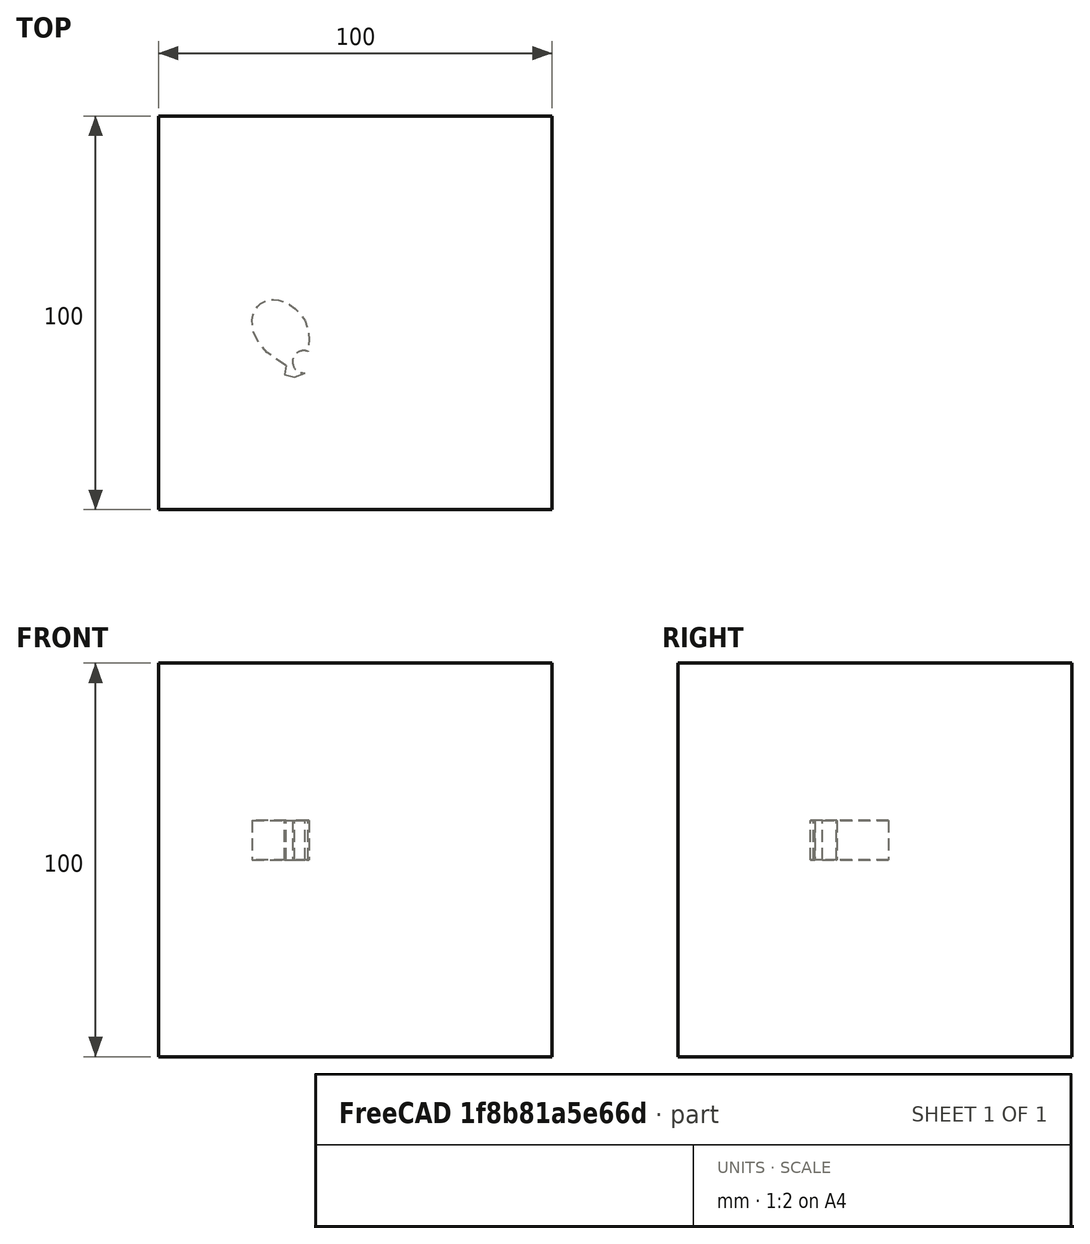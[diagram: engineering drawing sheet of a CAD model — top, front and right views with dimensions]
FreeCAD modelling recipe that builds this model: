
FCSTD DOCUMENT  (FreeCAD 1.0R39109 (Git))
Label: mirrorTest-3c
License: All rights reserved
LicenseURL: http://en.wikipedia.org/wiki/All_rights_reserved
objects: App::DocumentObjectGroupPython×1248, Part::Mirroring×2, App::Part×2, Part::FeaturePython×1, Sketcher::SketchObject×1, Part::Extrusion×1
note: 6 computed .brp shape members not serialized (recipe doc carries the construction recipe); baked Part::Feature solids carry a one-line shape summary decoded from their .brp

FEATURE [App::DocumentObjectGroupPython] HALFPI  # scripted group (container) (typed FeaturePython)
  name = HALFPI
  value = pi/2.
FEATURE [App::DocumentObjectGroupPython] PI  # scripted group (container) (typed FeaturePython)
  name = PI
  value = 1.*pi
FEATURE [App::DocumentObjectGroupPython] TWOPI  # scripted group (container) (typed FeaturePython)
  name = TWOPI
  value = 2.*pi
FEATURE [App::DocumentObjectGroupPython] Constants  # scripted group (container) (typed FeaturePython)
  Group = -> [HALFPI,PI,TWOPI]
FEATURE [App::DocumentObjectGroupPython] Variables  # scripted group (container) (typed FeaturePython)
FEATURE [App::DocumentObjectGroupPython] Quantities  # scripted group (container) (typed FeaturePython)
FEATURE [App::DocumentObjectGroupPython] Isotopes  # scripted group (container) (typed FeaturePython)
FEATURE [App::DocumentObjectGroupPython] Elements  # scripted group (container) (typed FeaturePython)
FEATURE [App::DocumentObjectGroupPython] G4Isotopes  # scripted group (container) (typed FeaturePython)
FEATURE [App::DocumentObjectGroupPython] H_element  # scripted group (container) (typed FeaturePython)
  Z = 1
  atom_value = 1.008
  formula = H
  name = H_element
FEATURE [App::DocumentObjectGroupPython] He_element  # scripted group (container) (typed FeaturePython)
  Z = 2
  atom_value = 4.0026
  formula = He
  name = He_element
FEATURE [App::DocumentObjectGroupPython] Li_element  # scripted group (container) (typed FeaturePython)
  Z = 3
  atom_value = 6.94
  formula = Li
  name = Li_element
FEATURE [App::DocumentObjectGroupPython] Be_element  # scripted group (container) (typed FeaturePython)
  Z = 4
  atom_value = 9.01218
  formula = Be
  name = Be_element
FEATURE [App::DocumentObjectGroupPython] B_element  # scripted group (container) (typed FeaturePython)
  Z = 5
  atom_value = 10.81
  formula = B
  name = B_element
FEATURE [App::DocumentObjectGroupPython] C_element  # scripted group (container) (typed FeaturePython)
  Z = 6
  atom_value = 12.011
  formula = C
  name = C_element
FEATURE [App::DocumentObjectGroupPython] N_element  # scripted group (container) (typed FeaturePython)
  Z = 7
  atom_value = 14.007
  formula = N
  name = N_element
FEATURE [App::DocumentObjectGroupPython] O_element  # scripted group (container) (typed FeaturePython)
  Z = 8
  atom_value = 15.999
  formula = O
  name = O_element
FEATURE [App::DocumentObjectGroupPython] F_element  # scripted group (container) (typed FeaturePython)
  Z = 9
  atom_value = 18.9984
  formula = F
  name = F_element
FEATURE [App::DocumentObjectGroupPython] Ne_element  # scripted group (container) (typed FeaturePython)
  Z = 10
  atom_value = 20.1797
  formula = Ne
  name = Ne_element
FEATURE [App::DocumentObjectGroupPython] Na_element  # scripted group (container) (typed FeaturePython)
  Z = 11
  atom_value = 22.9898
  formula = Na
  name = Na_element
FEATURE [App::DocumentObjectGroupPython] Mg_element  # scripted group (container) (typed FeaturePython)
  Z = 12
  atom_value = 24.305
  formula = Mg
  name = Mg_element
FEATURE [App::DocumentObjectGroupPython] Al_element  # scripted group (container) (typed FeaturePython)
  Z = 13
  atom_value = 26.9815
  formula = Al
  name = Al_element
FEATURE [App::DocumentObjectGroupPython] Si_element  # scripted group (container) (typed FeaturePython)
  Z = 14
  atom_value = 28.085
  formula = Si
  name = Si_element
FEATURE [App::DocumentObjectGroupPython] P_element  # scripted group (container) (typed FeaturePython)
  Z = 15
  atom_value = 30.9738
  formula = P
  name = P_element
FEATURE [App::DocumentObjectGroupPython] S_element  # scripted group (container) (typed FeaturePython)
  Z = 16
  atom_value = 32.06
  formula = S
  name = S_element
FEATURE [App::DocumentObjectGroupPython] Cl_element  # scripted group (container) (typed FeaturePython)
  Z = 17
  atom_value = 35.45
  formula = Cl
  name = Cl_element
FEATURE [App::DocumentObjectGroupPython] Ar_element  # scripted group (container) (typed FeaturePython)
  Z = 18
  atom_value = 39.95
  formula = Ar
  name = Ar_element
FEATURE [App::DocumentObjectGroupPython] K_element  # scripted group (container) (typed FeaturePython)
  Z = 19
  atom_value = 39.0983
  formula = K
  name = K_element
FEATURE [App::DocumentObjectGroupPython] Ca_element  # scripted group (container) (typed FeaturePython)
  Z = 20
  atom_value = 40.078
  formula = Ca
  name = Ca_element
FEATURE [App::DocumentObjectGroupPython] Sc_element  # scripted group (container) (typed FeaturePython)
  Z = 21
  atom_value = 44.9559
  formula = Sc
  name = Sc_element
FEATURE [App::DocumentObjectGroupPython] Ti_element  # scripted group (container) (typed FeaturePython)
  Z = 22
  atom_value = 47.867
  formula = Ti
  name = Ti_element
FEATURE [App::DocumentObjectGroupPython] V_element  # scripted group (container) (typed FeaturePython)
  Z = 23
  atom_value = 50.9415
  formula = V
  name = V_element
FEATURE [App::DocumentObjectGroupPython] Cr_element  # scripted group (container) (typed FeaturePython)
  Z = 24
  atom_value = 51.9961
  formula = Cr
  name = Cr_element
FEATURE [App::DocumentObjectGroupPython] Mn_element  # scripted group (container) (typed FeaturePython)
  Z = 25
  atom_value = 54.938
  formula = Mn
  name = Mn_element
FEATURE [App::DocumentObjectGroupPython] Fe_element  # scripted group (container) (typed FeaturePython)
  Z = 26
  atom_value = 55.845
  formula = Fe
  name = Fe_element
FEATURE [App::DocumentObjectGroupPython] Co_element  # scripted group (container) (typed FeaturePython)
  Z = 27
  atom_value = 58.9332
  formula = Co
  name = Co_element
FEATURE [App::DocumentObjectGroupPython] Ni_element  # scripted group (container) (typed FeaturePython)
  Z = 28
  atom_value = 58.6934
  formula = Ni
  name = Ni_element
FEATURE [App::DocumentObjectGroupPython] Cu_element  # scripted group (container) (typed FeaturePython)
  Z = 29
  atom_value = 63.546
  formula = Cu
  name = Cu_element
FEATURE [App::DocumentObjectGroupPython] Zn_element  # scripted group (container) (typed FeaturePython)
  Z = 30
  atom_value = 65.38
  formula = Zn
  name = Zn_element
FEATURE [App::DocumentObjectGroupPython] Ga_element  # scripted group (container) (typed FeaturePython)
  Z = 31
  atom_value = 69.723
  formula = Ga
  name = Ga_element
FEATURE [App::DocumentObjectGroupPython] Ge_element  # scripted group (container) (typed FeaturePython)
  Z = 32
  atom_value = 72.63
  formula = Ge
  name = Ge_element
FEATURE [App::DocumentObjectGroupPython] As_element  # scripted group (container) (typed FeaturePython)
  Z = 33
  atom_value = 74.9216
  formula = As
  name = As_element
FEATURE [App::DocumentObjectGroupPython] Se_element  # scripted group (container) (typed FeaturePython)
  Z = 34
  atom_value = 78.971
  formula = Se
  name = Se_element
FEATURE [App::DocumentObjectGroupPython] Br_element  # scripted group (container) (typed FeaturePython)
  Z = 35
  atom_value = 79.904
  formula = Br
  name = Br_element
FEATURE [App::DocumentObjectGroupPython] Kr_element  # scripted group (container) (typed FeaturePython)
  Z = 36
  atom_value = 83.798
  formula = Kr
  name = Kr_element
FEATURE [App::DocumentObjectGroupPython] Rb_element  # scripted group (container) (typed FeaturePython)
  Z = 37
  atom_value = 85.4678
  formula = Rb
  name = Rb_element
FEATURE [App::DocumentObjectGroupPython] Sr_element  # scripted group (container) (typed FeaturePython)
  Z = 38
  atom_value = 87.62
  formula = Sr
  name = Sr_element
FEATURE [App::DocumentObjectGroupPython] Y_element  # scripted group (container) (typed FeaturePython)
  Z = 39
  atom_value = 88.9058
  formula = Y
  name = Y_element
FEATURE [App::DocumentObjectGroupPython] Zr_element  # scripted group (container) (typed FeaturePython)
  Z = 40
  atom_value = 91.224
  formula = Zr
  name = Zr_element
FEATURE [App::DocumentObjectGroupPython] Nb_element  # scripted group (container) (typed FeaturePython)
  Z = 41
  atom_value = 92.9064
  formula = Nb
  name = Nb_element
FEATURE [App::DocumentObjectGroupPython] Mo_element  # scripted group (container) (typed FeaturePython)
  Z = 42
  atom_value = 95.95
  formula = Mo
  name = Mo_element
FEATURE [App::DocumentObjectGroupPython] Tc_element  # scripted group (container) (typed FeaturePython)
  Z = 43
  atom_value = 97
  formula = Tc
  name = Tc_element
FEATURE [App::DocumentObjectGroupPython] Ru_element  # scripted group (container) (typed FeaturePython)
  Z = 44
  atom_value = 101.07
  formula = Ru
  name = Ru_element
FEATURE [App::DocumentObjectGroupPython] Rh_element  # scripted group (container) (typed FeaturePython)
  Z = 45
  atom_value = 102.905
  formula = Rh
  name = Rh_element
FEATURE [App::DocumentObjectGroupPython] Pd_element  # scripted group (container) (typed FeaturePython)
  Z = 46
  atom_value = 106.42
  formula = Pd
  name = Pd_element
FEATURE [App::DocumentObjectGroupPython] Ag_element  # scripted group (container) (typed FeaturePython)
  Z = 47
  atom_value = 107.868
  formula = Ag
  name = Ag_element
FEATURE [App::DocumentObjectGroupPython] Cd_element  # scripted group (container) (typed FeaturePython)
  Z = 48
  atom_value = 112.414
  formula = Cd
  name = Cd_element
FEATURE [App::DocumentObjectGroupPython] In_element  # scripted group (container) (typed FeaturePython)
  Z = 49
  atom_value = 114.818
  formula = In
  name = In_element
FEATURE [App::DocumentObjectGroupPython] Sn_element  # scripted group (container) (typed FeaturePython)
  Z = 50
  atom_value = 118.71
  formula = Sn
  name = Sn_element
FEATURE [App::DocumentObjectGroupPython] Sb_element  # scripted group (container) (typed FeaturePython)
  Z = 51
  atom_value = 121.76
  formula = Sb
  name = Sb_element
FEATURE [App::DocumentObjectGroupPython] Te_element  # scripted group (container) (typed FeaturePython)
  Z = 52
  atom_value = 127.6
  formula = Te
  name = Te_element
FEATURE [App::DocumentObjectGroupPython] I_element  # scripted group (container) (typed FeaturePython)
  Z = 53
  atom_value = 126.904
  formula = I
  name = I_element
FEATURE [App::DocumentObjectGroupPython] Xe_element  # scripted group (container) (typed FeaturePython)
  Z = 54
  atom_value = 131.293
  formula = Xe
  name = Xe_element
FEATURE [App::DocumentObjectGroupPython] Cs_element  # scripted group (container) (typed FeaturePython)
  Z = 55
  atom_value = 132.905
  formula = Cs
  name = Cs_element
FEATURE [App::DocumentObjectGroupPython] Ba_element  # scripted group (container) (typed FeaturePython)
  Z = 56
  atom_value = 137.327
  formula = Ba
  name = Ba_element
FEATURE [App::DocumentObjectGroupPython] La_element  # scripted group (container) (typed FeaturePython)
  Z = 57
  atom_value = 138.905
  formula = La
  name = La_element
FEATURE [App::DocumentObjectGroupPython] Ce_element  # scripted group (container) (typed FeaturePython)
  Z = 58
  atom_value = 140.116
  formula = Ce
  name = Ce_element
FEATURE [App::DocumentObjectGroupPython] Pr_element  # scripted group (container) (typed FeaturePython)
  Z = 59
  atom_value = 140.908
  formula = Pr
  name = Pr_element
FEATURE [App::DocumentObjectGroupPython] Nd_element  # scripted group (container) (typed FeaturePython)
  Z = 60
  atom_value = 144.242
  formula = Nd
  name = Nd_element
FEATURE [App::DocumentObjectGroupPython] Pm_element  # scripted group (container) (typed FeaturePython)
  Z = 61
  atom_value = 145
  formula = Pm
  name = Pm_element
FEATURE [App::DocumentObjectGroupPython] Sm_element  # scripted group (container) (typed FeaturePython)
  Z = 62
  atom_value = 150.36
  formula = Sm
  name = Sm_element
FEATURE [App::DocumentObjectGroupPython] Eu_element  # scripted group (container) (typed FeaturePython)
  Z = 63
  atom_value = 151.964
  formula = Eu
  name = Eu_element
FEATURE [App::DocumentObjectGroupPython] Gd_element  # scripted group (container) (typed FeaturePython)
  Z = 64
  atom_value = 157.25
  formula = Gd
  name = Gd_element
FEATURE [App::DocumentObjectGroupPython] Tb_element  # scripted group (container) (typed FeaturePython)
  Z = 65
  atom_value = 158.925
  formula = Tb
  name = Tb_element
FEATURE [App::DocumentObjectGroupPython] Dy_element  # scripted group (container) (typed FeaturePython)
  Z = 66
  atom_value = 162.5
  formula = Dy
  name = Dy_element
FEATURE [App::DocumentObjectGroupPython] Ho_element  # scripted group (container) (typed FeaturePython)
  Z = 67
  atom_value = 164.93
  formula = Ho
  name = Ho_element
FEATURE [App::DocumentObjectGroupPython] Er_element  # scripted group (container) (typed FeaturePython)
  Z = 68
  atom_value = 167.259
  formula = Er
  name = Er_element
FEATURE [App::DocumentObjectGroupPython] Tm_element  # scripted group (container) (typed FeaturePython)
  Z = 69
  atom_value = 168.934
  formula = Tm
  name = Tm_element
FEATURE [App::DocumentObjectGroupPython] Yb_element  # scripted group (container) (typed FeaturePython)
  Z = 70
  atom_value = 173.045
  formula = Yb
  name = Yb_element
FEATURE [App::DocumentObjectGroupPython] Lu_element  # scripted group (container) (typed FeaturePython)
  Z = 71
  atom_value = 174.967
  formula = Lu
  name = Lu_element
FEATURE [App::DocumentObjectGroupPython] Hf_element  # scripted group (container) (typed FeaturePython)
  Z = 72
  atom_value = 178.49
  formula = Hf
  name = Hf_element
FEATURE [App::DocumentObjectGroupPython] Ta_element  # scripted group (container) (typed FeaturePython)
  Z = 73
  atom_value = 180.948
  formula = Ta
  name = Ta_element
FEATURE [App::DocumentObjectGroupPython] W_element  # scripted group (container) (typed FeaturePython)
  Z = 74
  atom_value = 183.84
  formula = W
  name = W_element
FEATURE [App::DocumentObjectGroupPython] Re_element  # scripted group (container) (typed FeaturePython)
  Z = 75
  atom_value = 186.207
  formula = Re
  name = Re_element
FEATURE [App::DocumentObjectGroupPython] Os_element  # scripted group (container) (typed FeaturePython)
  Z = 76
  atom_value = 190.23
  formula = Os
  name = Os_element
FEATURE [App::DocumentObjectGroupPython] Ir_element  # scripted group (container) (typed FeaturePython)
  Z = 77
  atom_value = 192.217
  formula = Ir
  name = Ir_element
FEATURE [App::DocumentObjectGroupPython] Pt_element  # scripted group (container) (typed FeaturePython)
  Z = 78
  atom_value = 195.084
  formula = Pt
  name = Pt_element
FEATURE [App::DocumentObjectGroupPython] Au_element  # scripted group (container) (typed FeaturePython)
  Z = 79
  atom_value = 196.967
  formula = Au
  name = Au_element
FEATURE [App::DocumentObjectGroupPython] Hg_element  # scripted group (container) (typed FeaturePython)
  Z = 80
  atom_value = 200.592
  formula = Hg
  name = Hg_element
FEATURE [App::DocumentObjectGroupPython] Tl_element  # scripted group (container) (typed FeaturePython)
  Z = 81
  atom_value = 204.38
  formula = Tl
  name = Tl_element
FEATURE [App::DocumentObjectGroupPython] Pb_element  # scripted group (container) (typed FeaturePython)
  Z = 82
  atom_value = 207.2
  formula = Pb
  name = Pb_element
FEATURE [App::DocumentObjectGroupPython] Bi_element  # scripted group (container) (typed FeaturePython)
  Z = 83
  atom_value = 208.98
  formula = Bi
  name = Bi_element
FEATURE [App::DocumentObjectGroupPython] Po_element  # scripted group (container) (typed FeaturePython)
  Z = 84
  atom_value = 209
  formula = Po
  name = Po_element
FEATURE [App::DocumentObjectGroupPython] At_element  # scripted group (container) (typed FeaturePython)
  Z = 85
  atom_value = 210
  formula = At
  name = At_element
FEATURE [App::DocumentObjectGroupPython] Rn_element  # scripted group (container) (typed FeaturePython)
  Z = 86
  atom_value = 222
  formula = Rn
  name = Rn_element
FEATURE [App::DocumentObjectGroupPython] Fr_element  # scripted group (container) (typed FeaturePython)
  Z = 87
  atom_value = 223
  formula = Fr
  name = Fr_element
FEATURE [App::DocumentObjectGroupPython] Ra_element  # scripted group (container) (typed FeaturePython)
  Z = 88
  atom_value = 226
  formula = Ra
  name = Ra_element
FEATURE [App::DocumentObjectGroupPython] Ac_element  # scripted group (container) (typed FeaturePython)
  Z = 89
  atom_value = 227
  formula = Ac
  name = Ac_element
FEATURE [App::DocumentObjectGroupPython] Th_element  # scripted group (container) (typed FeaturePython)
  Z = 90
  atom_value = 232.038
  formula = Th
  name = Th_element
FEATURE [App::DocumentObjectGroupPython] Pa_element  # scripted group (container) (typed FeaturePython)
  Z = 91
  atom_value = 231.036
  formula = Pa
  name = Pa_element
FEATURE [App::DocumentObjectGroupPython] U_element  # scripted group (container) (typed FeaturePython)
  Z = 92
  atom_value = 238.029
  formula = U
  name = U_element
FEATURE [App::DocumentObjectGroupPython] Np_element  # scripted group (container) (typed FeaturePython)
  Z = 93
  atom_value = 237
  formula = Np
  name = Np_element
FEATURE [App::DocumentObjectGroupPython] Pu_element  # scripted group (container) (typed FeaturePython)
  Z = 94
  atom_value = 244
  formula = Pu
  name = Pu_element
FEATURE [App::DocumentObjectGroupPython] Am_element  # scripted group (container) (typed FeaturePython)
  Z = 95
  atom_value = 243
  formula = Am
  name = Am_element
FEATURE [App::DocumentObjectGroupPython] Cm_element  # scripted group (container) (typed FeaturePython)
  Z = 96
  atom_value = 247
  formula = Cm
  name = Cm_element
FEATURE [App::DocumentObjectGroupPython] Bk_element  # scripted group (container) (typed FeaturePython)
  Z = 97
  atom_value = 247
  formula = Bk
  name = Bk_element
FEATURE [App::DocumentObjectGroupPython] Cf_element  # scripted group (container) (typed FeaturePython)
  Z = 98
  atom_value = 251
  formula = Cf
  name = Cf_element
FEATURE [App::DocumentObjectGroupPython] G4Elements  # scripted group (container) (typed FeaturePython)
  Group = -> [H_element,He_element,Li_element,Be_element,B_element,C_element,N_element,O_element,F_element,Ne_element,Na_element,Mg_element,Al_element,Si_element,P_element,S_element,Cl_element,Ar_element,K_element,Ca_element,Sc_element,Ti_element,V_element,Cr_element,Mn_element,Fe_element,Co_element,Ni_element,Cu_element,Zn_element,Ga_element,Ge_element,As_element,Se_element,Br_element,Kr_element,Rb_element,+61 more]
FEATURE [App::DocumentObjectGroupPython] H_element001  label="H_element : 0.101"  # scripted group (container) (typed FeaturePython)
  n = 0.101327
FEATURE [App::DocumentObjectGroupPython] C_element001  label="C_element : 0.775"  # scripted group (container) (typed FeaturePython)
  n = 0.7755
FEATURE [App::DocumentObjectGroupPython] N_element001  label="N_element : 0.035"  # scripted group (container) (typed FeaturePython)
  n = 0.035057
FEATURE [App::DocumentObjectGroupPython] O_element001  label="O_element : 0.052"  # scripted group (container) (typed FeaturePython)
  n = 0.0523159
FEATURE [App::DocumentObjectGroupPython] F_element001  label="F_element : 0.017"  # scripted group (container) (typed FeaturePython)
  n = 0.017422
FEATURE [App::DocumentObjectGroupPython] Ca_element001  label="Ca_element : 0.018"  # scripted group (container) (typed FeaturePython)
  n = 0.018378
FEATURE [App::DocumentObjectGroupPython] G4_A_150_TISSUE  label="G4_A-150_TISSUE"  # scripted group (container) (typed FeaturePython)
  Dunit = g/cm3
  Dvalue = 1.127
  Group = -> [H_element001,C_element001,N_element001,O_element001,F_element001,Ca_element001]
  conduct = 2
  density = 1
  expand = 3
  formula = G4_A-150_TISSUE
  name = G4_A-150_TISSUE
  specific = 4
FEATURE [App::DocumentObjectGroupPython] C_element002  label="C_element : 3"  # scripted group (container) (typed FeaturePython)
  n = 3
  ref = C_element
FEATURE [App::DocumentObjectGroupPython] H_element002  label="H_element : 6"  # scripted group (container) (typed FeaturePython)
  n = 6
  ref = H_element
FEATURE [App::DocumentObjectGroupPython] O_element002  label="O_element : 1"  # scripted group (container) (typed FeaturePython)
  n = 1
  ref = O_element
FEATURE [App::DocumentObjectGroupPython] G4_ACETONE  # scripted group (container) (typed FeaturePython)
  Dunit = g/cm3
  Dvalue = 0.7899
  Group = -> [C_element002,H_element002,O_element002]
  conduct = 2
  density = 1
  expand = 3
  formula = G4_ACETONE
  name = G4_ACETONE
  specific = 4
FEATURE [App::DocumentObjectGroupPython] C_element003  label="C_element : 2"  # scripted group (container) (typed FeaturePython)
  n = 2
  ref = C_element
FEATURE [App::DocumentObjectGroupPython] H_element003  label="H_element : 2"  # scripted group (container) (typed FeaturePython)
  n = 2
  ref = H_element
FEATURE [App::DocumentObjectGroupPython] G4_ACETYLENE  # scripted group (container) (typed FeaturePython)
  Dunit = g/cm3
  Dvalue = 0.0010967
  Group = -> [C_element003,H_element003]
  conduct = 2
  density = 1
  expand = 3
  formula = G4_ACETYLENE
  name = G4_ACETYLENE
  specific = 4
FEATURE [App::DocumentObjectGroupPython] C_element004  label="C_element : 5"  # scripted group (container) (typed FeaturePython)
  n = 5
  ref = C_element
FEATURE [App::DocumentObjectGroupPython] H_element004  label="H_element : 5"  # scripted group (container) (typed FeaturePython)
  n = 5
  ref = H_element
FEATURE [App::DocumentObjectGroupPython] N_element002  label="N_element : 5"  # scripted group (container) (typed FeaturePython)
  n = 5
  ref = N_element
FEATURE [App::DocumentObjectGroupPython] G4_ADENINE  # scripted group (container) (typed FeaturePython)
  Dunit = g/cm3
  Dvalue = 1.6
  Group = -> [C_element004,H_element004,N_element002]
  conduct = 2
  density = 1
  expand = 3
  formula = G4_ADENINE
  name = G4_ADENINE
  specific = 4
FEATURE [App::DocumentObjectGroupPython] H_element005  label="H_element : 0.114"  # scripted group (container) (typed FeaturePython)
  n = 0.114
FEATURE [App::DocumentObjectGroupPython] C_element005  label="C_element : 0.598"  # scripted group (container) (typed FeaturePython)
  n = 0.598
FEATURE [App::DocumentObjectGroupPython] N_element003  label="N_element : 0.007"  # scripted group (container) (typed FeaturePython)
  n = 0.007
FEATURE [App::DocumentObjectGroupPython] O_element003  label="O_element : 0.278"  # scripted group (container) (typed FeaturePython)
  n = 0.278
FEATURE [App::DocumentObjectGroupPython] Na_element001  label="Na_element : 0.001"  # scripted group (container) (typed FeaturePython)
  n = 0.001
FEATURE [App::DocumentObjectGroupPython] S_element001  label="S_element : 0.001"  # scripted group (container) (typed FeaturePython)
  n = 0.001
FEATURE [App::DocumentObjectGroupPython] Cl_element001  label="Cl_element : 0.001"  # scripted group (container) (typed FeaturePython)
  n = 0.001
FEATURE [App::DocumentObjectGroupPython] G4_ADIPOSE_TISSUE_ICRP  # scripted group (container) (typed FeaturePython)
  Dunit = g/cm3
  Dvalue = 0.95
  Group = -> [H_element005,C_element005,N_element003,O_element003,Na_element001,S_element001,Cl_element001]
  conduct = 2
  density = 1
  expand = 3
  formula = G4_ADIPOSE_TISSUE_ICRP
  name = G4_ADIPOSE_TISSUE_ICRP
  specific = 4
FEATURE [App::DocumentObjectGroupPython] C_element006  label="C_element : 0.000"  # scripted group (container) (typed FeaturePython)
  n = 0.000124
FEATURE [App::DocumentObjectGroupPython] N_element004  label="N_element : 0.755"  # scripted group (container) (typed FeaturePython)
  n = 0.755268
FEATURE [App::DocumentObjectGroupPython] O_element004  label="O_element : 0.232"  # scripted group (container) (typed FeaturePython)
  n = 0.231781
FEATURE [App::DocumentObjectGroupPython] Ar_element001  label="Ar_element : 0.013"  # scripted group (container) (typed FeaturePython)
  n = 0.012827
FEATURE [App::DocumentObjectGroupPython] G4_AIR  # scripted group (container) (typed FeaturePython)
  Dunit = g/cm3
  Dvalue = 0.00120479
  Group = -> [C_element006,N_element004,O_element004,Ar_element001]
  conduct = 2
  density = 1
  expand = 3
  formula = G4_AIR
  name = G4_AIR
  specific = 4
FEATURE [App::DocumentObjectGroupPython] C_element007  label="C_element : 006"  # scripted group (container) (typed FeaturePython)
  n = 3
  ref = C_element
FEATURE [App::DocumentObjectGroupPython] H_element006  label="H_element : 7"  # scripted group (container) (typed FeaturePython)
  n = 7
  ref = H_element
FEATURE [App::DocumentObjectGroupPython] N_element005  label="N_element : 1"  # scripted group (container) (typed FeaturePython)
  n = 1
  ref = N_element
FEATURE [App::DocumentObjectGroupPython] O_element005  label="O_element : 2"  # scripted group (container) (typed FeaturePython)
  n = 2
  ref = O_element
FEATURE [App::DocumentObjectGroupPython] G4_ALANINE  # scripted group (container) (typed FeaturePython)
  Dunit = g/cm3
  Dvalue = 1.42
  Group = -> [C_element007,H_element006,N_element005,O_element005]
  conduct = 2
  density = 1
  expand = 3
  formula = G4_ALANINE
  name = G4_ALANINE
  specific = 4
FEATURE [App::DocumentObjectGroupPython] Al_element001  label="Al_element : 2"  # scripted group (container) (typed FeaturePython)
  n = 2
  ref = Al_element
FEATURE [App::DocumentObjectGroupPython] O_element006  label="O_element : 3"  # scripted group (container) (typed FeaturePython)
  n = 3
  ref = O_element
FEATURE [App::DocumentObjectGroupPython] G4_ALUMINUM_OXIDE  # scripted group (container) (typed FeaturePython)
  Dunit = g/cm3
  Dvalue = 3.97
  Group = -> [Al_element001,O_element006]
  conduct = 2
  density = 1
  expand = 3
  formula = G4_ALUMINUM_OXIDE
  name = G4_ALUMINUM_OXIDE
  specific = 4
FEATURE [App::DocumentObjectGroupPython] H_element007  label="H_element : 0.106"  # scripted group (container) (typed FeaturePython)
  n = 0.10593
FEATURE [App::DocumentObjectGroupPython] C_element008  label="C_element : 0.789"  # scripted group (container) (typed FeaturePython)
  n = 0.788974
FEATURE [App::DocumentObjectGroupPython] O_element007  label="O_element : 0.105"  # scripted group (container) (typed FeaturePython)
  n = 0.105096
FEATURE [App::DocumentObjectGroupPython] G4_AMBER  # scripted group (container) (typed FeaturePython)
  Dunit = g/cm3
  Dvalue = 1.1
  Group = -> [H_element007,C_element008,O_element007]
  conduct = 2
  density = 1
  expand = 3
  formula = G4_AMBER
  name = G4_AMBER
  specific = 4
FEATURE [App::DocumentObjectGroupPython] N_element006  label="N_element : 006"  # scripted group (container) (typed FeaturePython)
  n = 1
  ref = N_element
FEATURE [App::DocumentObjectGroupPython] H_element008  label="H_element : 3"  # scripted group (container) (typed FeaturePython)
  n = 3
  ref = H_element
FEATURE [App::DocumentObjectGroupPython] G4_AMMONIA  # scripted group (container) (typed FeaturePython)
  Dunit = g/cm3
  Dvalue = 0.000826019
  Group = -> [N_element006,H_element008]
  conduct = 2
  density = 1
  expand = 3
  formula = G4_AMMONIA
  name = G4_AMMONIA
  specific = 4
FEATURE [App::DocumentObjectGroupPython] C_element009  label="C_element : 6"  # scripted group (container) (typed FeaturePython)
  n = 6
  ref = C_element
FEATURE [App::DocumentObjectGroupPython] H_element009  label="H_element : 008"  # scripted group (container) (typed FeaturePython)
  n = 7
  ref = H_element
FEATURE [App::DocumentObjectGroupPython] N_element007  label="N_element : 007"  # scripted group (container) (typed FeaturePython)
  n = 1
  ref = N_element
FEATURE [App::DocumentObjectGroupPython] G4_ANILINE  # scripted group (container) (typed FeaturePython)
  Dunit = g/cm3
  Dvalue = 1.0235
  Group = -> [C_element009,H_element009,N_element007]
  conduct = 2
  density = 1
  expand = 3
  formula = G4_ANILINE
  name = G4_ANILINE
  specific = 4
FEATURE [App::DocumentObjectGroupPython] C_element010  label="C_element : 14"  # scripted group (container) (typed FeaturePython)
  n = 14
  ref = C_element
FEATURE [App::DocumentObjectGroupPython] H_element010  label="H_element : 10"  # scripted group (container) (typed FeaturePython)
  n = 10
  ref = H_element
FEATURE [App::DocumentObjectGroupPython] G4_ANTHRACENE  # scripted group (container) (typed FeaturePython)
  Dunit = g/cm3
  Dvalue = 1.283
  Group = -> [C_element010,H_element010]
  conduct = 2
  density = 1
  expand = 3
  formula = G4_ANTHRACENE
  name = G4_ANTHRACENE
  specific = 4
FEATURE [App::DocumentObjectGroupPython] H_element011  label="H_element : 0.065"  # scripted group (container) (typed FeaturePython)
  n = 0.0654709
FEATURE [App::DocumentObjectGroupPython] C_element011  label="C_element : 0.537"  # scripted group (container) (typed FeaturePython)
  n = 0.536944
FEATURE [App::DocumentObjectGroupPython] N_element008  label="N_element : 0.021"  # scripted group (container) (typed FeaturePython)
  n = 0.0215
FEATURE [App::DocumentObjectGroupPython] O_element008  label="O_element : 0.032"  # scripted group (container) (typed FeaturePython)
  n = 0.032085
FEATURE [App::DocumentObjectGroupPython] F_element002  label="F_element : 0.167"  # scripted group (container) (typed FeaturePython)
  n = 0.167411
FEATURE [App::DocumentObjectGroupPython] Ca_element002  label="Ca_element : 0.177"  # scripted group (container) (typed FeaturePython)
  n = 0.176589
FEATURE [App::DocumentObjectGroupPython] G4_B_100_BONE  label="G4_B-100_BONE"  # scripted group (container) (typed FeaturePython)
  Dunit = g/cm3
  Dvalue = 1.45
  Group = -> [H_element011,C_element011,N_element008,O_element008,F_element002,Ca_element002]
  conduct = 2
  density = 1
  expand = 3
  formula = G4_B-100_BONE
  name = G4_B-100_BONE
  specific = 4
FEATURE [App::DocumentObjectGroupPython] H_element012  label="H_element : 0.057"  # scripted group (container) (typed FeaturePython)
  n = 0.057441
FEATURE [App::DocumentObjectGroupPython] C_element012  label="C_element : 0.790"  # scripted group (container) (typed FeaturePython)
  n = 0.774591
FEATURE [App::DocumentObjectGroupPython] O_element009  label="O_element : 0.168"  # scripted group (container) (typed FeaturePython)
  n = 0.167968
FEATURE [App::DocumentObjectGroupPython] G4_BAKELITE  # scripted group (container) (typed FeaturePython)
  Dunit = g/cm3
  Dvalue = 1.25
  Group = -> [H_element012,C_element012,O_element009]
  conduct = 2
  density = 1
  expand = 3
  formula = G4_BAKELITE
  name = G4_BAKELITE
  specific = 4
FEATURE [App::DocumentObjectGroupPython] Ba_element001  label="Ba_element : 1"  # scripted group (container) (typed FeaturePython)
  n = 1
  ref = Ba_element
FEATURE [App::DocumentObjectGroupPython] F_element003  label="F_element : 2"  # scripted group (container) (typed FeaturePython)
  n = 2
  ref = F_element
FEATURE [App::DocumentObjectGroupPython] G4_BARIUM_FLUORIDE  # scripted group (container) (typed FeaturePython)
  Dunit = g/cm3
  Dvalue = 4.89
  Group = -> [Ba_element001,F_element003]
  conduct = 2
  density = 1
  expand = 3
  formula = G4_BARIUM_FLUORIDE
  name = G4_BARIUM_FLUORIDE
  specific = 4
FEATURE [App::DocumentObjectGroupPython] Ba_element002  label="Ba_element : 002"  # scripted group (container) (typed FeaturePython)
  n = 1
  ref = Ba_element
FEATURE [App::DocumentObjectGroupPython] S_element002  label="S_element : 1"  # scripted group (container) (typed FeaturePython)
  n = 1
  ref = S_element
FEATURE [App::DocumentObjectGroupPython] O_element010  label="O_element : 4"  # scripted group (container) (typed FeaturePython)
  n = 4
  ref = O_element
FEATURE [App::DocumentObjectGroupPython] G4_BARIUM_SULFATE  # scripted group (container) (typed FeaturePython)
  Dunit = g/cm3
  Dvalue = 4.5
  Group = -> [Ba_element002,S_element002,O_element010]
  conduct = 2
  density = 1
  expand = 3
  formula = G4_BARIUM_SULFATE
  name = G4_BARIUM_SULFATE
  specific = 4
FEATURE [App::DocumentObjectGroupPython] C_element013  label="C_element : 007"  # scripted group (container) (typed FeaturePython)
  n = 6
  ref = C_element
FEATURE [App::DocumentObjectGroupPython] H_element013  label="H_element : 009"  # scripted group (container) (typed FeaturePython)
  n = 6
  ref = H_element
FEATURE [App::DocumentObjectGroupPython] G4_BENZENE  # scripted group (container) (typed FeaturePython)
  Dunit = g/cm3
  Dvalue = 0.87865
  Group = -> [C_element013,H_element013]
  conduct = 2
  density = 1
  expand = 3
  formula = G4_BENZENE
  name = G4_BENZENE
  specific = 4
FEATURE [App::DocumentObjectGroupPython] Be_element001  label="Be_element : 1"  # scripted group (container) (typed FeaturePython)
  n = 1
  ref = Be_element
FEATURE [App::DocumentObjectGroupPython] O_element011  label="O_element : 005"  # scripted group (container) (typed FeaturePython)
  n = 1
  ref = O_element
FEATURE [App::DocumentObjectGroupPython] G4_BERYLLIUM_OXIDE  # scripted group (container) (typed FeaturePython)
  Dunit = g/cm3
  Dvalue = 3.01
  Group = -> [Be_element001,O_element011]
  conduct = 2
  density = 1
  expand = 3
  formula = G4_BERYLLIUM_OXIDE
  name = G4_BERYLLIUM_OXIDE
  specific = 4
FEATURE [App::DocumentObjectGroupPython] Bi_element001  label="Bi_element : 4"  # scripted group (container) (typed FeaturePython)
  n = 4
  ref = Bi_element
FEATURE [App::DocumentObjectGroupPython] Ge_element001  label="Ge_element : 3"  # scripted group (container) (typed FeaturePython)
  n = 3
  ref = Ge_element
FEATURE [App::DocumentObjectGroupPython] O_element012  label="O_element : 12"  # scripted group (container) (typed FeaturePython)
  n = 12
  ref = O_element
FEATURE [App::DocumentObjectGroupPython] G4_BGO  # scripted group (container) (typed FeaturePython)
  Dunit = g/cm3
  Dvalue = 7.13
  Group = -> [Bi_element001,Ge_element001,O_element012]
  conduct = 2
  density = 1
  expand = 3
  formula = G4_BGO
  name = G4_BGO
  specific = 4
FEATURE [App::DocumentObjectGroupPython] H_element014  label="H_element : 0.102"  # scripted group (container) (typed FeaturePython)
  n = 0.102
FEATURE [App::DocumentObjectGroupPython] C_element014  label="C_element : 0.110"  # scripted group (container) (typed FeaturePython)
  n = 0.11
FEATURE [App::DocumentObjectGroupPython] N_element009  label="N_element : 0.033"  # scripted group (container) (typed FeaturePython)
  n = 0.033
FEATURE [App::DocumentObjectGroupPython] O_element013  label="O_element : 0.745"  # scripted group (container) (typed FeaturePython)
  n = 0.745
FEATURE [App::DocumentObjectGroupPython] Na_element002  label="Na_element : 0.002"  # scripted group (container) (typed FeaturePython)
  n = 0.001
FEATURE [App::DocumentObjectGroupPython] P_element001  label="P_element : 0.001"  # scripted group (container) (typed FeaturePython)
  n = 0.001
FEATURE [App::DocumentObjectGroupPython] S_element003  label="S_element : 0.002"  # scripted group (container) (typed FeaturePython)
  n = 0.002
FEATURE [App::DocumentObjectGroupPython] Cl_element002  label="Cl_element : 0.003"  # scripted group (container) (typed FeaturePython)
  n = 0.003
FEATURE [App::DocumentObjectGroupPython] K_element001  label="K_element : 0.002"  # scripted group (container) (typed FeaturePython)
  n = 0.002
FEATURE [App::DocumentObjectGroupPython] Fe_element001  label="Fe_element : 0.001"  # scripted group (container) (typed FeaturePython)
  n = 0.001
FEATURE [App::DocumentObjectGroupPython] G4_BLOOD_ICRP  # scripted group (container) (typed FeaturePython)
  Dunit = g/cm3
  Dvalue = 1.06
  Group = -> [H_element014,C_element014,N_element009,O_element013,Na_element002,P_element001,S_element003,Cl_element002,K_element001,Fe_element001]
  conduct = 2
  density = 1
  expand = 3
  formula = G4_BLOOD_ICRP
  name = G4_BLOOD_ICRP
  specific = 4
FEATURE [App::DocumentObjectGroupPython] H_element015  label="H_element : 0.064"  # scripted group (container) (typed FeaturePython)
  n = 0.064
FEATURE [App::DocumentObjectGroupPython] C_element015  label="C_element : 0.278"  # scripted group (container) (typed FeaturePython)
  n = 0.278
FEATURE [App::DocumentObjectGroupPython] N_element010  label="N_element : 0.027"  # scripted group (container) (typed FeaturePython)
  n = 0.027
FEATURE [App::DocumentObjectGroupPython] O_element014  label="O_element : 0.410"  # scripted group (container) (typed FeaturePython)
  n = 0.41
FEATURE [App::DocumentObjectGroupPython] Mg_element001  label="Mg_element : 0.002"  # scripted group (container) (typed FeaturePython)
  n = 0.002
FEATURE [App::DocumentObjectGroupPython] P_element002  label="P_element : 0.070"  # scripted group (container) (typed FeaturePython)
  n = 0.07
FEATURE [App::DocumentObjectGroupPython] S_element004  label="S_element : 0.003"  # scripted group (container) (typed FeaturePython)
  n = 0.002
FEATURE [App::DocumentObjectGroupPython] Ca_element003  label="Ca_element : 0.147"  # scripted group (container) (typed FeaturePython)
  n = 0.147
FEATURE [App::DocumentObjectGroupPython] G4_BONE_COMPACT_ICRU  # scripted group (container) (typed FeaturePython)
  Dunit = g/cm3
  Dvalue = 1.85
  Group = -> [H_element015,C_element015,N_element010,O_element014,Mg_element001,P_element002,S_element004,Ca_element003]
  conduct = 2
  density = 1
  expand = 3
  formula = G4_BONE_COMPACT_ICRU
  name = G4_BONE_COMPACT_ICRU
  specific = 4
FEATURE [App::DocumentObjectGroupPython] H_element016  label="H_element : 0.034"  # scripted group (container) (typed FeaturePython)
  n = 0.034
FEATURE [App::DocumentObjectGroupPython] C_element016  label="C_element : 0.155"  # scripted group (container) (typed FeaturePython)
  n = 0.155
FEATURE [App::DocumentObjectGroupPython] N_element011  label="N_element : 0.042"  # scripted group (container) (typed FeaturePython)
  n = 0.042
FEATURE [App::DocumentObjectGroupPython] O_element015  label="O_element : 0.435"  # scripted group (container) (typed FeaturePython)
  n = 0.435
FEATURE [App::DocumentObjectGroupPython] Na_element003  label="Na_element : 0.003"  # scripted group (container) (typed FeaturePython)
  n = 0.001
FEATURE [App::DocumentObjectGroupPython] Mg_element002  label="Mg_element : 0.003"  # scripted group (container) (typed FeaturePython)
  n = 0.002
FEATURE [App::DocumentObjectGroupPython] P_element003  label="P_element : 0.103"  # scripted group (container) (typed FeaturePython)
  n = 0.103
FEATURE [App::DocumentObjectGroupPython] S_element005  label="S_element : 0.004"  # scripted group (container) (typed FeaturePython)
  n = 0.003
FEATURE [App::DocumentObjectGroupPython] Ca_element004  label="Ca_element : 0.225"  # scripted group (container) (typed FeaturePython)
  n = 0.225
FEATURE [App::DocumentObjectGroupPython] G4_BONE_CORTICAL_ICRP  # scripted group (container) (typed FeaturePython)
  Dunit = g/cm3
  Dvalue = 1.92
  Group = -> [H_element016,C_element016,N_element011,O_element015,Na_element003,Mg_element002,P_element003,S_element005,Ca_element004]
  conduct = 2
  density = 1
  expand = 3
  formula = G4_BONE_CORTICAL_ICRP
  name = G4_BONE_CORTICAL_ICRP
  specific = 4
FEATURE [App::DocumentObjectGroupPython] B_element001  label="B_element : 4"  # scripted group (container) (typed FeaturePython)
  n = 4
  ref = B_element
FEATURE [App::DocumentObjectGroupPython] C_element017  label="C_element : 1"  # scripted group (container) (typed FeaturePython)
  n = 1
  ref = C_element
FEATURE [App::DocumentObjectGroupPython] G4_BORON_CARBIDE  # scripted group (container) (typed FeaturePython)
  Dunit = g/cm3
  Dvalue = 2.52
  Group = -> [B_element001,C_element017]
  conduct = 2
  density = 1
  expand = 3
  formula = G4_BORON_CARBIDE
  name = G4_BORON_CARBIDE
  specific = 4
FEATURE [App::DocumentObjectGroupPython] B_element002  label="B_element : 2"  # scripted group (container) (typed FeaturePython)
  n = 2
  ref = B_element
FEATURE [App::DocumentObjectGroupPython] O_element016  label="O_element : 006"  # scripted group (container) (typed FeaturePython)
  n = 3
  ref = O_element
FEATURE [App::DocumentObjectGroupPython] G4_BORON_OXIDE  # scripted group (container) (typed FeaturePython)
  Dunit = g/cm3
  Dvalue = 1.812
  Group = -> [B_element002,O_element016]
  conduct = 2
  density = 1
  expand = 3
  formula = G4_BORON_OXIDE
  name = G4_BORON_OXIDE
  specific = 4
FEATURE [App::DocumentObjectGroupPython] H_element017  label="H_element : 0.107"  # scripted group (container) (typed FeaturePython)
  n = 0.107
FEATURE [App::DocumentObjectGroupPython] C_element018  label="C_element : 0.145"  # scripted group (container) (typed FeaturePython)
  n = 0.145
FEATURE [App::DocumentObjectGroupPython] N_element012  label="N_element : 0.022"  # scripted group (container) (typed FeaturePython)
  n = 0.022
FEATURE [App::DocumentObjectGroupPython] O_element017  label="O_element : 0.712"  # scripted group (container) (typed FeaturePython)
  n = 0.712
FEATURE [App::DocumentObjectGroupPython] Na_element004  label="Na_element : 0.004"  # scripted group (container) (typed FeaturePython)
  n = 0.002
FEATURE [App::DocumentObjectGroupPython] P_element004  label="P_element : 0.004"  # scripted group (container) (typed FeaturePython)
  n = 0.004
FEATURE [App::DocumentObjectGroupPython] S_element006  label="S_element : 0.005"  # scripted group (container) (typed FeaturePython)
  n = 0.002
FEATURE [App::DocumentObjectGroupPython] Cl_element003  label="Cl_element : 0.004"  # scripted group (container) (typed FeaturePython)
  n = 0.003
FEATURE [App::DocumentObjectGroupPython] K_element002  label="K_element : 0.003"  # scripted group (container) (typed FeaturePython)
  n = 0.003
FEATURE [App::DocumentObjectGroupPython] G4_BRAIN_ICRP  # scripted group (container) (typed FeaturePython)
  Dunit = g/cm3
  Dvalue = 1.04
  Group = -> [H_element017,C_element018,N_element012,O_element017,Na_element004,P_element004,S_element006,Cl_element003,K_element002]
  conduct = 2
  density = 1
  expand = 3
  formula = G4_BRAIN_ICRP
  name = G4_BRAIN_ICRP
  specific = 4
FEATURE [App::DocumentObjectGroupPython] C_element019  label="C_element : 4"  # scripted group (container) (typed FeaturePython)
  n = 4
  ref = C_element
FEATURE [App::DocumentObjectGroupPython] H_element018  label="H_element : 010"  # scripted group (container) (typed FeaturePython)
  n = 10
  ref = H_element
FEATURE [App::DocumentObjectGroupPython] G4_BUTANE  # scripted group (container) (typed FeaturePython)
  Dunit = g/cm3
  Dvalue = 0.00249343
  Group = -> [C_element019,H_element018]
  conduct = 2
  density = 1
  expand = 3
  formula = G4_BUTANE
  name = G4_BUTANE
  specific = 4
FEATURE [App::DocumentObjectGroupPython] C_element020  label="C_element : 008"  # scripted group (container) (typed FeaturePython)
  n = 4
  ref = C_element
FEATURE [App::DocumentObjectGroupPython] H_element019  label="H_element : 011"  # scripted group (container) (typed FeaturePython)
  n = 10
  ref = H_element
FEATURE [App::DocumentObjectGroupPython] O_element018  label="O_element : 007"  # scripted group (container) (typed FeaturePython)
  n = 1
  ref = O_element
FEATURE [App::DocumentObjectGroupPython] G4_N_BUTYL_ALCOHOL  label="G4_N-BUTYL_ALCOHOL"  # scripted group (container) (typed FeaturePython)
  Dunit = g/cm3
  Dvalue = 0.8098
  Group = -> [C_element020,H_element019,O_element018]
  conduct = 2
  density = 1
  expand = 3
  formula = G4_N-BUTYL_ALCOHOL
  name = G4_N-BUTYL_ALCOHOL
  specific = 4
FEATURE [App::DocumentObjectGroupPython] H_element020  label="H_element : 0.025"  # scripted group (container) (typed FeaturePython)
  n = 0.02468
FEATURE [App::DocumentObjectGroupPython] C_element021  label="C_element : 0.502"  # scripted group (container) (typed FeaturePython)
  n = 0.501611
FEATURE [App::DocumentObjectGroupPython] O_element019  label="O_element : 0.005"  # scripted group (container) (typed FeaturePython)
  n = 0.004527
FEATURE [App::DocumentObjectGroupPython] F_element004  label="F_element : 0.465"  # scripted group (container) (typed FeaturePython)
  n = 0.465209
FEATURE [App::DocumentObjectGroupPython] Si_element001  label="Si_element : 0.004"  # scripted group (container) (typed FeaturePython)
  n = 0.003973
FEATURE [App::DocumentObjectGroupPython] G4_C_552  label="G4_C-552"  # scripted group (container) (typed FeaturePython)
  Dunit = g/cm3
  Dvalue = 1.76
  Group = -> [H_element020,C_element021,O_element019,F_element004,Si_element001]
  conduct = 2
  density = 1
  expand = 3
  formula = G4_C-552
  name = G4_C-552
  specific = 4
FEATURE [App::DocumentObjectGroupPython] Cd_element001  label="Cd_element : 1"  # scripted group (container) (typed FeaturePython)
  n = 1
  ref = Cd_element
FEATURE [App::DocumentObjectGroupPython] Te_element001  label="Te_element : 1"  # scripted group (container) (typed FeaturePython)
  n = 1
  ref = Te_element
FEATURE [App::DocumentObjectGroupPython] G4_CADMIUM_TELLURIDE  # scripted group (container) (typed FeaturePython)
  Dunit = g/cm3
  Dvalue = 6.2
  Group = -> [Cd_element001,Te_element001]
  conduct = 2
  density = 1
  expand = 3
  formula = G4_CADMIUM_TELLURIDE
  name = G4_CADMIUM_TELLURIDE
  specific = 4
FEATURE [App::DocumentObjectGroupPython] Cd_element002  label="Cd_element : 002"  # scripted group (container) (typed FeaturePython)
  n = 1
  ref = Cd_element
FEATURE [App::DocumentObjectGroupPython] W_element001  label="W_element : 1"  # scripted group (container) (typed FeaturePython)
  n = 1
  ref = W_element
FEATURE [App::DocumentObjectGroupPython] O_element020  label="O_element : 008"  # scripted group (container) (typed FeaturePython)
  n = 4
  ref = O_element
FEATURE [App::DocumentObjectGroupPython] G4_CADMIUM_TUNGSTATE  # scripted group (container) (typed FeaturePython)
  Dunit = g/cm3
  Dvalue = 7.9
  Group = -> [Cd_element002,W_element001,O_element020]
  conduct = 2
  density = 1
  expand = 3
  formula = G4_CADMIUM_TUNGSTATE
  name = G4_CADMIUM_TUNGSTATE
  specific = 4
FEATURE [App::DocumentObjectGroupPython] Ca_element005  label="Ca_element : 1"  # scripted group (container) (typed FeaturePython)
  n = 1
  ref = Ca_element
FEATURE [App::DocumentObjectGroupPython] C_element022  label="C_element : 009"  # scripted group (container) (typed FeaturePython)
  n = 1
  ref = C_element
FEATURE [App::DocumentObjectGroupPython] O_element021  label="O_element : 009"  # scripted group (container) (typed FeaturePython)
  n = 3
  ref = O_element
FEATURE [App::DocumentObjectGroupPython] G4_CALCIUM_CARBONATE  # scripted group (container) (typed FeaturePython)
  Dunit = g/cm3
  Dvalue = 2.8
  Group = -> [Ca_element005,C_element022,O_element021]
  conduct = 2
  density = 1
  expand = 3
  formula = G4_CALCIUM_CARBONATE
  name = G4_CALCIUM_CARBONATE
  specific = 4
FEATURE [App::DocumentObjectGroupPython] Ca_element006  label="Ca_element : 002"  # scripted group (container) (typed FeaturePython)
  n = 1
  ref = Ca_element
FEATURE [App::DocumentObjectGroupPython] F_element005  label="F_element : 003"  # scripted group (container) (typed FeaturePython)
  n = 2
  ref = F_element
FEATURE [App::DocumentObjectGroupPython] G4_CALCIUM_FLUORIDE  # scripted group (container) (typed FeaturePython)
  Dunit = g/cm3
  Dvalue = 3.18
  Group = -> [Ca_element006,F_element005]
  conduct = 2
  density = 1
  expand = 3
  formula = G4_CALCIUM_FLUORIDE
  name = G4_CALCIUM_FLUORIDE
  specific = 4
FEATURE [App::DocumentObjectGroupPython] Ca_element007  label="Ca_element : 003"  # scripted group (container) (typed FeaturePython)
  n = 1
  ref = Ca_element
FEATURE [App::DocumentObjectGroupPython] O_element022  label="O_element : 010"  # scripted group (container) (typed FeaturePython)
  n = 1
  ref = O_element
FEATURE [App::DocumentObjectGroupPython] G4_CALCIUM_OXIDE  # scripted group (container) (typed FeaturePython)
  Dunit = g/cm3
  Dvalue = 3.3
  Group = -> [Ca_element007,O_element022]
  conduct = 2
  density = 1
  expand = 3
  formula = G4_CALCIUM_OXIDE
  name = G4_CALCIUM_OXIDE
  specific = 4
FEATURE [App::DocumentObjectGroupPython] Ca_element008  label="Ca_element : 004"  # scripted group (container) (typed FeaturePython)
  n = 1
  ref = Ca_element
FEATURE [App::DocumentObjectGroupPython] S_element007  label="S_element : 002"  # scripted group (container) (typed FeaturePython)
  n = 1
  ref = S_element
FEATURE [App::DocumentObjectGroupPython] O_element023  label="O_element : 011"  # scripted group (container) (typed FeaturePython)
  n = 4
  ref = O_element
FEATURE [App::DocumentObjectGroupPython] G4_CALCIUM_SULFATE  # scripted group (container) (typed FeaturePython)
  Dunit = g/cm3
  Dvalue = 2.96
  Group = -> [Ca_element008,S_element007,O_element023]
  conduct = 2
  density = 1
  expand = 3
  formula = G4_CALCIUM_SULFATE
  name = G4_CALCIUM_SULFATE
  specific = 4
FEATURE [App::DocumentObjectGroupPython] Ca_element009  label="Ca_element : 005"  # scripted group (container) (typed FeaturePython)
  n = 1
  ref = Ca_element
FEATURE [App::DocumentObjectGroupPython] W_element002  label="W_element : 002"  # scripted group (container) (typed FeaturePython)
  n = 1
  ref = W_element
FEATURE [App::DocumentObjectGroupPython] O_element024  label="O_element : 012"  # scripted group (container) (typed FeaturePython)
  n = 4
  ref = O_element
FEATURE [App::DocumentObjectGroupPython] G4_CALCIUM_TUNGSTATE  # scripted group (container) (typed FeaturePython)
  Dunit = g/cm3
  Dvalue = 6.062
  Group = -> [Ca_element009,W_element002,O_element024]
  conduct = 2
  density = 1
  expand = 3
  formula = G4_CALCIUM_TUNGSTATE
  name = G4_CALCIUM_TUNGSTATE
  specific = 4
FEATURE [App::DocumentObjectGroupPython] C_element023  label="C_element : 010"  # scripted group (container) (typed FeaturePython)
  n = 1
  ref = C_element
FEATURE [App::DocumentObjectGroupPython] O_element025  label="O_element : 013"  # scripted group (container) (typed FeaturePython)
  n = 2
  ref = O_element
FEATURE [App::DocumentObjectGroupPython] G4_CARBON_DIOXIDE  # scripted group (container) (typed FeaturePython)
  Dunit = g/cm3
  Dvalue = 0.00184212
  Group = -> [C_element023,O_element025]
  conduct = 2
  density = 1
  expand = 3
  formula = G4_CARBON_DIOXIDE
  name = G4_CARBON_DIOXIDE
  specific = 4
FEATURE [App::DocumentObjectGroupPython] C_element024  label="C_element : 011"  # scripted group (container) (typed FeaturePython)
  n = 1
  ref = C_element
FEATURE [App::DocumentObjectGroupPython] Cl_element004  label="Cl_element : 4"  # scripted group (container) (typed FeaturePython)
  n = 4
  ref = Cl_element
FEATURE [App::DocumentObjectGroupPython] G4_CARBON_TETRACHLORIDE  # scripted group (container) (typed FeaturePython)
  Dunit = g/cm3
  Dvalue = 1.594
  Group = -> [C_element024,Cl_element004]
  conduct = 2
  density = 1
  expand = 3
  formula = G4_CARBON_TETRACHLORIDE
  name = G4_CARBON_TETRACHLORIDE
  specific = 4
FEATURE [App::DocumentObjectGroupPython] C_element025  label="C_element : 012"  # scripted group (container) (typed FeaturePython)
  n = 6
  ref = C_element
FEATURE [App::DocumentObjectGroupPython] H_element021  label="H_element : 012"  # scripted group (container) (typed FeaturePython)
  n = 10
  ref = H_element
FEATURE [App::DocumentObjectGroupPython] O_element026  label="O_element : 5"  # scripted group (container) (typed FeaturePython)
  n = 5
  ref = O_element
FEATURE [App::DocumentObjectGroupPython] G4_CELLULOSE_CELLOPHANE  # scripted group (container) (typed FeaturePython)
  Dunit = g/cm3
  Dvalue = 1.42
  Group = -> [C_element025,H_element021,O_element026]
  conduct = 2
  density = 1
  expand = 3
  formula = G4_CELLULOSE_CELLOPHANE
  name = G4_CELLULOSE_CELLOPHANE
  specific = 4
FEATURE [App::DocumentObjectGroupPython] H_element022  label="H_element : 0.067"  # scripted group (container) (typed FeaturePython)
  n = 0.067125
FEATURE [App::DocumentObjectGroupPython] C_element026  label="C_element : 0.545"  # scripted group (container) (typed FeaturePython)
  n = 0.545403
FEATURE [App::DocumentObjectGroupPython] O_element027  label="O_element : 0.387"  # scripted group (container) (typed FeaturePython)
  n = 0.387472
FEATURE [App::DocumentObjectGroupPython] G4_CELLULOSE_BUTYRATE  # scripted group (container) (typed FeaturePython)
  Dunit = g/cm3
  Dvalue = 1.2
  Group = -> [H_element022,C_element026,O_element027]
  conduct = 2
  density = 1
  expand = 3
  formula = G4_CELLULOSE_BUTYRATE
  name = G4_CELLULOSE_BUTYRATE
  specific = 4
FEATURE [App::DocumentObjectGroupPython] H_element023  label="H_element : 0.029"  # scripted group (container) (typed FeaturePython)
  n = 0.029216
FEATURE [App::DocumentObjectGroupPython] C_element027  label="C_element : 0.271"  # scripted group (container) (typed FeaturePython)
  n = 0.271296
FEATURE [App::DocumentObjectGroupPython] N_element013  label="N_element : 0.121"  # scripted group (container) (typed FeaturePython)
  n = 0.121276
FEATURE [App::DocumentObjectGroupPython] O_element028  label="O_element : 0.578"  # scripted group (container) (typed FeaturePython)
  n = 0.578212
FEATURE [App::DocumentObjectGroupPython] G4_CELLULOSE_NITRATE  # scripted group (container) (typed FeaturePython)
  Dunit = g/cm3
  Dvalue = 1.49
  Group = -> [H_element023,C_element027,N_element013,O_element028]
  conduct = 2
  density = 1
  expand = 3
  formula = G4_CELLULOSE_NITRATE
  name = G4_CELLULOSE_NITRATE
  specific = 4
FEATURE [App::DocumentObjectGroupPython] H_element024  label="H_element : 0.108"  # scripted group (container) (typed FeaturePython)
  n = 0.107596
FEATURE [App::DocumentObjectGroupPython] N_element014  label="N_element : 0.001"  # scripted group (container) (typed FeaturePython)
  n = 0.0008
FEATURE [App::DocumentObjectGroupPython] O_element029  label="O_element : 0.875"  # scripted group (container) (typed FeaturePython)
  n = 0.874976
FEATURE [App::DocumentObjectGroupPython] S_element008  label="S_element : 0.015"  # scripted group (container) (typed FeaturePython)
  n = 0.014627
FEATURE [App::DocumentObjectGroupPython] Ce_element001  label="Ce_element : 0.002"  # scripted group (container) (typed FeaturePython)
  n = 0.002001
FEATURE [App::DocumentObjectGroupPython] G4_CERIC_SULFATE  # scripted group (container) (typed FeaturePython)
  Dunit = g/cm3
  Dvalue = 1.03
  Group = -> [H_element024,N_element014,O_element029,S_element008,Ce_element001]
  conduct = 2
  density = 1
  expand = 3
  formula = G4_CERIC_SULFATE
  name = G4_CERIC_SULFATE
  specific = 4
FEATURE [App::DocumentObjectGroupPython] Cs_element001  label="Cs_element : 1"  # scripted group (container) (typed FeaturePython)
  n = 1
  ref = Cs_element
FEATURE [App::DocumentObjectGroupPython] F_element006  label="F_element : 1"  # scripted group (container) (typed FeaturePython)
  n = 1
  ref = F_element
FEATURE [App::DocumentObjectGroupPython] G4_CESIUM_FLUORIDE  # scripted group (container) (typed FeaturePython)
  Dunit = g/cm3
  Dvalue = 4.115
  Group = -> [Cs_element001,F_element006]
  conduct = 2
  density = 1
  expand = 3
  formula = G4_CESIUM_FLUORIDE
  name = G4_CESIUM_FLUORIDE
  specific = 4
FEATURE [App::DocumentObjectGroupPython] Cs_element002  label="Cs_element : 002"  # scripted group (container) (typed FeaturePython)
  n = 1
  ref = Cs_element
FEATURE [App::DocumentObjectGroupPython] I_element001  label="I_element : 1"  # scripted group (container) (typed FeaturePython)
  n = 1
  ref = I_element
FEATURE [App::DocumentObjectGroupPython] G4_CESIUM_IODIDE  # scripted group (container) (typed FeaturePython)
  Dunit = g/cm3
  Dvalue = 4.51
  Group = -> [Cs_element002,I_element001]
  conduct = 2
  density = 1
  expand = 3
  formula = G4_CESIUM_IODIDE
  name = G4_CESIUM_IODIDE
  specific = 4
FEATURE [App::DocumentObjectGroupPython] C_element028  label="C_element : 013"  # scripted group (container) (typed FeaturePython)
  n = 6
  ref = C_element
FEATURE [App::DocumentObjectGroupPython] H_element025  label="H_element : 013"  # scripted group (container) (typed FeaturePython)
  n = 5
  ref = H_element
FEATURE [App::DocumentObjectGroupPython] Cl_element005  label="Cl_element : 1"  # scripted group (container) (typed FeaturePython)
  n = 1
  ref = Cl_element
FEATURE [App::DocumentObjectGroupPython] G4_CHLOROBENZENE  # scripted group (container) (typed FeaturePython)
  Dunit = g/cm3
  Dvalue = 1.1058
  Group = -> [C_element028,H_element025,Cl_element005]
  conduct = 2
  density = 1
  expand = 3
  formula = G4_CHLOROBENZENE
  name = G4_CHLOROBENZENE
  specific = 4
FEATURE [App::DocumentObjectGroupPython] C_element029  label="C_element : 014"  # scripted group (container) (typed FeaturePython)
  n = 1
  ref = C_element
FEATURE [App::DocumentObjectGroupPython] H_element026  label="H_element : 1"  # scripted group (container) (typed FeaturePython)
  n = 1
  ref = H_element
FEATURE [App::DocumentObjectGroupPython] Cl_element006  label="Cl_element : 3"  # scripted group (container) (typed FeaturePython)
  n = 3
  ref = Cl_element
FEATURE [App::DocumentObjectGroupPython] G4_CHLOROFORM  # scripted group (container) (typed FeaturePython)
  Dunit = g/cm3
  Dvalue = 1.4832
  Group = -> [C_element029,H_element026,Cl_element006]
  conduct = 2
  density = 1
  expand = 3
  formula = G4_CHLOROFORM
  name = G4_CHLOROFORM
  specific = 4
FEATURE [App::DocumentObjectGroupPython] H_element027  label="H_element : 0.010"  # scripted group (container) (typed FeaturePython)
  n = 0.01
FEATURE [App::DocumentObjectGroupPython] C_element030  label="C_element : 0.001"  # scripted group (container) (typed FeaturePython)
  n = 0.001
FEATURE [App::DocumentObjectGroupPython] O_element030  label="O_element : 0.529"  # scripted group (container) (typed FeaturePython)
  n = 0.529107
FEATURE [App::DocumentObjectGroupPython] Na_element005  label="Na_element : 0.016"  # scripted group (container) (typed FeaturePython)
  n = 0.016
FEATURE [App::DocumentObjectGroupPython] Mg_element003  label="Mg_element : 0.004"  # scripted group (container) (typed FeaturePython)
  n = 0.002
FEATURE [App::DocumentObjectGroupPython] Al_element002  label="Al_element : 0.034"  # scripted group (container) (typed FeaturePython)
  n = 0.033872
FEATURE [App::DocumentObjectGroupPython] Si_element002  label="Si_element : 0.337"  # scripted group (container) (typed FeaturePython)
  n = 0.337021
FEATURE [App::DocumentObjectGroupPython] K_element003  label="K_element : 0.013"  # scripted group (container) (typed FeaturePython)
  n = 0.013
FEATURE [App::DocumentObjectGroupPython] Ca_element010  label="Ca_element : 0.044"  # scripted group (container) (typed FeaturePython)
  n = 0.044
FEATURE [App::DocumentObjectGroupPython] Fe_element002  label="Fe_element : 0.014"  # scripted group (container) (typed FeaturePython)
  n = 0.014
FEATURE [App::DocumentObjectGroupPython] G4_CONCRETE  # scripted group (container) (typed FeaturePython)
  Dunit = g/cm3
  Dvalue = 2.3
  Group = -> [H_element027,C_element030,O_element030,Na_element005,Mg_element003,Al_element002,Si_element002,K_element003,Ca_element010,Fe_element002]
  conduct = 2
  density = 1
  expand = 3
  formula = G4_CONCRETE
  name = G4_CONCRETE
  specific = 4
FEATURE [App::DocumentObjectGroupPython] C_element031  label="C_element : 015"  # scripted group (container) (typed FeaturePython)
  n = 6
  ref = C_element
FEATURE [App::DocumentObjectGroupPython] H_element028  label="H_element : 12"  # scripted group (container) (typed FeaturePython)
  n = 12
  ref = H_element
FEATURE [App::DocumentObjectGroupPython] G4_CYCLOHEXANE  # scripted group (container) (typed FeaturePython)
  Dunit = g/cm3
  Dvalue = 0.779
  Group = -> [C_element031,H_element028]
  conduct = 2
  density = 1
  expand = 3
  formula = G4_CYCLOHEXANE
  name = G4_CYCLOHEXANE
  specific = 4
FEATURE [App::DocumentObjectGroupPython] C_element032  label="C_element : 016"  # scripted group (container) (typed FeaturePython)
  n = 6
  ref = C_element
FEATURE [App::DocumentObjectGroupPython] H_element029  label="H_element : 4"  # scripted group (container) (typed FeaturePython)
  n = 4
  ref = H_element
FEATURE [App::DocumentObjectGroupPython] Cl_element007  label="Cl_element : 2"  # scripted group (container) (typed FeaturePython)
  n = 2
  ref = Cl_element
FEATURE [App::DocumentObjectGroupPython] G4_1_2_DICHLOROBENZENE  label="G4_1.2-DICHLOROBENZENE"  # scripted group (container) (typed FeaturePython)
  Dunit = g/cm3
  Dvalue = 1.3048
  Group = -> [C_element032,H_element029,Cl_element007]
  conduct = 2
  density = 1
  expand = 3
  formula = G4_1.2-DICHLOROBENZENE
  name = G4_1.2-DICHLOROBENZENE
  specific = 4
FEATURE [App::DocumentObjectGroupPython] C_element033  label="C_element : 017"  # scripted group (container) (typed FeaturePython)
  n = 4
  ref = C_element
FEATURE [App::DocumentObjectGroupPython] H_element030  label="H_element : 8"  # scripted group (container) (typed FeaturePython)
  n = 8
  ref = H_element
FEATURE [App::DocumentObjectGroupPython] O_element031  label="O_element : 014"  # scripted group (container) (typed FeaturePython)
  n = 1
  ref = O_element
FEATURE [App::DocumentObjectGroupPython] Cl_element008  label="Cl_element : 005"  # scripted group (container) (typed FeaturePython)
  n = 2
  ref = Cl_element
FEATURE [App::DocumentObjectGroupPython] G4_DICHLORODIETHYL_ETHER  # scripted group (container) (typed FeaturePython)
  Dunit = g/cm3
  Dvalue = 1.2199
  Group = -> [C_element033,H_element030,O_element031,Cl_element008]
  conduct = 2
  density = 1
  expand = 3
  formula = G4_DICHLORODIETHYL_ETHER
  name = G4_DICHLORODIETHYL_ETHER
  specific = 4
FEATURE [App::DocumentObjectGroupPython] C_element034  label="C_element : 018"  # scripted group (container) (typed FeaturePython)
  n = 2
  ref = C_element
FEATURE [App::DocumentObjectGroupPython] H_element031  label="H_element : 014"  # scripted group (container) (typed FeaturePython)
  n = 4
  ref = H_element
FEATURE [App::DocumentObjectGroupPython] Cl_element009  label="Cl_element : 006"  # scripted group (container) (typed FeaturePython)
  n = 2
  ref = Cl_element
FEATURE [App::DocumentObjectGroupPython] G4_1_2_DICHLOROETHANE  label="G4_1.2-DICHLOROETHANE"  # scripted group (container) (typed FeaturePython)
  Dunit = g/cm3
  Dvalue = 1.2351
  Group = -> [C_element034,H_element031,Cl_element009]
  conduct = 2
  density = 1
  expand = 3
  formula = G4_1.2-DICHLOROETHANE
  name = G4_1.2-DICHLOROETHANE
  specific = 4
FEATURE [App::DocumentObjectGroupPython] C_element035  label="C_element : 019"  # scripted group (container) (typed FeaturePython)
  n = 4
  ref = C_element
FEATURE [App::DocumentObjectGroupPython] H_element032  label="H_element : 015"  # scripted group (container) (typed FeaturePython)
  n = 10
  ref = H_element
FEATURE [App::DocumentObjectGroupPython] O_element032  label="O_element : 015"  # scripted group (container) (typed FeaturePython)
  n = 1
  ref = O_element
FEATURE [App::DocumentObjectGroupPython] G4_DIETHYL_ETHER  # scripted group (container) (typed FeaturePython)
  Dunit = g/cm3
  Dvalue = 0.71378
  Group = -> [C_element035,H_element032,O_element032]
  conduct = 2
  density = 1
  expand = 3
  formula = G4_DIETHYL_ETHER
  name = G4_DIETHYL_ETHER
  specific = 4
FEATURE [App::DocumentObjectGroupPython] C_element036  label="C_element : 020"  # scripted group (container) (typed FeaturePython)
  n = 3
  ref = C_element
FEATURE [App::DocumentObjectGroupPython] H_element033  label="H_element : 016"  # scripted group (container) (typed FeaturePython)
  n = 7
  ref = H_element
FEATURE [App::DocumentObjectGroupPython] N_element015  label="N_element : 008"  # scripted group (container) (typed FeaturePython)
  n = 1
  ref = N_element
FEATURE [App::DocumentObjectGroupPython] O_element033  label="O_element : 016"  # scripted group (container) (typed FeaturePython)
  n = 1
  ref = O_element
FEATURE [App::DocumentObjectGroupPython] G4_N_N_DIMETHYL_FORMAMIDE  label="G4_N.N-DIMETHYL_FORMAMIDE"  # scripted group (container) (typed FeaturePython)
  Dunit = g/cm3
  Dvalue = 0.9487
  Group = -> [C_element036,H_element033,N_element015,O_element033]
  conduct = 2
  density = 1
  expand = 3
  formula = G4_N.N-DIMETHYL_FORMAMIDE
  name = G4_N.N-DIMETHYL_FORMAMIDE
  specific = 4
FEATURE [App::DocumentObjectGroupPython] C_element037  label="C_element : 021"  # scripted group (container) (typed FeaturePython)
  n = 2
  ref = C_element
FEATURE [App::DocumentObjectGroupPython] H_element034  label="H_element : 017"  # scripted group (container) (typed FeaturePython)
  n = 6
  ref = H_element
FEATURE [App::DocumentObjectGroupPython] O_element034  label="O_element : 017"  # scripted group (container) (typed FeaturePython)
  n = 1
  ref = O_element
FEATURE [App::DocumentObjectGroupPython] S_element009  label="S_element : 003"  # scripted group (container) (typed FeaturePython)
  n = 1
  ref = S_element
FEATURE [App::DocumentObjectGroupPython] G4_DIMETHYL_SULFOXIDE  # scripted group (container) (typed FeaturePython)
  Dunit = g/cm3
  Dvalue = 1.1014
  Group = -> [C_element037,H_element034,O_element034,S_element009]
  conduct = 2
  density = 1
  expand = 3
  formula = G4_DIMETHYL_SULFOXIDE
  name = G4_DIMETHYL_SULFOXIDE
  specific = 4
FEATURE [App::DocumentObjectGroupPython] C_element038  label="C_element : 022"  # scripted group (container) (typed FeaturePython)
  n = 2
  ref = C_element
FEATURE [App::DocumentObjectGroupPython] H_element035  label="H_element : 018"  # scripted group (container) (typed FeaturePython)
  n = 6
  ref = H_element
FEATURE [App::DocumentObjectGroupPython] G4_ETHANE  # scripted group (container) (typed FeaturePython)
  Dunit = g/cm3
  Dvalue = 0.00125324
  Group = -> [C_element038,H_element035]
  conduct = 2
  density = 1
  expand = 3
  formula = G4_ETHANE
  name = G4_ETHANE
  specific = 4
FEATURE [App::DocumentObjectGroupPython] C_element039  label="C_element : 023"  # scripted group (container) (typed FeaturePython)
  n = 2
  ref = C_element
FEATURE [App::DocumentObjectGroupPython] H_element036  label="H_element : 019"  # scripted group (container) (typed FeaturePython)
  n = 6
  ref = H_element
FEATURE [App::DocumentObjectGroupPython] O_element035  label="O_element : 018"  # scripted group (container) (typed FeaturePython)
  n = 1
  ref = O_element
FEATURE [App::DocumentObjectGroupPython] G4_ETHYL_ALCOHOL  # scripted group (container) (typed FeaturePython)
  Dunit = g/cm3
  Dvalue = 0.7893
  Group = -> [C_element039,H_element036,O_element035]
  conduct = 2
  density = 1
  expand = 3
  formula = G4_ETHYL_ALCOHOL
  name = G4_ETHYL_ALCOHOL
  specific = 4
FEATURE [App::DocumentObjectGroupPython] H_element037  label="H_element : 0.090"  # scripted group (container) (typed FeaturePython)
  n = 0.090027
FEATURE [App::DocumentObjectGroupPython] C_element040  label="C_element : 0.585"  # scripted group (container) (typed FeaturePython)
  n = 0.585182
FEATURE [App::DocumentObjectGroupPython] O_element036  label="O_element : 0.325"  # scripted group (container) (typed FeaturePython)
  n = 0.324791
FEATURE [App::DocumentObjectGroupPython] G4_ETHYL_CELLULOSE  # scripted group (container) (typed FeaturePython)
  Dunit = g/cm3
  Dvalue = 1.13
  Group = -> [H_element037,C_element040,O_element036]
  conduct = 2
  density = 1
  expand = 3
  formula = G4_ETHYL_CELLULOSE
  name = G4_ETHYL_CELLULOSE
  specific = 4
FEATURE [App::DocumentObjectGroupPython] C_element041  label="C_element : 024"  # scripted group (container) (typed FeaturePython)
  n = 2
  ref = C_element
FEATURE [App::DocumentObjectGroupPython] H_element038  label="H_element : 020"  # scripted group (container) (typed FeaturePython)
  n = 4
  ref = H_element
FEATURE [App::DocumentObjectGroupPython] G4_ETHYLENE  # scripted group (container) (typed FeaturePython)
  Dunit = g/cm3
  Dvalue = 0.00117497
  Group = -> [C_element041,H_element038]
  conduct = 2
  density = 1
  expand = 3
  formula = G4_ETHYLENE
  name = G4_ETHYLENE
  specific = 4
FEATURE [App::DocumentObjectGroupPython] H_element039  label="H_element : 0.096"  # scripted group (container) (typed FeaturePython)
  n = 0.096
FEATURE [App::DocumentObjectGroupPython] C_element042  label="C_element : 0.195"  # scripted group (container) (typed FeaturePython)
  n = 0.195
FEATURE [App::DocumentObjectGroupPython] N_element016  label="N_element : 0.057"  # scripted group (container) (typed FeaturePython)
  n = 0.057
FEATURE [App::DocumentObjectGroupPython] O_element037  label="O_element : 0.646"  # scripted group (container) (typed FeaturePython)
  n = 0.646
FEATURE [App::DocumentObjectGroupPython] Na_element006  label="Na_element : 0.017"  # scripted group (container) (typed FeaturePython)
  n = 0.001
FEATURE [App::DocumentObjectGroupPython] P_element005  label="P_element : 0.104"  # scripted group (container) (typed FeaturePython)
  n = 0.001
FEATURE [App::DocumentObjectGroupPython] S_element010  label="S_element : 0.016"  # scripted group (container) (typed FeaturePython)
  n = 0.003
FEATURE [App::DocumentObjectGroupPython] Cl_element010  label="Cl_element : 0.005"  # scripted group (container) (typed FeaturePython)
  n = 0.001
FEATURE [App::DocumentObjectGroupPython] G4_EYE_LENS_ICRP  # scripted group (container) (typed FeaturePython)
  Dunit = g/cm3
  Dvalue = 1.07
  Group = -> [H_element039,C_element042,N_element016,O_element037,Na_element006,P_element005,S_element010,Cl_element010]
  conduct = 2
  density = 1
  expand = 3
  formula = G4_EYE_LENS_ICRP
  name = G4_EYE_LENS_ICRP
  specific = 4
FEATURE [App::DocumentObjectGroupPython] Fe_element003  label="Fe_element : 2"  # scripted group (container) (typed FeaturePython)
  n = 2
  ref = Fe_element
FEATURE [App::DocumentObjectGroupPython] O_element038  label="O_element : 019"  # scripted group (container) (typed FeaturePython)
  n = 3
  ref = O_element
FEATURE [App::DocumentObjectGroupPython] G4_FERRIC_OXIDE  # scripted group (container) (typed FeaturePython)
  Dunit = g/cm3
  Dvalue = 5.2
  Group = -> [Fe_element003,O_element038]
  conduct = 2
  density = 1
  expand = 3
  formula = G4_FERRIC_OXIDE
  name = G4_FERRIC_OXIDE
  specific = 4
FEATURE [App::DocumentObjectGroupPython] Fe_element004  label="Fe_element : 1"  # scripted group (container) (typed FeaturePython)
  n = 1
  ref = Fe_element
FEATURE [App::DocumentObjectGroupPython] B_element003  label="B_element : 1"  # scripted group (container) (typed FeaturePython)
  n = 1
  ref = B_element
FEATURE [App::DocumentObjectGroupPython] G4_FERROBORIDE  # scripted group (container) (typed FeaturePython)
  Dunit = g/cm3
  Dvalue = 7.15
  Group = -> [Fe_element004,B_element003]
  conduct = 2
  density = 1
  expand = 3
  formula = G4_FERROBORIDE
  name = G4_FERROBORIDE
  specific = 4
FEATURE [App::DocumentObjectGroupPython] Fe_element005  label="Fe_element : 003"  # scripted group (container) (typed FeaturePython)
  n = 1
  ref = Fe_element
FEATURE [App::DocumentObjectGroupPython] O_element039  label="O_element : 020"  # scripted group (container) (typed FeaturePython)
  n = 1
  ref = O_element
FEATURE [App::DocumentObjectGroupPython] G4_FERROUS_OXIDE  # scripted group (container) (typed FeaturePython)
  Dunit = g/cm3
  Dvalue = 5.7
  Group = -> [Fe_element005,O_element039]
  conduct = 2
  density = 1
  expand = 3
  formula = G4_FERROUS_OXIDE
  name = G4_FERROUS_OXIDE
  specific = 4
FEATURE [App::DocumentObjectGroupPython] H_element040  label="H_element : 0.115"  # scripted group (container) (typed FeaturePython)
  n = 0.108259
FEATURE [App::DocumentObjectGroupPython] N_element017  label="N_element : 0.000"  # scripted group (container) (typed FeaturePython)
  n = 2.7e-05
FEATURE [App::DocumentObjectGroupPython] O_element040  label="O_element : 0.879"  # scripted group (container) (typed FeaturePython)
  n = 0.878636
FEATURE [App::DocumentObjectGroupPython] Na_element007  label="Na_element : 0.000"  # scripted group (container) (typed FeaturePython)
  n = 2.2e-05
FEATURE [App::DocumentObjectGroupPython] S_element011  label="S_element : 0.013"  # scripted group (container) (typed FeaturePython)
  n = 0.012968
FEATURE [App::DocumentObjectGroupPython] Cl_element011  label="Cl_element : 0.000"  # scripted group (container) (typed FeaturePython)
  n = 3.4e-05
FEATURE [App::DocumentObjectGroupPython] Fe_element006  label="Fe_element : 0.000"  # scripted group (container) (typed FeaturePython)
  n = 5.4e-05
FEATURE [App::DocumentObjectGroupPython] G4_FERROUS_SULFATE  # scripted group (container) (typed FeaturePython)
  Dunit = g/cm3
  Dvalue = 1.024
  Group = -> [H_element040,N_element017,O_element040,Na_element007,S_element011,Cl_element011,Fe_element006]
  conduct = 2
  density = 1
  expand = 3
  formula = G4_FERROUS_SULFATE
  name = G4_FERROUS_SULFATE
  specific = 4
FEATURE [App::DocumentObjectGroupPython] C_element043  label="C_element : 0.099"  # scripted group (container) (typed FeaturePython)
  n = 0.099335
FEATURE [App::DocumentObjectGroupPython] F_element007  label="F_element : 0.314"  # scripted group (container) (typed FeaturePython)
  n = 0.314247
FEATURE [App::DocumentObjectGroupPython] Cl_element012  label="Cl_element : 0.586"  # scripted group (container) (typed FeaturePython)
  n = 0.586418
FEATURE [App::DocumentObjectGroupPython] G4_FREON_12  label="G4_FREON-12"  # scripted group (container) (typed FeaturePython)
  Dunit = g/cm3
  Dvalue = 1.12
  Group = -> [C_element043,F_element007,Cl_element012]
  conduct = 2
  density = 1
  expand = 3
  formula = G4_FREON-12
  name = G4_FREON-12
  specific = 4
FEATURE [App::DocumentObjectGroupPython] C_element044  label="C_element : 0.057"  # scripted group (container) (typed FeaturePython)
  n = 0.057245
FEATURE [App::DocumentObjectGroupPython] F_element008  label="F_element : 0.181"  # scripted group (container) (typed FeaturePython)
  n = 0.181096
FEATURE [App::DocumentObjectGroupPython] Br_element001  label="Br_element : 0.762"  # scripted group (container) (typed FeaturePython)
  n = 0.761659
FEATURE [App::DocumentObjectGroupPython] G4_FREON_12B2  label="G4_FREON-12B2"  # scripted group (container) (typed FeaturePython)
  Dunit = g/cm3
  Dvalue = 1.8
  Group = -> [C_element044,F_element008,Br_element001]
  conduct = 2
  density = 1
  expand = 3
  formula = G4_FREON-12B2
  name = G4_FREON-12B2
  specific = 4
FEATURE [App::DocumentObjectGroupPython] C_element045  label="C_element : 0.115"  # scripted group (container) (typed FeaturePython)
  n = 0.114983
FEATURE [App::DocumentObjectGroupPython] F_element009  label="F_element : 0.546"  # scripted group (container) (typed FeaturePython)
  n = 0.545621
FEATURE [App::DocumentObjectGroupPython] Cl_element013  label="Cl_element : 0.339"  # scripted group (container) (typed FeaturePython)
  n = 0.339396
FEATURE [App::DocumentObjectGroupPython] G4_FREON_13  label="G4_FREON-13"  # scripted group (container) (typed FeaturePython)
  Dunit = g/cm3
  Dvalue = 0.95
  Group = -> [C_element045,F_element009,Cl_element013]
  conduct = 2
  density = 1
  expand = 3
  formula = G4_FREON-13
  name = G4_FREON-13
  specific = 4
FEATURE [App::DocumentObjectGroupPython] C_element046  label="C_element : 025"  # scripted group (container) (typed FeaturePython)
  n = 1
  ref = C_element
FEATURE [App::DocumentObjectGroupPython] F_element010  label="F_element : 3"  # scripted group (container) (typed FeaturePython)
  n = 3
  ref = F_element
FEATURE [App::DocumentObjectGroupPython] Br_element002  label="Br_element : 1"  # scripted group (container) (typed FeaturePython)
  n = 1
  ref = Br_element
FEATURE [App::DocumentObjectGroupPython] G4_FREON_13B1  label="G4_FREON-13B1"  # scripted group (container) (typed FeaturePython)
  Dunit = g/cm3
  Dvalue = 1.5
  Group = -> [C_element046,F_element010,Br_element002]
  conduct = 2
  density = 1
  expand = 3
  formula = G4_FREON-13B1
  name = G4_FREON-13B1
  specific = 4
FEATURE [App::DocumentObjectGroupPython] C_element047  label="C_element : 0.061"  # scripted group (container) (typed FeaturePython)
  n = 0.061309
FEATURE [App::DocumentObjectGroupPython] F_element011  label="F_element : 0.291"  # scripted group (container) (typed FeaturePython)
  n = 0.290924
FEATURE [App::DocumentObjectGroupPython] I_element002  label="I_element : 0.648"  # scripted group (container) (typed FeaturePython)
  n = 0.647767
FEATURE [App::DocumentObjectGroupPython] G4_FREON_13I1  label="G4_FREON-13I1"  # scripted group (container) (typed FeaturePython)
  Dunit = g/cm3
  Dvalue = 1.8
  Group = -> [C_element047,F_element011,I_element002]
  conduct = 2
  density = 1
  expand = 3
  formula = G4_FREON-13I1
  name = G4_FREON-13I1
  specific = 4
FEATURE [App::DocumentObjectGroupPython] Gd_element001  label="Gd_element : 2"  # scripted group (container) (typed FeaturePython)
  n = 2
  ref = Gd_element
FEATURE [App::DocumentObjectGroupPython] O_element041  label="O_element : 021"  # scripted group (container) (typed FeaturePython)
  n = 2
  ref = O_element
FEATURE [App::DocumentObjectGroupPython] S_element012  label="S_element : 004"  # scripted group (container) (typed FeaturePython)
  n = 1
  ref = S_element
FEATURE [App::DocumentObjectGroupPython] G4_GADOLINIUM_OXYSULFIDE  # scripted group (container) (typed FeaturePython)
  Dunit = g/cm3
  Dvalue = 7.44
  Group = -> [Gd_element001,O_element041,S_element012]
  conduct = 2
  density = 1
  expand = 3
  formula = G4_GADOLINIUM_OXYSULFIDE
  name = G4_GADOLINIUM_OXYSULFIDE
  specific = 4
FEATURE [App::DocumentObjectGroupPython] Ga_element001  label="Ga_element : 1"  # scripted group (container) (typed FeaturePython)
  n = 1
  ref = Ga_element
FEATURE [App::DocumentObjectGroupPython] As_element001  label="As_element : 1"  # scripted group (container) (typed FeaturePython)
  n = 1
  ref = As_element
FEATURE [App::DocumentObjectGroupPython] G4_GALLIUM_ARSENIDE  # scripted group (container) (typed FeaturePython)
  Dunit = g/cm3
  Dvalue = 5.31
  Group = -> [Ga_element001,As_element001]
  conduct = 2
  density = 1
  expand = 3
  formula = G4_GALLIUM_ARSENIDE
  name = G4_GALLIUM_ARSENIDE
  specific = 4
FEATURE [App::DocumentObjectGroupPython] H_element041  label="H_element : 0.081"  # scripted group (container) (typed FeaturePython)
  n = 0.08118
FEATURE [App::DocumentObjectGroupPython] C_element048  label="C_element : 0.416"  # scripted group (container) (typed FeaturePython)
  n = 0.41606
FEATURE [App::DocumentObjectGroupPython] N_element018  label="N_element : 0.111"  # scripted group (container) (typed FeaturePython)
  n = 0.11124
FEATURE [App::DocumentObjectGroupPython] O_element042  label="O_element : 0.381"  # scripted group (container) (typed FeaturePython)
  n = 0.38064
FEATURE [App::DocumentObjectGroupPython] S_element013  label="S_element : 0.011"  # scripted group (container) (typed FeaturePython)
  n = 0.01088
FEATURE [App::DocumentObjectGroupPython] G4_GEL_PHOTO_EMULSION  # scripted group (container) (typed FeaturePython)
  Dunit = g/cm3
  Dvalue = 1.2914
  Group = -> [H_element041,C_element048,N_element018,O_element042,S_element013]
  conduct = 2
  density = 1
  expand = 3
  formula = G4_GEL_PHOTO_EMULSION
  name = G4_GEL_PHOTO_EMULSION
  specific = 4
FEATURE [App::DocumentObjectGroupPython] B_element004  label="B_element : 0.040"  # scripted group (container) (typed FeaturePython)
  n = 0.0400639
FEATURE [App::DocumentObjectGroupPython] O_element043  label="O_element : 0.540"  # scripted group (container) (typed FeaturePython)
  n = 0.539561
FEATURE [App::DocumentObjectGroupPython] Na_element008  label="Na_element : 0.028"  # scripted group (container) (typed FeaturePython)
  n = 0.0281909
FEATURE [App::DocumentObjectGroupPython] Al_element003  label="Al_element : 0.012"  # scripted group (container) (typed FeaturePython)
  n = 0.011644
FEATURE [App::DocumentObjectGroupPython] Si_element003  label="Si_element : 0.377"  # scripted group (container) (typed FeaturePython)
  n = 0.377219
FEATURE [App::DocumentObjectGroupPython] K_element004  label="K_element : 0.014"  # scripted group (container) (typed FeaturePython)
  n = 0.00332099
FEATURE [App::DocumentObjectGroupPython] G4_Pyrex_Glass  # scripted group (container) (typed FeaturePython)
  Dunit = g/cm3
  Dvalue = 2.23
  Group = -> [B_element004,O_element043,Na_element008,Al_element003,Si_element003,K_element004]
  conduct = 2
  density = 1
  expand = 3
  formula = G4_Pyrex_Glass
  name = G4_Pyrex_Glass
  specific = 4
FEATURE [App::DocumentObjectGroupPython] O_element044  label="O_element : 0.156"  # scripted group (container) (typed FeaturePython)
  n = 0.156453
FEATURE [App::DocumentObjectGroupPython] Si_element004  label="Si_element : 0.081"  # scripted group (container) (typed FeaturePython)
  n = 0.080866
FEATURE [App::DocumentObjectGroupPython] Ti_element001  label="Ti_element : 0.008"  # scripted group (container) (typed FeaturePython)
  n = 0.008092
FEATURE [App::DocumentObjectGroupPython] As_element002  label="As_element : 0.003"  # scripted group (container) (typed FeaturePython)
  n = 0.002651
FEATURE [App::DocumentObjectGroupPython] Pb_element001  label="Pb_element : 0.752"  # scripted group (container) (typed FeaturePython)
  n = 0.751938
FEATURE [App::DocumentObjectGroupPython] G4_GLASS_LEAD  # scripted group (container) (typed FeaturePython)
  Dunit = g/cm3
  Dvalue = 6.22
  Group = -> [O_element044,Si_element004,Ti_element001,As_element002,Pb_element001]
  conduct = 2
  density = 1
  expand = 3
  formula = G4_GLASS_LEAD
  name = G4_GLASS_LEAD
  specific = 4
FEATURE [App::DocumentObjectGroupPython] O_element045  label="O_element : 0.460"  # scripted group (container) (typed FeaturePython)
  n = 0.4598
FEATURE [App::DocumentObjectGroupPython] Na_element009  label="Na_element : 0.096"  # scripted group (container) (typed FeaturePython)
  n = 0.0964411
FEATURE [App::DocumentObjectGroupPython] Si_element005  label="Si_element : 0.378"  # scripted group (container) (typed FeaturePython)
  n = 0.336553
FEATURE [App::DocumentObjectGroupPython] Ca_element011  label="Ca_element : 0.107"  # scripted group (container) (typed FeaturePython)
  n = 0.107205
FEATURE [App::DocumentObjectGroupPython] G4_GLASS_PLATE  # scripted group (container) (typed FeaturePython)
  Dunit = g/cm3
  Dvalue = 2.4
  Group = -> [O_element045,Na_element009,Si_element005,Ca_element011]
  conduct = 2
  density = 1
  expand = 3
  formula = G4_GLASS_PLATE
  name = G4_GLASS_PLATE
  specific = 4
FEATURE [App::DocumentObjectGroupPython] C_element049  label="C_element : 026"  # scripted group (container) (typed FeaturePython)
  n = 5
  ref = C_element
FEATURE [App::DocumentObjectGroupPython] H_element042  label="H_element : 021"  # scripted group (container) (typed FeaturePython)
  n = 10
  ref = H_element
FEATURE [App::DocumentObjectGroupPython] N_element019  label="N_element : 2"  # scripted group (container) (typed FeaturePython)
  n = 2
  ref = N_element
FEATURE [App::DocumentObjectGroupPython] O_element046  label="O_element : 022"  # scripted group (container) (typed FeaturePython)
  n = 3
  ref = O_element
FEATURE [App::DocumentObjectGroupPython] G4_GLUTAMINE  # scripted group (container) (typed FeaturePython)
  Dunit = g/cm3
  Dvalue = 1.46
  Group = -> [C_element049,H_element042,N_element019,O_element046]
  conduct = 2
  density = 1
  expand = 3
  formula = G4_GLUTAMINE
  name = G4_GLUTAMINE
  specific = 4
FEATURE [App::DocumentObjectGroupPython] C_element050  label="C_element : 027"  # scripted group (container) (typed FeaturePython)
  n = 3
  ref = C_element
FEATURE [App::DocumentObjectGroupPython] H_element043  label="H_element : 022"  # scripted group (container) (typed FeaturePython)
  n = 8
  ref = H_element
FEATURE [App::DocumentObjectGroupPython] O_element047  label="O_element : 023"  # scripted group (container) (typed FeaturePython)
  n = 3
  ref = O_element
FEATURE [App::DocumentObjectGroupPython] G4_GLYCEROL  # scripted group (container) (typed FeaturePython)
  Dunit = g/cm3
  Dvalue = 1.2613
  Group = -> [C_element050,H_element043,O_element047]
  conduct = 2
  density = 1
  expand = 3
  formula = G4_GLYCEROL
  name = G4_GLYCEROL
  specific = 4
FEATURE [App::DocumentObjectGroupPython] C_element051  label="C_element : 028"  # scripted group (container) (typed FeaturePython)
  n = 5
  ref = C_element
FEATURE [App::DocumentObjectGroupPython] H_element044  label="H_element : 023"  # scripted group (container) (typed FeaturePython)
  n = 5
  ref = H_element
FEATURE [App::DocumentObjectGroupPython] N_element020  label="N_element : 009"  # scripted group (container) (typed FeaturePython)
  n = 5
  ref = N_element
FEATURE [App::DocumentObjectGroupPython] O_element048  label="O_element : 024"  # scripted group (container) (typed FeaturePython)
  n = 1
  ref = O_element
FEATURE [App::DocumentObjectGroupPython] G4_GUANINE  # scripted group (container) (typed FeaturePython)
  Dunit = g/cm3
  Dvalue = 2.2
  Group = -> [C_element051,H_element044,N_element020,O_element048]
  conduct = 2
  density = 1
  expand = 3
  formula = G4_GUANINE
  name = G4_GUANINE
  specific = 4
FEATURE [App::DocumentObjectGroupPython] Ca_element012  label="Ca_element : 006"  # scripted group (container) (typed FeaturePython)
  n = 1
  ref = Ca_element
FEATURE [App::DocumentObjectGroupPython] S_element014  label="S_element : 005"  # scripted group (container) (typed FeaturePython)
  n = 1
  ref = S_element
FEATURE [App::DocumentObjectGroupPython] O_element049  label="O_element : 6"  # scripted group (container) (typed FeaturePython)
  n = 6
  ref = O_element
FEATURE [App::DocumentObjectGroupPython] H_element045  label="H_element : 024"  # scripted group (container) (typed FeaturePython)
  n = 4
  ref = H_element
FEATURE [App::DocumentObjectGroupPython] G4_GYPSUM  # scripted group (container) (typed FeaturePython)
  Dunit = g/cm3
  Dvalue = 2.32
  Group = -> [Ca_element012,S_element014,O_element049,H_element045]
  conduct = 2
  density = 1
  expand = 3
  formula = G4_GYPSUM
  name = G4_GYPSUM
  specific = 4
FEATURE [App::DocumentObjectGroupPython] C_element052  label="C_element : 7"  # scripted group (container) (typed FeaturePython)
  n = 7
  ref = C_element
FEATURE [App::DocumentObjectGroupPython] H_element046  label="H_element : 16"  # scripted group (container) (typed FeaturePython)
  n = 16
  ref = H_element
FEATURE [App::DocumentObjectGroupPython] G4_N_HEPTANE  label="G4_N-HEPTANE"  # scripted group (container) (typed FeaturePython)
  Dunit = g/cm3
  Dvalue = 0.68376
  Group = -> [C_element052,H_element046]
  conduct = 2
  density = 1
  expand = 3
  formula = G4_N-HEPTANE
  name = G4_N-HEPTANE
  specific = 4
FEATURE [App::DocumentObjectGroupPython] C_element053  label="C_element : 029"  # scripted group (container) (typed FeaturePython)
  n = 6
  ref = C_element
FEATURE [App::DocumentObjectGroupPython] H_element047  label="H_element : 14"  # scripted group (container) (typed FeaturePython)
  n = 14
  ref = H_element
FEATURE [App::DocumentObjectGroupPython] G4_N_HEXANE  label="G4_N-HEXANE"  # scripted group (container) (typed FeaturePython)
  Dunit = g/cm3
  Dvalue = 0.6603
  Group = -> [C_element053,H_element047]
  conduct = 2
  density = 1
  expand = 3
  formula = G4_N-HEXANE
  name = G4_N-HEXANE
  specific = 4
FEATURE [App::DocumentObjectGroupPython] C_element054  label="C_element : 22"  # scripted group (container) (typed FeaturePython)
  n = 22
  ref = C_element
FEATURE [App::DocumentObjectGroupPython] H_element048  label="H_element : 025"  # scripted group (container) (typed FeaturePython)
  n = 10
  ref = H_element
FEATURE [App::DocumentObjectGroupPython] N_element021  label="N_element : 010"  # scripted group (container) (typed FeaturePython)
  n = 2
  ref = N_element
FEATURE [App::DocumentObjectGroupPython] O_element050  label="O_element : 025"  # scripted group (container) (typed FeaturePython)
  n = 5
  ref = O_element
FEATURE [App::DocumentObjectGroupPython] G4_KAPTON  # scripted group (container) (typed FeaturePython)
  Dunit = g/cm3
  Dvalue = 1.42
  Group = -> [C_element054,H_element048,N_element021,O_element050]
  conduct = 2
  density = 1
  expand = 3
  formula = G4_KAPTON
  name = G4_KAPTON
  specific = 4
FEATURE [App::DocumentObjectGroupPython] La_element001  label="La_element : 1"  # scripted group (container) (typed FeaturePython)
  n = 1
  ref = La_element
FEATURE [App::DocumentObjectGroupPython] Br_element003  label="Br_element : 002"  # scripted group (container) (typed FeaturePython)
  n = 1
  ref = Br_element
FEATURE [App::DocumentObjectGroupPython] O_element051  label="O_element : 026"  # scripted group (container) (typed FeaturePython)
  n = 1
  ref = O_element
FEATURE [App::DocumentObjectGroupPython] G4_LANTHANUM_OXYBROMIDE  # scripted group (container) (typed FeaturePython)
  Dunit = g/cm3
  Dvalue = 6.28
  Group = -> [La_element001,Br_element003,O_element051]
  conduct = 2
  density = 1
  expand = 3
  formula = G4_LANTHANUM_OXYBROMIDE
  name = G4_LANTHANUM_OXYBROMIDE
  specific = 4
FEATURE [App::DocumentObjectGroupPython] La_element002  label="La_element : 2"  # scripted group (container) (typed FeaturePython)
  n = 2
  ref = La_element
FEATURE [App::DocumentObjectGroupPython] O_element052  label="O_element : 027"  # scripted group (container) (typed FeaturePython)
  n = 2
  ref = O_element
FEATURE [App::DocumentObjectGroupPython] S_element015  label="S_element : 006"  # scripted group (container) (typed FeaturePython)
  n = 1
  ref = S_element
FEATURE [App::DocumentObjectGroupPython] G4_LANTHANUM_OXYSULFIDE  # scripted group (container) (typed FeaturePython)
  Dunit = g/cm3
  Dvalue = 5.86
  Group = -> [La_element002,O_element052,S_element015]
  conduct = 2
  density = 1
  expand = 3
  formula = G4_LANTHANUM_OXYSULFIDE
  name = G4_LANTHANUM_OXYSULFIDE
  specific = 4
FEATURE [App::DocumentObjectGroupPython] O_element053  label="O_element : 0.072"  # scripted group (container) (typed FeaturePython)
  n = 0.071682
FEATURE [App::DocumentObjectGroupPython] Pb_element002  label="Pb_element : 0.928"  # scripted group (container) (typed FeaturePython)
  n = 0.928318
FEATURE [App::DocumentObjectGroupPython] G4_LEAD_OXIDE  # scripted group (container) (typed FeaturePython)
  Dunit = g/cm3
  Dvalue = 9.53
  Group = -> [O_element053,Pb_element002]
  conduct = 2
  density = 1
  expand = 3
  formula = G4_LEAD_OXIDE
  name = G4_LEAD_OXIDE
  specific = 4
FEATURE [App::DocumentObjectGroupPython] Li_element001  label="Li_element : 1"  # scripted group (container) (typed FeaturePython)
  n = 1
  ref = Li_element
FEATURE [App::DocumentObjectGroupPython] N_element022  label="N_element : 011"  # scripted group (container) (typed FeaturePython)
  n = 1
  ref = N_element
FEATURE [App::DocumentObjectGroupPython] H_element049  label="H_element : 026"  # scripted group (container) (typed FeaturePython)
  n = 2
  ref = H_element
FEATURE [App::DocumentObjectGroupPython] G4_LITHIUM_AMIDE  # scripted group (container) (typed FeaturePython)
  Dunit = g/cm3
  Dvalue = 1.178
  Group = -> [Li_element001,N_element022,H_element049]
  conduct = 2
  density = 1
  expand = 3
  formula = G4_LITHIUM_AMIDE
  name = G4_LITHIUM_AMIDE
  specific = 4
FEATURE [App::DocumentObjectGroupPython] Li_element002  label="Li_element : 2"  # scripted group (container) (typed FeaturePython)
  n = 2
  ref = Li_element
FEATURE [App::DocumentObjectGroupPython] C_element055  label="C_element : 030"  # scripted group (container) (typed FeaturePython)
  n = 1
  ref = C_element
FEATURE [App::DocumentObjectGroupPython] O_element054  label="O_element : 028"  # scripted group (container) (typed FeaturePython)
  n = 3
  ref = O_element
FEATURE [App::DocumentObjectGroupPython] G4_LITHIUM_CARBONATE  # scripted group (container) (typed FeaturePython)
  Dunit = g/cm3
  Dvalue = 2.11
  Group = -> [Li_element002,C_element055,O_element054]
  conduct = 2
  density = 1
  expand = 3
  formula = G4_LITHIUM_CARBONATE
  name = G4_LITHIUM_CARBONATE
  specific = 4
FEATURE [App::DocumentObjectGroupPython] Li_element003  label="Li_element : 003"  # scripted group (container) (typed FeaturePython)
  n = 1
  ref = Li_element
FEATURE [App::DocumentObjectGroupPython] F_element012  label="F_element : 004"  # scripted group (container) (typed FeaturePython)
  n = 1
  ref = F_element
FEATURE [App::DocumentObjectGroupPython] G4_LITHIUM_FLUORIDE  # scripted group (container) (typed FeaturePython)
  Dunit = g/cm3
  Dvalue = 2.635
  Group = -> [Li_element003,F_element012]
  conduct = 2
  density = 1
  expand = 3
  formula = G4_LITHIUM_FLUORIDE
  name = G4_LITHIUM_FLUORIDE
  specific = 4
FEATURE [App::DocumentObjectGroupPython] Li_element004  label="Li_element : 004"  # scripted group (container) (typed FeaturePython)
  n = 1
  ref = Li_element
FEATURE [App::DocumentObjectGroupPython] H_element050  label="H_element : 027"  # scripted group (container) (typed FeaturePython)
  n = 1
  ref = H_element
FEATURE [App::DocumentObjectGroupPython] G4_LITHIUM_HYDRIDE  # scripted group (container) (typed FeaturePython)
  Dunit = g/cm3
  Dvalue = 0.82
  Group = -> [Li_element004,H_element050]
  conduct = 2
  density = 1
  expand = 3
  formula = G4_LITHIUM_HYDRIDE
  name = G4_LITHIUM_HYDRIDE
  specific = 4
FEATURE [App::DocumentObjectGroupPython] Li_element005  label="Li_element : 005"  # scripted group (container) (typed FeaturePython)
  n = 1
  ref = Li_element
FEATURE [App::DocumentObjectGroupPython] I_element003  label="I_element : 002"  # scripted group (container) (typed FeaturePython)
  n = 1
  ref = I_element
FEATURE [App::DocumentObjectGroupPython] G4_LITHIUM_IODIDE  # scripted group (container) (typed FeaturePython)
  Dunit = g/cm3
  Dvalue = 3.494
  Group = -> [Li_element005,I_element003]
  conduct = 2
  density = 1
  expand = 3
  formula = G4_LITHIUM_IODIDE
  name = G4_LITHIUM_IODIDE
  specific = 4
FEATURE [App::DocumentObjectGroupPython] Li_element006  label="Li_element : 006"  # scripted group (container) (typed FeaturePython)
  n = 2
  ref = Li_element
FEATURE [App::DocumentObjectGroupPython] O_element055  label="O_element : 029"  # scripted group (container) (typed FeaturePython)
  n = 1
  ref = O_element
FEATURE [App::DocumentObjectGroupPython] G4_LITHIUM_OXIDE  # scripted group (container) (typed FeaturePython)
  Dunit = g/cm3
  Dvalue = 2.013
  Group = -> [Li_element006,O_element055]
  conduct = 2
  density = 1
  expand = 3
  formula = G4_LITHIUM_OXIDE
  name = G4_LITHIUM_OXIDE
  specific = 4
FEATURE [App::DocumentObjectGroupPython] Li_element007  label="Li_element : 007"  # scripted group (container) (typed FeaturePython)
  n = 2
  ref = Li_element
FEATURE [App::DocumentObjectGroupPython] B_element005  label="B_element : 005"  # scripted group (container) (typed FeaturePython)
  n = 4
  ref = B_element
FEATURE [App::DocumentObjectGroupPython] O_element056  label="O_element : 7"  # scripted group (container) (typed FeaturePython)
  n = 7
  ref = O_element
FEATURE [App::DocumentObjectGroupPython] G4_LITHIUM_TETRABORATE  # scripted group (container) (typed FeaturePython)
  Dunit = g/cm3
  Dvalue = 2.44
  Group = -> [Li_element007,B_element005,O_element056]
  conduct = 2
  density = 1
  expand = 3
  formula = G4_LITHIUM_TETRABORATE
  name = G4_LITHIUM_TETRABORATE
  specific = 4
FEATURE [App::DocumentObjectGroupPython] H_element051  label="H_element : 0.105"  # scripted group (container) (typed FeaturePython)
  n = 0.105
FEATURE [App::DocumentObjectGroupPython] C_element056  label="C_element : 0.083"  # scripted group (container) (typed FeaturePython)
  n = 0.083
FEATURE [App::DocumentObjectGroupPython] N_element023  label="N_element : 0.023"  # scripted group (container) (typed FeaturePython)
  n = 0.023
FEATURE [App::DocumentObjectGroupPython] O_element057  label="O_element : 0.779"  # scripted group (container) (typed FeaturePython)
  n = 0.779
FEATURE [App::DocumentObjectGroupPython] Na_element010  label="Na_element : 0.097"  # scripted group (container) (typed FeaturePython)
  n = 0.002
FEATURE [App::DocumentObjectGroupPython] P_element006  label="P_element : 0.105"  # scripted group (container) (typed FeaturePython)
  n = 0.001
FEATURE [App::DocumentObjectGroupPython] S_element016  label="S_element : 0.017"  # scripted group (container) (typed FeaturePython)
  n = 0.002
FEATURE [App::DocumentObjectGroupPython] Cl_element014  label="Cl_element : 0.587"  # scripted group (container) (typed FeaturePython)
  n = 0.003
FEATURE [App::DocumentObjectGroupPython] K_element005  label="K_element : 0.015"  # scripted group (container) (typed FeaturePython)
  n = 0.002
FEATURE [App::DocumentObjectGroupPython] G4_LUNG_ICRP  # scripted group (container) (typed FeaturePython)
  Dunit = g/cm3
  Dvalue = 1.04
  Group = -> [H_element051,C_element056,N_element023,O_element057,Na_element010,P_element006,S_element016,Cl_element014,K_element005]
  conduct = 2
  density = 1
  expand = 3
  formula = G4_LUNG_ICRP
  name = G4_LUNG_ICRP
  specific = 4
FEATURE [App::DocumentObjectGroupPython] H_element052  label="H_element : 0.116"  # scripted group (container) (typed FeaturePython)
  n = 0.114318
FEATURE [App::DocumentObjectGroupPython] C_element057  label="C_element : 0.656"  # scripted group (container) (typed FeaturePython)
  n = 0.655824
FEATURE [App::DocumentObjectGroupPython] O_element058  label="O_element : 0.092"  # scripted group (container) (typed FeaturePython)
  n = 0.0921831
FEATURE [App::DocumentObjectGroupPython] Mg_element004  label="Mg_element : 0.135"  # scripted group (container) (typed FeaturePython)
  n = 0.134792
FEATURE [App::DocumentObjectGroupPython] Ca_element013  label="Ca_element : 0.003"  # scripted group (container) (typed FeaturePython)
  n = 0.002883
FEATURE [App::DocumentObjectGroupPython] G4_M3_WAX  # scripted group (container) (typed FeaturePython)
  Dunit = g/cm3
  Dvalue = 1.05
  Group = -> [H_element052,C_element057,O_element058,Mg_element004,Ca_element013]
  conduct = 2
  density = 1
  expand = 3
  formula = G4_M3_WAX
  name = G4_M3_WAX
  specific = 4
FEATURE [App::DocumentObjectGroupPython] Mg_element005  label="Mg_element : 1"  # scripted group (container) (typed FeaturePython)
  n = 1
  ref = Mg_element
FEATURE [App::DocumentObjectGroupPython] C_element058  label="C_element : 031"  # scripted group (container) (typed FeaturePython)
  n = 1
  ref = C_element
FEATURE [App::DocumentObjectGroupPython] O_element059  label="O_element : 030"  # scripted group (container) (typed FeaturePython)
  n = 3
  ref = O_element
FEATURE [App::DocumentObjectGroupPython] G4_MAGNESIUM_CARBONATE  # scripted group (container) (typed FeaturePython)
  Dunit = g/cm3
  Dvalue = 2.958
  Group = -> [Mg_element005,C_element058,O_element059]
  conduct = 2
  density = 1
  expand = 3
  formula = G4_MAGNESIUM_CARBONATE
  name = G4_MAGNESIUM_CARBONATE
  specific = 4
FEATURE [App::DocumentObjectGroupPython] Mg_element006  label="Mg_element : 002"  # scripted group (container) (typed FeaturePython)
  n = 1
  ref = Mg_element
FEATURE [App::DocumentObjectGroupPython] F_element013  label="F_element : 005"  # scripted group (container) (typed FeaturePython)
  n = 2
  ref = F_element
FEATURE [App::DocumentObjectGroupPython] G4_MAGNESIUM_FLUORIDE  # scripted group (container) (typed FeaturePython)
  Dunit = g/cm3
  Dvalue = 3
  Group = -> [Mg_element006,F_element013]
  conduct = 2
  density = 1
  expand = 3
  formula = G4_MAGNESIUM_FLUORIDE
  name = G4_MAGNESIUM_FLUORIDE
  specific = 4
FEATURE [App::DocumentObjectGroupPython] Mg_element007  label="Mg_element : 003"  # scripted group (container) (typed FeaturePython)
  n = 1
  ref = Mg_element
FEATURE [App::DocumentObjectGroupPython] O_element060  label="O_element : 031"  # scripted group (container) (typed FeaturePython)
  n = 1
  ref = O_element
FEATURE [App::DocumentObjectGroupPython] G4_MAGNESIUM_OXIDE  # scripted group (container) (typed FeaturePython)
  Dunit = g/cm3
  Dvalue = 3.58
  Group = -> [Mg_element007,O_element060]
  conduct = 2
  density = 1
  expand = 3
  formula = G4_MAGNESIUM_OXIDE
  name = G4_MAGNESIUM_OXIDE
  specific = 4
FEATURE [App::DocumentObjectGroupPython] Mg_element008  label="Mg_element : 004"  # scripted group (container) (typed FeaturePython)
  n = 1
  ref = Mg_element
FEATURE [App::DocumentObjectGroupPython] B_element006  label="B_element : 006"  # scripted group (container) (typed FeaturePython)
  n = 4
  ref = B_element
FEATURE [App::DocumentObjectGroupPython] O_element061  label="O_element : 032"  # scripted group (container) (typed FeaturePython)
  n = 7
  ref = O_element
FEATURE [App::DocumentObjectGroupPython] G4_MAGNESIUM_TETRABORATE  # scripted group (container) (typed FeaturePython)
  Dunit = g/cm3
  Dvalue = 2.53
  Group = -> [Mg_element008,B_element006,O_element061]
  conduct = 2
  density = 1
  expand = 3
  formula = G4_MAGNESIUM_TETRABORATE
  name = G4_MAGNESIUM_TETRABORATE
  specific = 4
FEATURE [App::DocumentObjectGroupPython] Hg_element001  label="Hg_element : 1"  # scripted group (container) (typed FeaturePython)
  n = 1
  ref = Hg_element
FEATURE [App::DocumentObjectGroupPython] I_element004  label="I_element : 2"  # scripted group (container) (typed FeaturePython)
  n = 2
  ref = I_element
FEATURE [App::DocumentObjectGroupPython] G4_MERCURIC_IODIDE  # scripted group (container) (typed FeaturePython)
  Dunit = g/cm3
  Dvalue = 6.36
  Group = -> [Hg_element001,I_element004]
  conduct = 2
  density = 1
  expand = 3
  formula = G4_MERCURIC_IODIDE
  name = G4_MERCURIC_IODIDE
  specific = 4
FEATURE [App::DocumentObjectGroupPython] C_element059  label="C_element : 032"  # scripted group (container) (typed FeaturePython)
  n = 1
  ref = C_element
FEATURE [App::DocumentObjectGroupPython] H_element053  label="H_element : 028"  # scripted group (container) (typed FeaturePython)
  n = 4
  ref = H_element
FEATURE [App::DocumentObjectGroupPython] G4_METHANE  # scripted group (container) (typed FeaturePython)
  Dunit = g/cm3
  Dvalue = 0.000667151
  Group = -> [C_element059,H_element053]
  conduct = 2
  density = 1
  expand = 3
  formula = G4_METHANE
  name = G4_METHANE
  specific = 4
FEATURE [App::DocumentObjectGroupPython] C_element060  label="C_element : 033"  # scripted group (container) (typed FeaturePython)
  n = 1
  ref = C_element
FEATURE [App::DocumentObjectGroupPython] H_element054  label="H_element : 029"  # scripted group (container) (typed FeaturePython)
  n = 4
  ref = H_element
FEATURE [App::DocumentObjectGroupPython] O_element062  label="O_element : 033"  # scripted group (container) (typed FeaturePython)
  n = 1
  ref = O_element
FEATURE [App::DocumentObjectGroupPython] G4_METHANOL  # scripted group (container) (typed FeaturePython)
  Dunit = g/cm3
  Dvalue = 0.7914
  Group = -> [C_element060,H_element054,O_element062]
  conduct = 2
  density = 1
  expand = 3
  formula = G4_METHANOL
  name = G4_METHANOL
  specific = 4
FEATURE [App::DocumentObjectGroupPython] H_element055  label="H_element : 0.134"  # scripted group (container) (typed FeaturePython)
  n = 0.13404
FEATURE [App::DocumentObjectGroupPython] C_element061  label="C_element : 0.778"  # scripted group (container) (typed FeaturePython)
  n = 0.77796
FEATURE [App::DocumentObjectGroupPython] O_element063  label="O_element : 0.035"  # scripted group (container) (typed FeaturePython)
  n = 0.03502
FEATURE [App::DocumentObjectGroupPython] Mg_element009  label="Mg_element : 0.039"  # scripted group (container) (typed FeaturePython)
  n = 0.038594
FEATURE [App::DocumentObjectGroupPython] Ti_element002  label="Ti_element : 0.014"  # scripted group (container) (typed FeaturePython)
  n = 0.014386
FEATURE [App::DocumentObjectGroupPython] G4_MIX_D_WAX  # scripted group (container) (typed FeaturePython)
  Dunit = g/cm3
  Dvalue = 0.99
  Group = -> [H_element055,C_element061,O_element063,Mg_element009,Ti_element002]
  conduct = 2
  density = 1
  expand = 3
  formula = G4_MIX_D_WAX
  name = G4_MIX_D_WAX
  specific = 4
FEATURE [App::DocumentObjectGroupPython] H_element056  label="H_element : 0.135"  # scripted group (container) (typed FeaturePython)
  n = 0.081192
FEATURE [App::DocumentObjectGroupPython] C_element062  label="C_element : 0.583"  # scripted group (container) (typed FeaturePython)
  n = 0.583442
FEATURE [App::DocumentObjectGroupPython] N_element024  label="N_element : 0.018"  # scripted group (container) (typed FeaturePython)
  n = 0.017798
FEATURE [App::DocumentObjectGroupPython] O_element064  label="O_element : 0.186"  # scripted group (container) (typed FeaturePython)
  n = 0.186381
FEATURE [App::DocumentObjectGroupPython] Mg_element010  label="Mg_element : 0.130"  # scripted group (container) (typed FeaturePython)
  n = 0.130287
FEATURE [App::DocumentObjectGroupPython] Cl_element015  label="Cl_element : 0.588"  # scripted group (container) (typed FeaturePython)
  n = 0.0009
FEATURE [App::DocumentObjectGroupPython] G4_MS20_TISSUE  # scripted group (container) (typed FeaturePython)
  Dunit = g/cm3
  Dvalue = 1
  Group = -> [H_element056,C_element062,N_element024,O_element064,Mg_element010,Cl_element015]
  conduct = 2
  density = 1
  expand = 3
  formula = G4_MS20_TISSUE
  name = G4_MS20_TISSUE
  specific = 4
FEATURE [App::DocumentObjectGroupPython] H_element057  label="H_element : 0.136"  # scripted group (container) (typed FeaturePython)
  n = 0.102
FEATURE [App::DocumentObjectGroupPython] C_element063  label="C_element : 0.143"  # scripted group (container) (typed FeaturePython)
  n = 0.143
FEATURE [App::DocumentObjectGroupPython] N_element025  label="N_element : 0.034"  # scripted group (container) (typed FeaturePython)
  n = 0.034
FEATURE [App::DocumentObjectGroupPython] O_element065  label="O_element : 0.710"  # scripted group (container) (typed FeaturePython)
  n = 0.71
FEATURE [App::DocumentObjectGroupPython] Na_element011  label="Na_element : 0.098"  # scripted group (container) (typed FeaturePython)
  n = 0.001
FEATURE [App::DocumentObjectGroupPython] P_element007  label="P_element : 0.002"  # scripted group (container) (typed FeaturePython)
  n = 0.002
FEATURE [App::DocumentObjectGroupPython] S_element017  label="S_element : 0.018"  # scripted group (container) (typed FeaturePython)
  n = 0.003
FEATURE [App::DocumentObjectGroupPython] Cl_element016  label="Cl_element : 0.589"  # scripted group (container) (typed FeaturePython)
  n = 0.001
FEATURE [App::DocumentObjectGroupPython] K_element006  label="K_element : 0.004"  # scripted group (container) (typed FeaturePython)
  n = 0.004
FEATURE [App::DocumentObjectGroupPython] G4_MUSCLE_SKELETAL_ICRP  # scripted group (container) (typed FeaturePython)
  Dunit = g/cm3
  Dvalue = 1.05
  Group = -> [H_element057,C_element063,N_element025,O_element065,Na_element011,P_element007,S_element017,Cl_element016,K_element006]
  conduct = 2
  density = 1
  expand = 3
  formula = G4_MUSCLE_SKELETAL_ICRP
  name = G4_MUSCLE_SKELETAL_ICRP
  specific = 4
FEATURE [App::DocumentObjectGroupPython] H_element058  label="H_element : 0.137"  # scripted group (container) (typed FeaturePython)
  n = 0.102102
FEATURE [App::DocumentObjectGroupPython] C_element064  label="C_element : 0.123"  # scripted group (container) (typed FeaturePython)
  n = 0.123123
FEATURE [App::DocumentObjectGroupPython] N_element026  label="N_element : 0.756"  # scripted group (container) (typed FeaturePython)
  n = 0.035035
FEATURE [App::DocumentObjectGroupPython] O_element066  label="O_element : 0.730"  # scripted group (container) (typed FeaturePython)
  n = 0.72973
FEATURE [App::DocumentObjectGroupPython] Na_element012  label="Na_element : 0.099"  # scripted group (container) (typed FeaturePython)
  n = 0.001001
FEATURE [App::DocumentObjectGroupPython] P_element008  label="P_element : 0.106"  # scripted group (container) (typed FeaturePython)
  n = 0.002002
FEATURE [App::DocumentObjectGroupPython] S_element018  label="S_element : 0.019"  # scripted group (container) (typed FeaturePython)
  n = 0.004004
FEATURE [App::DocumentObjectGroupPython] K_element007  label="K_element : 0.016"  # scripted group (container) (typed FeaturePython)
  n = 0.003003
FEATURE [App::DocumentObjectGroupPython] G4_MUSCLE_STRIATED_ICRU  # scripted group (container) (typed FeaturePython)
  Dunit = g/cm3
  Dvalue = 1.04
  Group = -> [H_element058,C_element064,N_element026,O_element066,Na_element012,P_element008,S_element018,K_element007]
  conduct = 2
  density = 1
  expand = 3
  formula = G4_MUSCLE_STRIATED_ICRU
  name = G4_MUSCLE_STRIATED_ICRU
  specific = 4
FEATURE [App::DocumentObjectGroupPython] H_element059  label="H_element : 0.098"  # scripted group (container) (typed FeaturePython)
  n = 0.0982341
FEATURE [App::DocumentObjectGroupPython] C_element065  label="C_element : 0.156"  # scripted group (container) (typed FeaturePython)
  n = 0.156214
FEATURE [App::DocumentObjectGroupPython] N_element027  label="N_element : 0.757"  # scripted group (container) (typed FeaturePython)
  n = 0.035451
FEATURE [App::DocumentObjectGroupPython] O_element067  label="O_element : 0.880"  # scripted group (container) (typed FeaturePython)
  n = 0.710101
FEATURE [App::DocumentObjectGroupPython] G4_MUSCLE_WITH_SUCROSE  # scripted group (container) (typed FeaturePython)
  Dunit = g/cm3
  Dvalue = 1.11
  Group = -> [H_element059,C_element065,N_element027,O_element067]
  conduct = 2
  density = 1
  expand = 3
  formula = G4_MUSCLE_WITH_SUCROSE
  name = G4_MUSCLE_WITH_SUCROSE
  specific = 4
FEATURE [App::DocumentObjectGroupPython] H_element060  label="H_element : 0.138"  # scripted group (container) (typed FeaturePython)
  n = 0.101969
FEATURE [App::DocumentObjectGroupPython] C_element066  label="C_element : 0.120"  # scripted group (container) (typed FeaturePython)
  n = 0.120058
FEATURE [App::DocumentObjectGroupPython] N_element028  label="N_element : 0.758"  # scripted group (container) (typed FeaturePython)
  n = 0.035451
FEATURE [App::DocumentObjectGroupPython] O_element068  label="O_element : 0.743"  # scripted group (container) (typed FeaturePython)
  n = 0.742522
FEATURE [App::DocumentObjectGroupPython] G4_MUSCLE_WITHOUT_SUCROSE  # scripted group (container) (typed FeaturePython)
  Dunit = g/cm3
  Dvalue = 1.07
  Group = -> [H_element060,C_element066,N_element028,O_element068]
  conduct = 2
  density = 1
  expand = 3
  formula = G4_MUSCLE_WITHOUT_SUCROSE
  name = G4_MUSCLE_WITHOUT_SUCROSE
  specific = 4
FEATURE [App::DocumentObjectGroupPython] C_element067  label="C_element : 10"  # scripted group (container) (typed FeaturePython)
  n = 10
  ref = C_element
FEATURE [App::DocumentObjectGroupPython] H_element061  label="H_element : 030"  # scripted group (container) (typed FeaturePython)
  n = 8
  ref = H_element
FEATURE [App::DocumentObjectGroupPython] G4_NAPHTHALENE  # scripted group (container) (typed FeaturePython)
  Dunit = g/cm3
  Dvalue = 1.145
  Group = -> [C_element067,H_element061]
  conduct = 2
  density = 1
  expand = 3
  formula = G4_NAPHTHALENE
  name = G4_NAPHTHALENE
  specific = 4
FEATURE [App::DocumentObjectGroupPython] C_element068  label="C_element : 034"  # scripted group (container) (typed FeaturePython)
  n = 6
  ref = C_element
FEATURE [App::DocumentObjectGroupPython] H_element062  label="H_element : 031"  # scripted group (container) (typed FeaturePython)
  n = 5
  ref = H_element
FEATURE [App::DocumentObjectGroupPython] N_element029  label="N_element : 012"  # scripted group (container) (typed FeaturePython)
  n = 1
  ref = N_element
FEATURE [App::DocumentObjectGroupPython] O_element069  label="O_element : 034"  # scripted group (container) (typed FeaturePython)
  n = 2
  ref = O_element
FEATURE [App::DocumentObjectGroupPython] G4_NITROBENZENE  # scripted group (container) (typed FeaturePython)
  Dunit = g/cm3
  Dvalue = 1.19867
  Group = -> [C_element068,H_element062,N_element029,O_element069]
  conduct = 2
  density = 1
  expand = 3
  formula = G4_NITROBENZENE
  name = G4_NITROBENZENE
  specific = 4
FEATURE [App::DocumentObjectGroupPython] N_element030  label="N_element : 013"  # scripted group (container) (typed FeaturePython)
  n = 2
  ref = N_element
FEATURE [App::DocumentObjectGroupPython] O_element070  label="O_element : 035"  # scripted group (container) (typed FeaturePython)
  n = 1
  ref = O_element
FEATURE [App::DocumentObjectGroupPython] G4_NITROUS_OXIDE  # scripted group (container) (typed FeaturePython)
  Dunit = g/cm3
  Dvalue = 0.00183094
  Group = -> [N_element030,O_element070]
  conduct = 2
  density = 1
  expand = 3
  formula = G4_NITROUS_OXIDE
  name = G4_NITROUS_OXIDE
  specific = 4
FEATURE [App::DocumentObjectGroupPython] H_element063  label="H_element : 0.104"  # scripted group (container) (typed FeaturePython)
  n = 0.103509
FEATURE [App::DocumentObjectGroupPython] C_element069  label="C_element : 0.648"  # scripted group (container) (typed FeaturePython)
  n = 0.648416
FEATURE [App::DocumentObjectGroupPython] N_element031  label="N_element : 0.100"  # scripted group (container) (typed FeaturePython)
  n = 0.0995361
FEATURE [App::DocumentObjectGroupPython] O_element071  label="O_element : 0.149"  # scripted group (container) (typed FeaturePython)
  n = 0.148539
FEATURE [App::DocumentObjectGroupPython] G4_NYLON_8062  label="G4_NYLON-8062"  # scripted group (container) (typed FeaturePython)
  Dunit = g/cm3
  Dvalue = 1.08
  Group = -> [H_element063,C_element069,N_element031,O_element071]
  conduct = 2
  density = 1
  expand = 3
  formula = G4_NYLON-8062
  name = G4_NYLON-8062
  specific = 4
FEATURE [App::DocumentObjectGroupPython] C_element070  label="C_element : 035"  # scripted group (container) (typed FeaturePython)
  n = 6
  ref = C_element
FEATURE [App::DocumentObjectGroupPython] H_element064  label="H_element : 11"  # scripted group (container) (typed FeaturePython)
  n = 11
  ref = H_element
FEATURE [App::DocumentObjectGroupPython] N_element032  label="N_element : 014"  # scripted group (container) (typed FeaturePython)
  n = 1
  ref = N_element
FEATURE [App::DocumentObjectGroupPython] O_element072  label="O_element : 036"  # scripted group (container) (typed FeaturePython)
  n = 1
  ref = O_element
FEATURE [App::DocumentObjectGroupPython] G4_NYLON_6_6  label="G4_NYLON-6-6"  # scripted group (container) (typed FeaturePython)
  Dunit = g/cm3
  Dvalue = 1.14
  Group = -> [C_element070,H_element064,N_element032,O_element072]
  conduct = 2
  density = 1
  expand = 3
  formula = G4_NYLON-6-6
  name = G4_NYLON-6-6
  specific = 4
FEATURE [App::DocumentObjectGroupPython] H_element065  label="H_element : 0.139"  # scripted group (container) (typed FeaturePython)
  n = 0.107062
FEATURE [App::DocumentObjectGroupPython] C_element071  label="C_element : 0.680"  # scripted group (container) (typed FeaturePython)
  n = 0.680449
FEATURE [App::DocumentObjectGroupPython] N_element033  label="N_element : 0.099"  # scripted group (container) (typed FeaturePython)
  n = 0.099189
FEATURE [App::DocumentObjectGroupPython] O_element073  label="O_element : 0.113"  # scripted group (container) (typed FeaturePython)
  n = 0.1133
FEATURE [App::DocumentObjectGroupPython] G4_NYLON_6_10  label="G4_NYLON-6-10"  # scripted group (container) (typed FeaturePython)
  Dunit = g/cm3
  Dvalue = 1.14
  Group = -> [H_element065,C_element071,N_element033,O_element073]
  conduct = 2
  density = 1
  expand = 3
  formula = G4_NYLON-6-10
  name = G4_NYLON-6-10
  specific = 4
FEATURE [App::DocumentObjectGroupPython] H_element066  label="H_element : 0.140"  # scripted group (container) (typed FeaturePython)
  n = 0.115476
FEATURE [App::DocumentObjectGroupPython] C_element072  label="C_element : 0.721"  # scripted group (container) (typed FeaturePython)
  n = 0.720818
FEATURE [App::DocumentObjectGroupPython] N_element034  label="N_element : 0.076"  # scripted group (container) (typed FeaturePython)
  n = 0.0764169
FEATURE [App::DocumentObjectGroupPython] O_element074  label="O_element : 0.087"  # scripted group (container) (typed FeaturePython)
  n = 0.0872889
FEATURE [App::DocumentObjectGroupPython] G4_NYLON_11_RILSAN  label="G4_NYLON-11_RILSAN"  # scripted group (container) (typed FeaturePython)
  Dunit = g/cm3
  Dvalue = 1.425
  Group = -> [H_element066,C_element072,N_element034,O_element074]
  conduct = 2
  density = 1
  expand = 3
  formula = G4_NYLON-11_RILSAN
  name = G4_NYLON-11_RILSAN
  specific = 4
FEATURE [App::DocumentObjectGroupPython] C_element073  label="C_element : 8"  # scripted group (container) (typed FeaturePython)
  n = 8
  ref = C_element
FEATURE [App::DocumentObjectGroupPython] H_element067  label="H_element : 18"  # scripted group (container) (typed FeaturePython)
  n = 18
  ref = H_element
FEATURE [App::DocumentObjectGroupPython] G4_OCTANE  # scripted group (container) (typed FeaturePython)
  Dunit = g/cm3
  Dvalue = 0.7026
  Group = -> [C_element073,H_element067]
  conduct = 2
  density = 1
  expand = 3
  formula = G4_OCTANE
  name = G4_OCTANE
  specific = 4
FEATURE [App::DocumentObjectGroupPython] C_element074  label="C_element : 25"  # scripted group (container) (typed FeaturePython)
  n = 25
  ref = C_element
FEATURE [App::DocumentObjectGroupPython] H_element068  label="H_element : 52"  # scripted group (container) (typed FeaturePython)
  n = 52
  ref = H_element
FEATURE [App::DocumentObjectGroupPython] G4_PARAFFIN  # scripted group (container) (typed FeaturePython)
  Dunit = g/cm3
  Dvalue = 0.93
  Group = -> [C_element074,H_element068]
  conduct = 2
  density = 1
  expand = 3
  formula = G4_PARAFFIN
  name = G4_PARAFFIN
  specific = 4
FEATURE [App::DocumentObjectGroupPython] C_element075  label="C_element : 036"  # scripted group (container) (typed FeaturePython)
  n = 5
  ref = C_element
FEATURE [App::DocumentObjectGroupPython] H_element069  label="H_element : 032"  # scripted group (container) (typed FeaturePython)
  n = 12
  ref = H_element
FEATURE [App::DocumentObjectGroupPython] G4_N_PENTANE  label="G4_N-PENTANE"  # scripted group (container) (typed FeaturePython)
  Dunit = g/cm3
  Dvalue = 0.6262
  Group = -> [C_element075,H_element069]
  conduct = 2
  density = 1
  expand = 3
  formula = G4_N-PENTANE
  name = G4_N-PENTANE
  specific = 4
FEATURE [App::DocumentObjectGroupPython] H_element070  label="H_element : 0.014"  # scripted group (container) (typed FeaturePython)
  n = 0.0141
FEATURE [App::DocumentObjectGroupPython] C_element076  label="C_element : 0.072"  # scripted group (container) (typed FeaturePython)
  n = 0.072261
FEATURE [App::DocumentObjectGroupPython] N_element035  label="N_element : 0.019"  # scripted group (container) (typed FeaturePython)
  n = 0.01932
FEATURE [App::DocumentObjectGroupPython] O_element075  label="O_element : 0.066"  # scripted group (container) (typed FeaturePython)
  n = 0.066101
FEATURE [App::DocumentObjectGroupPython] S_element019  label="S_element : 0.020"  # scripted group (container) (typed FeaturePython)
  n = 0.00189
FEATURE [App::DocumentObjectGroupPython] Br_element004  label="Br_element : 0.349"  # scripted group (container) (typed FeaturePython)
  n = 0.349103
FEATURE [App::DocumentObjectGroupPython] Ag_element001  label="Ag_element : 0.474"  # scripted group (container) (typed FeaturePython)
  n = 0.474105
FEATURE [App::DocumentObjectGroupPython] I_element005  label="I_element : 0.003"  # scripted group (container) (typed FeaturePython)
  n = 0.00312
FEATURE [App::DocumentObjectGroupPython] G4_PHOTO_EMULSION  # scripted group (container) (typed FeaturePython)
  Dunit = g/cm3
  Dvalue = 3.815
  Group = -> [H_element070,C_element076,N_element035,O_element075,S_element019,Br_element004,Ag_element001,I_element005]
  conduct = 2
  density = 1
  expand = 3
  formula = G4_PHOTO_EMULSION
  name = G4_PHOTO_EMULSION
  specific = 4
FEATURE [App::DocumentObjectGroupPython] C_element077  label="C_element : 9"  # scripted group (container) (typed FeaturePython)
  n = 9
  ref = C_element
FEATURE [App::DocumentObjectGroupPython] H_element071  label="H_element : 033"  # scripted group (container) (typed FeaturePython)
  n = 10
  ref = H_element
FEATURE [App::DocumentObjectGroupPython] G4_PLASTIC_SC_VINYLTOLUENE  # scripted group (container) (typed FeaturePython)
  Dunit = g/cm3
  Dvalue = 1.032
  Group = -> [C_element077,H_element071]
  conduct = 2
  density = 1
  expand = 3
  formula = G4_PLASTIC_SC_VINYLTOLUENE
  name = G4_PLASTIC_SC_VINYLTOLUENE
  specific = 4
FEATURE [App::DocumentObjectGroupPython] Pu_element001  label="Pu_element : 1"  # scripted group (container) (typed FeaturePython)
  n = 1
  ref = Pu_element
FEATURE [App::DocumentObjectGroupPython] O_element076  label="O_element : 037"  # scripted group (container) (typed FeaturePython)
  n = 2
  ref = O_element
FEATURE [App::DocumentObjectGroupPython] G4_PLUTONIUM_DIOXIDE  # scripted group (container) (typed FeaturePython)
  Dunit = g/cm3
  Dvalue = 11.46
  Group = -> [Pu_element001,O_element076]
  conduct = 2
  density = 1
  expand = 3
  formula = G4_PLUTONIUM_DIOXIDE
  name = G4_PLUTONIUM_DIOXIDE
  specific = 4
FEATURE [App::DocumentObjectGroupPython] C_element078  label="C_element : 037"  # scripted group (container) (typed FeaturePython)
  n = 3
  ref = C_element
FEATURE [App::DocumentObjectGroupPython] H_element072  label="H_element : 034"  # scripted group (container) (typed FeaturePython)
  n = 3
  ref = H_element
FEATURE [App::DocumentObjectGroupPython] N_element036  label="N_element : 015"  # scripted group (container) (typed FeaturePython)
  n = 1
  ref = N_element
FEATURE [App::DocumentObjectGroupPython] G4_POLYACRYLONITRILE  # scripted group (container) (typed FeaturePython)
  Dunit = g/cm3
  Dvalue = 1.17
  Group = -> [C_element078,H_element072,N_element036]
  conduct = 2
  density = 1
  expand = 3
  formula = G4_POLYACRYLONITRILE
  name = G4_POLYACRYLONITRILE
  specific = 4
FEATURE [App::DocumentObjectGroupPython] C_element079  label="C_element : 16"  # scripted group (container) (typed FeaturePython)
  n = 16
  ref = C_element
FEATURE [App::DocumentObjectGroupPython] H_element073  label="H_element : 035"  # scripted group (container) (typed FeaturePython)
  n = 14
  ref = H_element
FEATURE [App::DocumentObjectGroupPython] O_element077  label="O_element : 038"  # scripted group (container) (typed FeaturePython)
  n = 3
  ref = O_element
FEATURE [App::DocumentObjectGroupPython] G4_POLYCARBONATE  # scripted group (container) (typed FeaturePython)
  Dunit = g/cm3
  Dvalue = 1.2
  Group = -> [C_element079,H_element073,O_element077]
  conduct = 2
  density = 1
  expand = 3
  formula = G4_POLYCARBONATE
  name = G4_POLYCARBONATE
  specific = 4
FEATURE [App::DocumentObjectGroupPython] C_element080  label="C_element : 038"  # scripted group (container) (typed FeaturePython)
  n = 8
  ref = C_element
FEATURE [App::DocumentObjectGroupPython] H_element074  label="H_element : 036"  # scripted group (container) (typed FeaturePython)
  n = 7
  ref = H_element
FEATURE [App::DocumentObjectGroupPython] Cl_element017  label="Cl_element : 007"  # scripted group (container) (typed FeaturePython)
  n = 1
  ref = Cl_element
FEATURE [App::DocumentObjectGroupPython] G4_POLYCHLOROSTYRENE  # scripted group (container) (typed FeaturePython)
  Dunit = g/cm3
  Dvalue = 1.3
  Group = -> [C_element080,H_element074,Cl_element017]
  conduct = 2
  density = 1
  expand = 3
  formula = G4_POLYCHLOROSTYRENE
  name = G4_POLYCHLOROSTYRENE
  specific = 4
FEATURE [App::DocumentObjectGroupPython] C_element081  label="C_element : 039"  # scripted group (container) (typed FeaturePython)
  n = 1
  ref = C_element
FEATURE [App::DocumentObjectGroupPython] H_element075  label="H_element : 037"  # scripted group (container) (typed FeaturePython)
  n = 2
  ref = H_element
FEATURE [App::DocumentObjectGroupPython] G4_POLYETHYLENE  # scripted group (container) (typed FeaturePython)
  Dunit = g/cm3
  Dvalue = 0.94
  Group = -> [C_element081,H_element075]
  conduct = 2
  density = 1
  expand = 3
  formula = G4_POLYETHYLENE
  name = G4_POLYETHYLENE
  specific = 4
FEATURE [App::DocumentObjectGroupPython] C_element082  label="C_element : 040"  # scripted group (container) (typed FeaturePython)
  n = 10
  ref = C_element
FEATURE [App::DocumentObjectGroupPython] H_element076  label="H_element : 038"  # scripted group (container) (typed FeaturePython)
  n = 8
  ref = H_element
FEATURE [App::DocumentObjectGroupPython] O_element078  label="O_element : 039"  # scripted group (container) (typed FeaturePython)
  n = 4
  ref = O_element
FEATURE [App::DocumentObjectGroupPython] G4_MYLAR  # scripted group (container) (typed FeaturePython)
  Dunit = g/cm3
  Dvalue = 1.4
  Group = -> [C_element082,H_element076,O_element078]
  conduct = 2
  density = 1
  expand = 3
  formula = G4_MYLAR
  name = G4_MYLAR
  specific = 4
FEATURE [App::DocumentObjectGroupPython] C_element083  label="C_element : 041"  # scripted group (container) (typed FeaturePython)
  n = 5
  ref = C_element
FEATURE [App::DocumentObjectGroupPython] H_element077  label="H_element : 039"  # scripted group (container) (typed FeaturePython)
  n = 8
  ref = H_element
FEATURE [App::DocumentObjectGroupPython] O_element079  label="O_element : 040"  # scripted group (container) (typed FeaturePython)
  n = 2
  ref = O_element
FEATURE [App::DocumentObjectGroupPython] G4_PLEXIGLASS  # scripted group (container) (typed FeaturePython)
  Dunit = g/cm3
  Dvalue = 1.19
  Group = -> [C_element083,H_element077,O_element079]
  conduct = 2
  density = 1
  expand = 3
  formula = G4_PLEXIGLASS
  name = G4_PLEXIGLASS
  specific = 4
FEATURE [App::DocumentObjectGroupPython] C_element084  label="C_element : 042"  # scripted group (container) (typed FeaturePython)
  n = 1
  ref = C_element
FEATURE [App::DocumentObjectGroupPython] H_element078  label="H_element : 040"  # scripted group (container) (typed FeaturePython)
  n = 2
  ref = H_element
FEATURE [App::DocumentObjectGroupPython] O_element080  label="O_element : 041"  # scripted group (container) (typed FeaturePython)
  n = 1
  ref = O_element
FEATURE [App::DocumentObjectGroupPython] G4_POLYOXYMETHYLENE  # scripted group (container) (typed FeaturePython)
  Dunit = g/cm3
  Dvalue = 1.425
  Group = -> [C_element084,H_element078,O_element080]
  conduct = 2
  density = 1
  expand = 3
  formula = G4_POLYOXYMETHYLENE
  name = G4_POLYOXYMETHYLENE
  specific = 4
FEATURE [App::DocumentObjectGroupPython] C_element085  label="C_element : 043"  # scripted group (container) (typed FeaturePython)
  n = 2
  ref = C_element
FEATURE [App::DocumentObjectGroupPython] H_element079  label="H_element : 041"  # scripted group (container) (typed FeaturePython)
  n = 4
  ref = H_element
FEATURE [App::DocumentObjectGroupPython] G4_POLYPROPYLENE  # scripted group (container) (typed FeaturePython)
  Dunit = g/cm3
  Dvalue = 0.9
  Group = -> [C_element085,H_element079]
  conduct = 2
  density = 1
  expand = 3
  formula = G4_POLYPROPYLENE
  name = G4_POLYPROPYLENE
  specific = 4
FEATURE [App::DocumentObjectGroupPython] C_element086  label="C_element : 044"  # scripted group (container) (typed FeaturePython)
  n = 8
  ref = C_element
FEATURE [App::DocumentObjectGroupPython] H_element080  label="H_element : 042"  # scripted group (container) (typed FeaturePython)
  n = 8
  ref = H_element
FEATURE [App::DocumentObjectGroupPython] G4_POLYSTYRENE  # scripted group (container) (typed FeaturePython)
  Dunit = g/cm3
  Dvalue = 1.06
  Group = -> [C_element086,H_element080]
  conduct = 2
  density = 1
  expand = 3
  formula = G4_POLYSTYRENE
  name = G4_POLYSTYRENE
  specific = 4
FEATURE [App::DocumentObjectGroupPython] C_element087  label="C_element : 045"  # scripted group (container) (typed FeaturePython)
  n = 2
  ref = C_element
FEATURE [App::DocumentObjectGroupPython] F_element014  label="F_element : 4"  # scripted group (container) (typed FeaturePython)
  n = 4
  ref = F_element
FEATURE [App::DocumentObjectGroupPython] G4_TEFLON  # scripted group (container) (typed FeaturePython)
  Dunit = g/cm3
  Dvalue = 2.2
  Group = -> [C_element087,F_element014]
  conduct = 2
  density = 1
  expand = 3
  formula = G4_TEFLON
  name = G4_TEFLON
  specific = 4
FEATURE [App::DocumentObjectGroupPython] C_element088  label="C_element : 046"  # scripted group (container) (typed FeaturePython)
  n = 2
  ref = C_element
FEATURE [App::DocumentObjectGroupPython] F_element015  label="F_element : 006"  # scripted group (container) (typed FeaturePython)
  n = 3
  ref = F_element
FEATURE [App::DocumentObjectGroupPython] Cl_element018  label="Cl_element : 008"  # scripted group (container) (typed FeaturePython)
  n = 1
  ref = Cl_element
FEATURE [App::DocumentObjectGroupPython] G4_POLYTRIFLUOROCHLOROETHYLENE  # scripted group (container) (typed FeaturePython)
  Dunit = g/cm3
  Dvalue = 2.1
  Group = -> [C_element088,F_element015,Cl_element018]
  conduct = 2
  density = 1
  expand = 3
  formula = G4_POLYTRIFLUOROCHLOROETHYLENE
  name = G4_POLYTRIFLUOROCHLOROETHYLENE
  specific = 4
FEATURE [App::DocumentObjectGroupPython] C_element089  label="C_element : 047"  # scripted group (container) (typed FeaturePython)
  n = 4
  ref = C_element
FEATURE [App::DocumentObjectGroupPython] H_element081  label="H_element : 043"  # scripted group (container) (typed FeaturePython)
  n = 6
  ref = H_element
FEATURE [App::DocumentObjectGroupPython] O_element081  label="O_element : 042"  # scripted group (container) (typed FeaturePython)
  n = 2
  ref = O_element
FEATURE [App::DocumentObjectGroupPython] G4_POLYVINYL_ACETATE  # scripted group (container) (typed FeaturePython)
  Dunit = g/cm3
  Dvalue = 1.19
  Group = -> [C_element089,H_element081,O_element081]
  conduct = 2
  density = 1
  expand = 3
  formula = G4_POLYVINYL_ACETATE
  name = G4_POLYVINYL_ACETATE
  specific = 4
FEATURE [App::DocumentObjectGroupPython] C_element090  label="C_element : 048"  # scripted group (container) (typed FeaturePython)
  n = 2
  ref = C_element
FEATURE [App::DocumentObjectGroupPython] H_element082  label="H_element : 044"  # scripted group (container) (typed FeaturePython)
  n = 4
  ref = H_element
FEATURE [App::DocumentObjectGroupPython] O_element082  label="O_element : 043"  # scripted group (container) (typed FeaturePython)
  n = 1
  ref = O_element
FEATURE [App::DocumentObjectGroupPython] G4_POLYVINYL_ALCOHOL  # scripted group (container) (typed FeaturePython)
  Dunit = g/cm3
  Dvalue = 1.3
  Group = -> [C_element090,H_element082,O_element082]
  conduct = 2
  density = 1
  expand = 3
  formula = G4_POLYVINYL_ALCOHOL
  name = G4_POLYVINYL_ALCOHOL
  specific = 4
FEATURE [App::DocumentObjectGroupPython] C_element091  label="C_element : 049"  # scripted group (container) (typed FeaturePython)
  n = 8
  ref = C_element
FEATURE [App::DocumentObjectGroupPython] H_element083  label="H_element : 045"  # scripted group (container) (typed FeaturePython)
  n = 14
  ref = H_element
FEATURE [App::DocumentObjectGroupPython] O_element083  label="O_element : 044"  # scripted group (container) (typed FeaturePython)
  n = 2
  ref = O_element
FEATURE [App::DocumentObjectGroupPython] G4_POLYVINYL_BUTYRAL  # scripted group (container) (typed FeaturePython)
  Dunit = g/cm3
  Dvalue = 1.12
  Group = -> [C_element091,H_element083,O_element083]
  conduct = 2
  density = 1
  expand = 3
  formula = G4_POLYVINYL_BUTYRAL
  name = G4_POLYVINYL_BUTYRAL
  specific = 4
FEATURE [App::DocumentObjectGroupPython] C_element092  label="C_element : 050"  # scripted group (container) (typed FeaturePython)
  n = 2
  ref = C_element
FEATURE [App::DocumentObjectGroupPython] H_element084  label="H_element : 046"  # scripted group (container) (typed FeaturePython)
  n = 3
  ref = H_element
FEATURE [App::DocumentObjectGroupPython] Cl_element019  label="Cl_element : 009"  # scripted group (container) (typed FeaturePython)
  n = 1
  ref = Cl_element
FEATURE [App::DocumentObjectGroupPython] G4_POLYVINYL_CHLORIDE  # scripted group (container) (typed FeaturePython)
  Dunit = g/cm3
  Dvalue = 1.3
  Group = -> [C_element092,H_element084,Cl_element019]
  conduct = 2
  density = 1
  expand = 3
  formula = G4_POLYVINYL_CHLORIDE
  name = G4_POLYVINYL_CHLORIDE
  specific = 4
FEATURE [App::DocumentObjectGroupPython] C_element093  label="C_element : 051"  # scripted group (container) (typed FeaturePython)
  n = 2
  ref = C_element
FEATURE [App::DocumentObjectGroupPython] H_element085  label="H_element : 047"  # scripted group (container) (typed FeaturePython)
  n = 2
  ref = H_element
FEATURE [App::DocumentObjectGroupPython] Cl_element020  label="Cl_element : 010"  # scripted group (container) (typed FeaturePython)
  n = 2
  ref = Cl_element
FEATURE [App::DocumentObjectGroupPython] G4_POLYVINYLIDENE_CHLORIDE  # scripted group (container) (typed FeaturePython)
  Dunit = g/cm3
  Dvalue = 1.7
  Group = -> [C_element093,H_element085,Cl_element020]
  conduct = 2
  density = 1
  expand = 3
  formula = G4_POLYVINYLIDENE_CHLORIDE
  name = G4_POLYVINYLIDENE_CHLORIDE
  specific = 4
FEATURE [App::DocumentObjectGroupPython] C_element094  label="C_element : 052"  # scripted group (container) (typed FeaturePython)
  n = 2
  ref = C_element
FEATURE [App::DocumentObjectGroupPython] H_element086  label="H_element : 048"  # scripted group (container) (typed FeaturePython)
  n = 2
  ref = H_element
FEATURE [App::DocumentObjectGroupPython] F_element016  label="F_element : 007"  # scripted group (container) (typed FeaturePython)
  n = 2
  ref = F_element
FEATURE [App::DocumentObjectGroupPython] G4_POLYVINYLIDENE_FLUORIDE  # scripted group (container) (typed FeaturePython)
  Dunit = g/cm3
  Dvalue = 1.76
  Group = -> [C_element094,H_element086,F_element016]
  conduct = 2
  density = 1
  expand = 3
  formula = G4_POLYVINYLIDENE_FLUORIDE
  name = G4_POLYVINYLIDENE_FLUORIDE
  specific = 4
FEATURE [App::DocumentObjectGroupPython] C_element095  label="C_element : 053"  # scripted group (container) (typed FeaturePython)
  n = 6
  ref = C_element
FEATURE [App::DocumentObjectGroupPython] H_element087  label="H_element : 9"  # scripted group (container) (typed FeaturePython)
  n = 9
  ref = H_element
FEATURE [App::DocumentObjectGroupPython] N_element037  label="N_element : 016"  # scripted group (container) (typed FeaturePython)
  n = 1
  ref = N_element
FEATURE [App::DocumentObjectGroupPython] O_element084  label="O_element : 045"  # scripted group (container) (typed FeaturePython)
  n = 1
  ref = O_element
FEATURE [App::DocumentObjectGroupPython] G4_POLYVINYL_PYRROLIDONE  # scripted group (container) (typed FeaturePython)
  Dunit = g/cm3
  Dvalue = 1.25
  Group = -> [C_element095,H_element087,N_element037,O_element084]
  conduct = 2
  density = 1
  expand = 3
  formula = G4_POLYVINYL_PYRROLIDONE
  name = G4_POLYVINYL_PYRROLIDONE
  specific = 4
FEATURE [App::DocumentObjectGroupPython] K_element008  label="K_element : 1"  # scripted group (container) (typed FeaturePython)
  n = 1
  ref = K_element
FEATURE [App::DocumentObjectGroupPython] I_element006  label="I_element : 003"  # scripted group (container) (typed FeaturePython)
  n = 1
  ref = I_element
FEATURE [App::DocumentObjectGroupPython] G4_POTASSIUM_IODIDE  # scripted group (container) (typed FeaturePython)
  Dunit = g/cm3
  Dvalue = 3.13
  Group = -> [K_element008,I_element006]
  conduct = 2
  density = 1
  expand = 3
  formula = G4_POTASSIUM_IODIDE
  name = G4_POTASSIUM_IODIDE
  specific = 4
FEATURE [App::DocumentObjectGroupPython] K_element009  label="K_element : 2"  # scripted group (container) (typed FeaturePython)
  n = 2
  ref = K_element
FEATURE [App::DocumentObjectGroupPython] O_element085  label="O_element : 046"  # scripted group (container) (typed FeaturePython)
  n = 1
  ref = O_element
FEATURE [App::DocumentObjectGroupPython] G4_POTASSIUM_OXIDE  # scripted group (container) (typed FeaturePython)
  Dunit = g/cm3
  Dvalue = 2.32
  Group = -> [K_element009,O_element085]
  conduct = 2
  density = 1
  expand = 3
  formula = G4_POTASSIUM_OXIDE
  name = G4_POTASSIUM_OXIDE
  specific = 4
FEATURE [App::DocumentObjectGroupPython] C_element096  label="C_element : 054"  # scripted group (container) (typed FeaturePython)
  n = 3
  ref = C_element
FEATURE [App::DocumentObjectGroupPython] H_element088  label="H_element : 049"  # scripted group (container) (typed FeaturePython)
  n = 8
  ref = H_element
FEATURE [App::DocumentObjectGroupPython] G4_PROPANE  # scripted group (container) (typed FeaturePython)
  Dunit = g/cm3
  Dvalue = 0.00187939
  Group = -> [C_element096,H_element088]
  conduct = 2
  density = 1
  expand = 3
  formula = G4_PROPANE
  name = G4_PROPANE
  specific = 4
FEATURE [App::DocumentObjectGroupPython] C_element097  label="C_element : 055"  # scripted group (container) (typed FeaturePython)
  n = 3
  ref = C_element
FEATURE [App::DocumentObjectGroupPython] H_element089  label="H_element : 050"  # scripted group (container) (typed FeaturePython)
  n = 8
  ref = H_element
FEATURE [App::DocumentObjectGroupPython] G4_lPROPANE  # scripted group (container) (typed FeaturePython)
  Dunit = g/cm3
  Dvalue = 0.43
  Group = -> [C_element097,H_element089]
  conduct = 2
  density = 1
  expand = 3
  formula = G4_lPROPANE
  name = G4_lPROPANE
  specific = 4
FEATURE [App::DocumentObjectGroupPython] C_element098  label="C_element : 056"  # scripted group (container) (typed FeaturePython)
  n = 3
  ref = C_element
FEATURE [App::DocumentObjectGroupPython] H_element090  label="H_element : 051"  # scripted group (container) (typed FeaturePython)
  n = 8
  ref = H_element
FEATURE [App::DocumentObjectGroupPython] O_element086  label="O_element : 047"  # scripted group (container) (typed FeaturePython)
  n = 1
  ref = O_element
FEATURE [App::DocumentObjectGroupPython] G4_N_PROPYL_ALCOHOL  label="G4_N-PROPYL_ALCOHOL"  # scripted group (container) (typed FeaturePython)
  Dunit = g/cm3
  Dvalue = 0.8035
  Group = -> [C_element098,H_element090,O_element086]
  conduct = 2
  density = 1
  expand = 3
  formula = G4_N-PROPYL_ALCOHOL
  name = G4_N-PROPYL_ALCOHOL
  specific = 4
FEATURE [App::DocumentObjectGroupPython] C_element099  label="C_element : 057"  # scripted group (container) (typed FeaturePython)
  n = 5
  ref = C_element
FEATURE [App::DocumentObjectGroupPython] H_element091  label="H_element : 052"  # scripted group (container) (typed FeaturePython)
  n = 5
  ref = H_element
FEATURE [App::DocumentObjectGroupPython] N_element038  label="N_element : 017"  # scripted group (container) (typed FeaturePython)
  n = 1
  ref = N_element
FEATURE [App::DocumentObjectGroupPython] G4_PYRIDINE  # scripted group (container) (typed FeaturePython)
  Dunit = g/cm3
  Dvalue = 0.9819
  Group = -> [C_element099,H_element091,N_element038]
  conduct = 2
  density = 1
  expand = 3
  formula = G4_PYRIDINE
  name = G4_PYRIDINE
  specific = 4
FEATURE [App::DocumentObjectGroupPython] H_element092  label="H_element : 0.144"  # scripted group (container) (typed FeaturePython)
  n = 0.143711
FEATURE [App::DocumentObjectGroupPython] C_element100  label="C_element : 0.856"  # scripted group (container) (typed FeaturePython)
  n = 0.856289
FEATURE [App::DocumentObjectGroupPython] G4_RUBBER_BUTYL  # scripted group (container) (typed FeaturePython)
  Dunit = g/cm3
  Dvalue = 0.92
  Group = -> [H_element092,C_element100]
  conduct = 2
  density = 1
  expand = 3
  formula = G4_RUBBER_BUTYL
  name = G4_RUBBER_BUTYL
  specific = 4
FEATURE [App::DocumentObjectGroupPython] H_element093  label="H_element : 0.118"  # scripted group (container) (typed FeaturePython)
  n = 0.118371
FEATURE [App::DocumentObjectGroupPython] C_element101  label="C_element : 0.882"  # scripted group (container) (typed FeaturePython)
  n = 0.881629
FEATURE [App::DocumentObjectGroupPython] G4_RUBBER_NATURAL  # scripted group (container) (typed FeaturePython)
  Dunit = g/cm3
  Dvalue = 0.92
  Group = -> [H_element093,C_element101]
  conduct = 2
  density = 1
  expand = 3
  formula = G4_RUBBER_NATURAL
  name = G4_RUBBER_NATURAL
  specific = 4
FEATURE [App::DocumentObjectGroupPython] H_element094  label="H_element : 0.145"  # scripted group (container) (typed FeaturePython)
  n = 0.05692
FEATURE [App::DocumentObjectGroupPython] C_element102  label="C_element : 0.543"  # scripted group (container) (typed FeaturePython)
  n = 0.542646
FEATURE [App::DocumentObjectGroupPython] Cl_element021  label="Cl_element : 0.400"  # scripted group (container) (typed FeaturePython)
  n = 0.400434
FEATURE [App::DocumentObjectGroupPython] G4_RUBBER_NEOPRENE  # scripted group (container) (typed FeaturePython)
  Dunit = g/cm3
  Dvalue = 1.23
  Group = -> [H_element094,C_element102,Cl_element021]
  conduct = 2
  density = 1
  expand = 3
  formula = G4_RUBBER_NEOPRENE
  name = G4_RUBBER_NEOPRENE
  specific = 4
FEATURE [App::DocumentObjectGroupPython] Si_element006  label="Si_element : 1"  # scripted group (container) (typed FeaturePython)
  n = 1
  ref = Si_element
FEATURE [App::DocumentObjectGroupPython] O_element087  label="O_element : 048"  # scripted group (container) (typed FeaturePython)
  n = 2
  ref = O_element
FEATURE [App::DocumentObjectGroupPython] G4_SILICON_DIOXIDE  # scripted group (container) (typed FeaturePython)
  Dunit = g/cm3
  Dvalue = 2.32
  Group = -> [Si_element006,O_element087]
  conduct = 2
  density = 1
  expand = 3
  formula = G4_SILICON_DIOXIDE
  name = G4_SILICON_DIOXIDE
  specific = 4
FEATURE [App::DocumentObjectGroupPython] Ag_element002  label="Ag_element : 1"  # scripted group (container) (typed FeaturePython)
  n = 1
  ref = Ag_element
FEATURE [App::DocumentObjectGroupPython] Br_element005  label="Br_element : 003"  # scripted group (container) (typed FeaturePython)
  n = 1
  ref = Br_element
FEATURE [App::DocumentObjectGroupPython] G4_SILVER_BROMIDE  # scripted group (container) (typed FeaturePython)
  Dunit = g/cm3
  Dvalue = 6.473
  Group = -> [Ag_element002,Br_element005]
  conduct = 2
  density = 1
  expand = 3
  formula = G4_SILVER_BROMIDE
  name = G4_SILVER_BROMIDE
  specific = 4
FEATURE [App::DocumentObjectGroupPython] Ag_element003  label="Ag_element : 002"  # scripted group (container) (typed FeaturePython)
  n = 1
  ref = Ag_element
FEATURE [App::DocumentObjectGroupPython] Cl_element022  label="Cl_element : 011"  # scripted group (container) (typed FeaturePython)
  n = 1
  ref = Cl_element
FEATURE [App::DocumentObjectGroupPython] G4_SILVER_CHLORIDE  # scripted group (container) (typed FeaturePython)
  Dunit = g/cm3
  Dvalue = 5.56
  Group = -> [Ag_element003,Cl_element022]
  conduct = 2
  density = 1
  expand = 3
  formula = G4_SILVER_CHLORIDE
  name = G4_SILVER_CHLORIDE
  specific = 4
FEATURE [App::DocumentObjectGroupPython] Br_element006  label="Br_element : 0.423"  # scripted group (container) (typed FeaturePython)
  n = 0.422895
FEATURE [App::DocumentObjectGroupPython] Ag_element004  label="Ag_element : 0.574"  # scripted group (container) (typed FeaturePython)
  n = 0.573748
FEATURE [App::DocumentObjectGroupPython] I_element007  label="I_element : 0.649"  # scripted group (container) (typed FeaturePython)
  n = 0.003357
FEATURE [App::DocumentObjectGroupPython] G4_SILVER_HALIDES  # scripted group (container) (typed FeaturePython)
  Dunit = g/cm3
  Dvalue = 6.47
  Group = -> [Br_element006,Ag_element004,I_element007]
  conduct = 2
  density = 1
  expand = 3
  formula = G4_SILVER_HALIDES
  name = G4_SILVER_HALIDES
  specific = 4
FEATURE [App::DocumentObjectGroupPython] Ag_element005  label="Ag_element : 003"  # scripted group (container) (typed FeaturePython)
  n = 1
  ref = Ag_element
FEATURE [App::DocumentObjectGroupPython] I_element008  label="I_element : 004"  # scripted group (container) (typed FeaturePython)
  n = 1
  ref = I_element
FEATURE [App::DocumentObjectGroupPython] G4_SILVER_IODIDE  # scripted group (container) (typed FeaturePython)
  Dunit = g/cm3
  Dvalue = 6.01
  Group = -> [Ag_element005,I_element008]
  conduct = 2
  density = 1
  expand = 3
  formula = G4_SILVER_IODIDE
  name = G4_SILVER_IODIDE
  specific = 4
FEATURE [App::DocumentObjectGroupPython] H_element095  label="H_element : 0.100"  # scripted group (container) (typed FeaturePython)
  n = 0.1
FEATURE [App::DocumentObjectGroupPython] C_element103  label="C_element : 0.204"  # scripted group (container) (typed FeaturePython)
  n = 0.204
FEATURE [App::DocumentObjectGroupPython] N_element039  label="N_element : 0.759"  # scripted group (container) (typed FeaturePython)
  n = 0.042
FEATURE [App::DocumentObjectGroupPython] O_element088  label="O_element : 0.645"  # scripted group (container) (typed FeaturePython)
  n = 0.645
FEATURE [App::DocumentObjectGroupPython] Na_element013  label="Na_element : 0.100"  # scripted group (container) (typed FeaturePython)
  n = 0.002
FEATURE [App::DocumentObjectGroupPython] P_element009  label="P_element : 0.107"  # scripted group (container) (typed FeaturePython)
  n = 0.001
FEATURE [App::DocumentObjectGroupPython] S_element020  label="S_element : 0.021"  # scripted group (container) (typed FeaturePython)
  n = 0.002
FEATURE [App::DocumentObjectGroupPython] Cl_element023  label="Cl_element : 0.590"  # scripted group (container) (typed FeaturePython)
  n = 0.003
FEATURE [App::DocumentObjectGroupPython] K_element010  label="K_element : 0.001"  # scripted group (container) (typed FeaturePython)
  n = 0.001
FEATURE [App::DocumentObjectGroupPython] G4_SKIN_ICRP  # scripted group (container) (typed FeaturePython)
  Dunit = g/cm3
  Dvalue = 1.09
  Group = -> [H_element095,C_element103,N_element039,O_element088,Na_element013,P_element009,S_element020,Cl_element023,K_element010]
  conduct = 2
  density = 1
  expand = 3
  formula = G4_SKIN_ICRP
  name = G4_SKIN_ICRP
  specific = 4
FEATURE [App::DocumentObjectGroupPython] Na_element014  label="Na_element : 2"  # scripted group (container) (typed FeaturePython)
  n = 2
  ref = Na_element
FEATURE [App::DocumentObjectGroupPython] C_element104  label="C_element : 058"  # scripted group (container) (typed FeaturePython)
  n = 1
  ref = C_element
FEATURE [App::DocumentObjectGroupPython] O_element089  label="O_element : 049"  # scripted group (container) (typed FeaturePython)
  n = 3
  ref = O_element
FEATURE [App::DocumentObjectGroupPython] G4_SODIUM_CARBONATE  # scripted group (container) (typed FeaturePython)
  Dunit = g/cm3
  Dvalue = 2.532
  Group = -> [Na_element014,C_element104,O_element089]
  conduct = 2
  density = 1
  expand = 3
  formula = G4_SODIUM_CARBONATE
  name = G4_SODIUM_CARBONATE
  specific = 4
FEATURE [App::DocumentObjectGroupPython] Na_element015  label="Na_element : 1"  # scripted group (container) (typed FeaturePython)
  n = 1
  ref = Na_element
FEATURE [App::DocumentObjectGroupPython] I_element009  label="I_element : 005"  # scripted group (container) (typed FeaturePython)
  n = 1
  ref = I_element
FEATURE [App::DocumentObjectGroupPython] G4_SODIUM_IODIDE  # scripted group (container) (typed FeaturePython)
  Dunit = g/cm3
  Dvalue = 3.667
  Group = -> [Na_element015,I_element009]
  conduct = 2
  density = 1
  expand = 3
  formula = G4_SODIUM_IODIDE
  name = G4_SODIUM_IODIDE
  specific = 4
FEATURE [App::DocumentObjectGroupPython] Na_element016  label="Na_element : 003"  # scripted group (container) (typed FeaturePython)
  n = 2
  ref = Na_element
FEATURE [App::DocumentObjectGroupPython] O_element090  label="O_element : 050"  # scripted group (container) (typed FeaturePython)
  n = 1
  ref = O_element
FEATURE [App::DocumentObjectGroupPython] G4_SODIUM_MONOXIDE  # scripted group (container) (typed FeaturePython)
  Dunit = g/cm3
  Dvalue = 2.27
  Group = -> [Na_element016,O_element090]
  conduct = 2
  density = 1
  expand = 3
  formula = G4_SODIUM_MONOXIDE
  name = G4_SODIUM_MONOXIDE
  specific = 4
FEATURE [App::DocumentObjectGroupPython] Na_element017  label="Na_element : 004"  # scripted group (container) (typed FeaturePython)
  n = 1
  ref = Na_element
FEATURE [App::DocumentObjectGroupPython] N_element040  label="N_element : 018"  # scripted group (container) (typed FeaturePython)
  n = 1
  ref = N_element
FEATURE [App::DocumentObjectGroupPython] O_element091  label="O_element : 051"  # scripted group (container) (typed FeaturePython)
  n = 3
  ref = O_element
FEATURE [App::DocumentObjectGroupPython] G4_SODIUM_NITRATE  # scripted group (container) (typed FeaturePython)
  Dunit = g/cm3
  Dvalue = 2.261
  Group = -> [Na_element017,N_element040,O_element091]
  conduct = 2
  density = 1
  expand = 3
  formula = G4_SODIUM_NITRATE
  name = G4_SODIUM_NITRATE
  specific = 4
FEATURE [App::DocumentObjectGroupPython] C_element105  label="C_element : 059"  # scripted group (container) (typed FeaturePython)
  n = 14
  ref = C_element
FEATURE [App::DocumentObjectGroupPython] H_element096  label="H_element : 053"  # scripted group (container) (typed FeaturePython)
  n = 12
  ref = H_element
FEATURE [App::DocumentObjectGroupPython] G4_STILBENE  # scripted group (container) (typed FeaturePython)
  Dunit = g/cm3
  Dvalue = 0.9707
  Group = -> [C_element105,H_element096]
  conduct = 2
  density = 1
  expand = 3
  formula = G4_STILBENE
  name = G4_STILBENE
  specific = 4
FEATURE [App::DocumentObjectGroupPython] C_element106  label="C_element : 12"  # scripted group (container) (typed FeaturePython)
  n = 12
  ref = C_element
FEATURE [App::DocumentObjectGroupPython] H_element097  label="H_element : 22"  # scripted group (container) (typed FeaturePython)
  n = 22
  ref = H_element
FEATURE [App::DocumentObjectGroupPython] O_element092  label="O_element : 11"  # scripted group (container) (typed FeaturePython)
  n = 11
  ref = O_element
FEATURE [App::DocumentObjectGroupPython] G4_SUCROSE  # scripted group (container) (typed FeaturePython)
  Dunit = g/cm3
  Dvalue = 1.5805
  Group = -> [C_element106,H_element097,O_element092]
  conduct = 2
  density = 1
  expand = 3
  formula = G4_SUCROSE
  name = G4_SUCROSE
  specific = 4
FEATURE [App::DocumentObjectGroupPython] C_element107  label="C_element : 18"  # scripted group (container) (typed FeaturePython)
  n = 18
  ref = C_element
FEATURE [App::DocumentObjectGroupPython] H_element098  label="H_element : 054"  # scripted group (container) (typed FeaturePython)
  n = 14
  ref = H_element
FEATURE [App::DocumentObjectGroupPython] G4_TERPHENYL  # scripted group (container) (typed FeaturePython)
  Dunit = g/cm3
  Dvalue = 1.24
  Group = -> [C_element107,H_element098]
  conduct = 2
  density = 1
  expand = 3
  formula = G4_TERPHENYL
  name = G4_TERPHENYL
  specific = 4
FEATURE [App::DocumentObjectGroupPython] H_element099  label="H_element : 0.146"  # scripted group (container) (typed FeaturePython)
  n = 0.106
FEATURE [App::DocumentObjectGroupPython] C_element108  label="C_element : 0.883"  # scripted group (container) (typed FeaturePython)
  n = 0.099
FEATURE [App::DocumentObjectGroupPython] N_element041  label="N_element : 0.020"  # scripted group (container) (typed FeaturePython)
  n = 0.02
FEATURE [App::DocumentObjectGroupPython] O_element093  label="O_element : 0.766"  # scripted group (container) (typed FeaturePython)
  n = 0.766
FEATURE [App::DocumentObjectGroupPython] Na_element018  label="Na_element : 0.101"  # scripted group (container) (typed FeaturePython)
  n = 0.002
FEATURE [App::DocumentObjectGroupPython] P_element010  label="P_element : 0.108"  # scripted group (container) (typed FeaturePython)
  n = 0.001
FEATURE [App::DocumentObjectGroupPython] S_element021  label="S_element : 0.022"  # scripted group (container) (typed FeaturePython)
  n = 0.002
FEATURE [App::DocumentObjectGroupPython] Cl_element024  label="Cl_element : 0.002"  # scripted group (container) (typed FeaturePython)
  n = 0.002
FEATURE [App::DocumentObjectGroupPython] K_element011  label="K_element : 0.017"  # scripted group (container) (typed FeaturePython)
  n = 0.002
FEATURE [App::DocumentObjectGroupPython] G4_TESTIS_ICRP  # scripted group (container) (typed FeaturePython)
  Dunit = g/cm3
  Dvalue = 1.04
  Group = -> [H_element099,C_element108,N_element041,O_element093,Na_element018,P_element010,S_element021,Cl_element024,K_element011]
  conduct = 2
  density = 1
  expand = 3
  formula = G4_TESTIS_ICRP
  name = G4_TESTIS_ICRP
  specific = 4
FEATURE [App::DocumentObjectGroupPython] C_element109  label="C_element : 060"  # scripted group (container) (typed FeaturePython)
  n = 2
  ref = C_element
FEATURE [App::DocumentObjectGroupPython] Cl_element025  label="Cl_element : 012"  # scripted group (container) (typed FeaturePython)
  n = 4
  ref = Cl_element
FEATURE [App::DocumentObjectGroupPython] G4_TETRACHLOROETHYLENE  # scripted group (container) (typed FeaturePython)
  Dunit = g/cm3
  Dvalue = 1.625
  Group = -> [C_element109,Cl_element025]
  conduct = 2
  density = 1
  expand = 3
  formula = G4_TETRACHLOROETHYLENE
  name = G4_TETRACHLOROETHYLENE
  specific = 4
FEATURE [App::DocumentObjectGroupPython] Tl_element001  label="Tl_element : 1"  # scripted group (container) (typed FeaturePython)
  n = 1
  ref = Tl_element
FEATURE [App::DocumentObjectGroupPython] Cl_element026  label="Cl_element : 013"  # scripted group (container) (typed FeaturePython)
  n = 1
  ref = Cl_element
FEATURE [App::DocumentObjectGroupPython] G4_THALLIUM_CHLORIDE  # scripted group (container) (typed FeaturePython)
  Dunit = g/cm3
  Dvalue = 7.004
  Group = -> [Tl_element001,Cl_element026]
  conduct = 2
  density = 1
  expand = 3
  formula = G4_THALLIUM_CHLORIDE
  name = G4_THALLIUM_CHLORIDE
  specific = 4
FEATURE [App::DocumentObjectGroupPython] H_element100  label="H_element : 0.147"  # scripted group (container) (typed FeaturePython)
  n = 0.105
FEATURE [App::DocumentObjectGroupPython] C_element110  label="C_element : 0.256"  # scripted group (container) (typed FeaturePython)
  n = 0.256
FEATURE [App::DocumentObjectGroupPython] N_element042  label="N_element : 0.760"  # scripted group (container) (typed FeaturePython)
  n = 0.027
FEATURE [App::DocumentObjectGroupPython] O_element094  label="O_element : 0.602"  # scripted group (container) (typed FeaturePython)
  n = 0.602
FEATURE [App::DocumentObjectGroupPython] Na_element019  label="Na_element : 0.102"  # scripted group (container) (typed FeaturePython)
  n = 0.001
FEATURE [App::DocumentObjectGroupPython] P_element011  label="P_element : 0.109"  # scripted group (container) (typed FeaturePython)
  n = 0.002
FEATURE [App::DocumentObjectGroupPython] S_element022  label="S_element : 0.023"  # scripted group (container) (typed FeaturePython)
  n = 0.003
FEATURE [App::DocumentObjectGroupPython] Cl_element027  label="Cl_element : 0.591"  # scripted group (container) (typed FeaturePython)
  n = 0.002
FEATURE [App::DocumentObjectGroupPython] K_element012  label="K_element : 0.018"  # scripted group (container) (typed FeaturePython)
  n = 0.002
FEATURE [App::DocumentObjectGroupPython] G4_TISSUE_SOFT_ICRP  # scripted group (container) (typed FeaturePython)
  Dunit = g/cm3
  Dvalue = 1.03
  Group = -> [H_element100,C_element110,N_element042,O_element094,Na_element019,P_element011,S_element022,Cl_element027,K_element012]
  conduct = 2
  density = 1
  expand = 3
  formula = G4_TISSUE_SOFT_ICRP
  name = G4_TISSUE_SOFT_ICRP
  specific = 4
FEATURE [App::DocumentObjectGroupPython] H_element101  label="H_element : 0.148"  # scripted group (container) (typed FeaturePython)
  n = 0.101
FEATURE [App::DocumentObjectGroupPython] C_element111  label="C_element : 0.111"  # scripted group (container) (typed FeaturePython)
  n = 0.111
FEATURE [App::DocumentObjectGroupPython] N_element043  label="N_element : 0.026"  # scripted group (container) (typed FeaturePython)
  n = 0.026
FEATURE [App::DocumentObjectGroupPython] O_element095  label="O_element : 0.762"  # scripted group (container) (typed FeaturePython)
  n = 0.762
FEATURE [App::DocumentObjectGroupPython] G4_TISSUE_SOFT_ICRU_4  label="G4_TISSUE_SOFT_ICRU-4"  # scripted group (container) (typed FeaturePython)
  Dunit = g/cm3
  Dvalue = 1
  Group = -> [H_element101,C_element111,N_element043,O_element095]
  conduct = 2
  density = 1
  expand = 3
  formula = G4_TISSUE_SOFT_ICRU-4
  name = G4_TISSUE_SOFT_ICRU-4
  specific = 4
FEATURE [App::DocumentObjectGroupPython] H_element102  label="H_element : 0.149"  # scripted group (container) (typed FeaturePython)
  n = 0.101869
FEATURE [App::DocumentObjectGroupPython] C_element112  label="C_element : 0.456"  # scripted group (container) (typed FeaturePython)
  n = 0.456179
FEATURE [App::DocumentObjectGroupPython] N_element044  label="N_element : 0.761"  # scripted group (container) (typed FeaturePython)
  n = 0.035172
FEATURE [App::DocumentObjectGroupPython] O_element096  label="O_element : 0.407"  # scripted group (container) (typed FeaturePython)
  n = 0.40678
FEATURE [App::DocumentObjectGroupPython] G4_TISSUE_METHANE  label="G4_TISSUE-METHANE"  # scripted group (container) (typed FeaturePython)
  Dunit = g/cm3
  Dvalue = 0.00106409
  Group = -> [H_element102,C_element112,N_element044,O_element096]
  conduct = 2
  density = 1
  expand = 3
  formula = G4_TISSUE-METHANE
  name = G4_TISSUE-METHANE
  specific = 4
FEATURE [App::DocumentObjectGroupPython] H_element103  label="H_element : 0.103"  # scripted group (container) (typed FeaturePython)
  n = 0.102672
FEATURE [App::DocumentObjectGroupPython] C_element113  label="C_element : 0.569"  # scripted group (container) (typed FeaturePython)
  n = 0.56894
FEATURE [App::DocumentObjectGroupPython] N_element045  label="N_element : 0.762"  # scripted group (container) (typed FeaturePython)
  n = 0.035022
FEATURE [App::DocumentObjectGroupPython] O_element097  label="O_element : 0.293"  # scripted group (container) (typed FeaturePython)
  n = 0.293366
FEATURE [App::DocumentObjectGroupPython] G4_TISSUE_PROPANE  label="G4_TISSUE-PROPANE"  # scripted group (container) (typed FeaturePython)
  Dunit = g/cm3
  Dvalue = 0.00182628
  Group = -> [H_element103,C_element113,N_element045,O_element097]
  conduct = 2
  density = 1
  expand = 3
  formula = G4_TISSUE-PROPANE
  name = G4_TISSUE-PROPANE
  specific = 4
FEATURE [App::DocumentObjectGroupPython] Ti_element003  label="Ti_element : 1"  # scripted group (container) (typed FeaturePython)
  n = 1
  ref = Ti_element
FEATURE [App::DocumentObjectGroupPython] O_element098  label="O_element : 052"  # scripted group (container) (typed FeaturePython)
  n = 2
  ref = O_element
FEATURE [App::DocumentObjectGroupPython] G4_TITANIUM_DIOXIDE  # scripted group (container) (typed FeaturePython)
  Dunit = g/cm3
  Dvalue = 4.26
  Group = -> [Ti_element003,O_element098]
  conduct = 2
  density = 1
  expand = 3
  formula = G4_TITANIUM_DIOXIDE
  name = G4_TITANIUM_DIOXIDE
  specific = 4
FEATURE [App::DocumentObjectGroupPython] C_element114  label="C_element : 061"  # scripted group (container) (typed FeaturePython)
  n = 7
  ref = C_element
FEATURE [App::DocumentObjectGroupPython] H_element104  label="H_element : 055"  # scripted group (container) (typed FeaturePython)
  n = 8
  ref = H_element
FEATURE [App::DocumentObjectGroupPython] G4_TOLUENE  # scripted group (container) (typed FeaturePython)
  Dunit = g/cm3
  Dvalue = 0.8669
  Group = -> [C_element114,H_element104]
  conduct = 2
  density = 1
  expand = 3
  formula = G4_TOLUENE
  name = G4_TOLUENE
  specific = 4
FEATURE [App::DocumentObjectGroupPython] C_element115  label="C_element : 062"  # scripted group (container) (typed FeaturePython)
  n = 2
  ref = C_element
FEATURE [App::DocumentObjectGroupPython] H_element105  label="H_element : 056"  # scripted group (container) (typed FeaturePython)
  n = 1
  ref = H_element
FEATURE [App::DocumentObjectGroupPython] Cl_element028  label="Cl_element : 014"  # scripted group (container) (typed FeaturePython)
  n = 3
  ref = Cl_element
FEATURE [App::DocumentObjectGroupPython] G4_TRICHLOROETHYLENE  # scripted group (container) (typed FeaturePython)
  Dunit = g/cm3
  Dvalue = 1.46
  Group = -> [C_element115,H_element105,Cl_element028]
  conduct = 2
  density = 1
  expand = 3
  formula = G4_TRICHLOROETHYLENE
  name = G4_TRICHLOROETHYLENE
  specific = 4
FEATURE [App::DocumentObjectGroupPython] C_element116  label="C_element : 063"  # scripted group (container) (typed FeaturePython)
  n = 6
  ref = C_element
FEATURE [App::DocumentObjectGroupPython] H_element106  label="H_element : 15"  # scripted group (container) (typed FeaturePython)
  n = 15
  ref = H_element
FEATURE [App::DocumentObjectGroupPython] O_element099  label="O_element : 053"  # scripted group (container) (typed FeaturePython)
  n = 4
  ref = O_element
FEATURE [App::DocumentObjectGroupPython] P_element012  label="P_element : 1"  # scripted group (container) (typed FeaturePython)
  n = 1
  ref = P_element
FEATURE [App::DocumentObjectGroupPython] G4_TRIETHYL_PHOSPHATE  # scripted group (container) (typed FeaturePython)
  Dunit = g/cm3
  Dvalue = 1.07
  Group = -> [C_element116,H_element106,O_element099,P_element012]
  conduct = 2
  density = 1
  expand = 3
  formula = G4_TRIETHYL_PHOSPHATE
  name = G4_TRIETHYL_PHOSPHATE
  specific = 4
FEATURE [App::DocumentObjectGroupPython] W_element003  label="W_element : 003"  # scripted group (container) (typed FeaturePython)
  n = 1
  ref = W_element
FEATURE [App::DocumentObjectGroupPython] F_element017  label="F_element : 6"  # scripted group (container) (typed FeaturePython)
  n = 6
  ref = F_element
FEATURE [App::DocumentObjectGroupPython] G4_TUNGSTEN_HEXAFLUORIDE  # scripted group (container) (typed FeaturePython)
  Dunit = g/cm3
  Dvalue = 2.4
  Group = -> [W_element003,F_element017]
  conduct = 2
  density = 1
  expand = 3
  formula = G4_TUNGSTEN_HEXAFLUORIDE
  name = G4_TUNGSTEN_HEXAFLUORIDE
  specific = 4
FEATURE [App::DocumentObjectGroupPython] U_element001  label="U_element : 1"  # scripted group (container) (typed FeaturePython)
  n = 1
  ref = U_element
FEATURE [App::DocumentObjectGroupPython] C_element117  label="C_element : 064"  # scripted group (container) (typed FeaturePython)
  n = 2
  ref = C_element
FEATURE [App::DocumentObjectGroupPython] G4_URANIUM_DICARBIDE  # scripted group (container) (typed FeaturePython)
  Dunit = g/cm3
  Dvalue = 11.28
  Group = -> [U_element001,C_element117]
  conduct = 2
  density = 1
  expand = 3
  formula = G4_URANIUM_DICARBIDE
  name = G4_URANIUM_DICARBIDE
  specific = 4
FEATURE [App::DocumentObjectGroupPython] U_element002  label="U_element : 002"  # scripted group (container) (typed FeaturePython)
  n = 1
  ref = U_element
FEATURE [App::DocumentObjectGroupPython] C_element118  label="C_element : 065"  # scripted group (container) (typed FeaturePython)
  n = 1
  ref = C_element
FEATURE [App::DocumentObjectGroupPython] G4_URANIUM_MONOCARBIDE  # scripted group (container) (typed FeaturePython)
  Dunit = g/cm3
  Dvalue = 13.63
  Group = -> [U_element002,C_element118]
  conduct = 2
  density = 1
  expand = 3
  formula = G4_URANIUM_MONOCARBIDE
  name = G4_URANIUM_MONOCARBIDE
  specific = 4
FEATURE [App::DocumentObjectGroupPython] U_element003  label="U_element : 003"  # scripted group (container) (typed FeaturePython)
  n = 1
  ref = U_element
FEATURE [App::DocumentObjectGroupPython] O_element100  label="O_element : 054"  # scripted group (container) (typed FeaturePython)
  n = 2
  ref = O_element
FEATURE [App::DocumentObjectGroupPython] G4_URANIUM_OXIDE  # scripted group (container) (typed FeaturePython)
  Dunit = g/cm3
  Dvalue = 10.96
  Group = -> [U_element003,O_element100]
  conduct = 2
  density = 1
  expand = 3
  formula = G4_URANIUM_OXIDE
  name = G4_URANIUM_OXIDE
  specific = 4
FEATURE [App::DocumentObjectGroupPython] C_element119  label="C_element : 066"  # scripted group (container) (typed FeaturePython)
  n = 1
  ref = C_element
FEATURE [App::DocumentObjectGroupPython] H_element107  label="H_element : 057"  # scripted group (container) (typed FeaturePython)
  n = 4
  ref = H_element
FEATURE [App::DocumentObjectGroupPython] N_element046  label="N_element : 019"  # scripted group (container) (typed FeaturePython)
  n = 2
  ref = N_element
FEATURE [App::DocumentObjectGroupPython] O_element101  label="O_element : 055"  # scripted group (container) (typed FeaturePython)
  n = 1
  ref = O_element
FEATURE [App::DocumentObjectGroupPython] G4_UREA  # scripted group (container) (typed FeaturePython)
  Dunit = g/cm3
  Dvalue = 1.323
  Group = -> [C_element119,H_element107,N_element046,O_element101]
  conduct = 2
  density = 1
  expand = 3
  formula = G4_UREA
  name = G4_UREA
  specific = 4
FEATURE [App::DocumentObjectGroupPython] C_element120  label="C_element : 067"  # scripted group (container) (typed FeaturePython)
  n = 5
  ref = C_element
FEATURE [App::DocumentObjectGroupPython] H_element108  label="H_element : 058"  # scripted group (container) (typed FeaturePython)
  n = 11
  ref = H_element
FEATURE [App::DocumentObjectGroupPython] N_element047  label="N_element : 020"  # scripted group (container) (typed FeaturePython)
  n = 1
  ref = N_element
FEATURE [App::DocumentObjectGroupPython] O_element102  label="O_element : 056"  # scripted group (container) (typed FeaturePython)
  n = 2
  ref = O_element
FEATURE [App::DocumentObjectGroupPython] G4_VALINE  # scripted group (container) (typed FeaturePython)
  Dunit = g/cm3
  Dvalue = 1.23
  Group = -> [C_element120,H_element108,N_element047,O_element102]
  conduct = 2
  density = 1
  expand = 3
  formula = G4_VALINE
  name = G4_VALINE
  specific = 4
FEATURE [App::DocumentObjectGroupPython] H_element109  label="H_element : 0.009"  # scripted group (container) (typed FeaturePython)
  n = 0.009417
FEATURE [App::DocumentObjectGroupPython] C_element121  label="C_element : 0.281"  # scripted group (container) (typed FeaturePython)
  n = 0.280555
FEATURE [App::DocumentObjectGroupPython] F_element018  label="F_element : 0.710"  # scripted group (container) (typed FeaturePython)
  n = 0.710028
FEATURE [App::DocumentObjectGroupPython] G4_VITON  # scripted group (container) (typed FeaturePython)
  Dunit = g/cm3
  Dvalue = 1.8
  Group = -> [H_element109,C_element121,F_element018]
  conduct = 2
  density = 1
  expand = 3
  formula = G4_VITON
  name = G4_VITON
  specific = 4
FEATURE [App::DocumentObjectGroupPython] H_element110  label="H_element : 059"  # scripted group (container) (typed FeaturePython)
  n = 2
  ref = H_element
FEATURE [App::DocumentObjectGroupPython] O_element103  label="O_element : 057"  # scripted group (container) (typed FeaturePython)
  n = 1
  ref = O_element
FEATURE [App::DocumentObjectGroupPython] G4_WATER  # scripted group (container) (typed FeaturePython)
  Dunit = g/cm3
  Dvalue = 1
  Group = -> [H_element110,O_element103]
  conduct = 2
  density = 1
  expand = 3
  formula = G4_WATER
  name = G4_WATER
  specific = 4
FEATURE [App::DocumentObjectGroupPython] H_element111  label="H_element : 060"  # scripted group (container) (typed FeaturePython)
  n = 2
  ref = H_element
FEATURE [App::DocumentObjectGroupPython] O_element104  label="O_element : 058"  # scripted group (container) (typed FeaturePython)
  n = 1
  ref = O_element
FEATURE [App::DocumentObjectGroupPython] G4_WATER_VAPOR  # scripted group (container) (typed FeaturePython)
  Dunit = g/cm3
  Dvalue = 0.000756182
  Group = -> [H_element111,O_element104]
  conduct = 2
  density = 1
  expand = 3
  formula = G4_WATER_VAPOR
  name = G4_WATER_VAPOR
  specific = 4
FEATURE [App::DocumentObjectGroupPython] C_element122  label="C_element : 068"  # scripted group (container) (typed FeaturePython)
  n = 8
  ref = C_element
FEATURE [App::DocumentObjectGroupPython] H_element112  label="H_element : 061"  # scripted group (container) (typed FeaturePython)
  n = 10
  ref = H_element
FEATURE [App::DocumentObjectGroupPython] G4_XYLENE  # scripted group (container) (typed FeaturePython)
  Dunit = g/cm3
  Dvalue = 0.87
  Group = -> [C_element122,H_element112]
  conduct = 2
  density = 1
  expand = 3
  formula = G4_XYLENE
  name = G4_XYLENE
  specific = 4
FEATURE [App::DocumentObjectGroupPython] C_element123  label="C_element : 069"  # scripted group (container) (typed FeaturePython)
  n = 1
  ref = C_element
FEATURE [App::DocumentObjectGroupPython] G4_GRAPHITE  # scripted group (container) (typed FeaturePython)
  Dunit = g/cm3
  Dvalue = 2.21
  Group = -> [C_element123]
  conduct = 2
  density = 1
  expand = 3
  formula = G4_GRAPHITE
  name = G4_GRAPHITE
  specific = 4
FEATURE [App::DocumentObjectGroupPython] NIST  # scripted group (container) (typed FeaturePython)
  Group = -> [G4_A_150_TISSUE,G4_ACETONE,G4_ACETYLENE,G4_ADENINE,G4_ADIPOSE_TISSUE_ICRP,G4_AIR,G4_ALANINE,G4_ALUMINUM_OXIDE,G4_AMBER,G4_AMMONIA,G4_ANILINE,G4_ANTHRACENE,G4_B_100_BONE,G4_BAKELITE,G4_BARIUM_FLUORIDE,G4_BARIUM_SULFATE,G4_BENZENE,G4_BERYLLIUM_OXIDE,G4_BGO,G4_BLOOD_ICRP,G4_BONE_COMPACT_ICRU,G4_BONE_CORTICAL_ICRP,G4_BORON_CARBIDE,G4_BORON_OXIDE,G4_BRAIN_ICRP,G4_BUTANE,G4_N_BUTYL_ALCOHOL,G4_C_552,+152 more]
FEATURE [App::DocumentObjectGroupPython] H_element113  label="H_element : 062"  # scripted group (container) (typed FeaturePython)
  n = 1
  ref = H_element
FEATURE [App::DocumentObjectGroupPython] G4_H  # scripted group (container) (typed FeaturePython)
  Dunit = g/cm3
  Dvalue = 8.3748e-05
  Group = -> [H_element113]
  conduct = 2
  density = 1
  expand = 3
  formula = H
  name = G4_H
  specific = 4
FEATURE [App::DocumentObjectGroupPython] He_element001  label="He_element : 1"  # scripted group (container) (typed FeaturePython)
  n = 1
  ref = He_element
FEATURE [App::DocumentObjectGroupPython] G4_He  # scripted group (container) (typed FeaturePython)
  Dunit = g/cm3
  Dvalue = 0.000166322
  Group = -> [He_element001]
  conduct = 2
  density = 1
  expand = 3
  formula = He
  name = G4_He
  specific = 4
FEATURE [App::DocumentObjectGroupPython] Li_element008  label="Li_element : 008"  # scripted group (container) (typed FeaturePython)
  n = 1
  ref = Li_element
FEATURE [App::DocumentObjectGroupPython] G4_Li  # scripted group (container) (typed FeaturePython)
  Dunit = g/cm3
  Dvalue = 0.534
  Group = -> [Li_element008]
  conduct = 2
  density = 1
  expand = 3
  formula = Li
  name = G4_Li
  specific = 4
FEATURE [App::DocumentObjectGroupPython] Be_element002  label="Be_element : 002"  # scripted group (container) (typed FeaturePython)
  n = 1
  ref = Be_element
FEATURE [App::DocumentObjectGroupPython] G4_Be  # scripted group (container) (typed FeaturePython)
  Dunit = g/cm3
  Dvalue = 1.848
  Group = -> [Be_element002]
  conduct = 2
  density = 1
  expand = 3
  formula = Be
  name = G4_Be
  specific = 4
FEATURE [App::DocumentObjectGroupPython] B_element007  label="B_element : 007"  # scripted group (container) (typed FeaturePython)
  n = 1
  ref = B_element
FEATURE [App::DocumentObjectGroupPython] G4_B  # scripted group (container) (typed FeaturePython)
  Dunit = g/cm3
  Dvalue = 2.37
  Group = -> [B_element007]
  conduct = 2
  density = 1
  expand = 3
  formula = B
  name = G4_B
  specific = 4
FEATURE [App::DocumentObjectGroupPython] C_element124  label="C_element : 070"  # scripted group (container) (typed FeaturePython)
  n = 1
  ref = C_element
FEATURE [App::DocumentObjectGroupPython] G4_C  # scripted group (container) (typed FeaturePython)
  Dunit = g/cm3
  Dvalue = 2
  Group = -> [C_element124]
  conduct = 2
  density = 1
  expand = 3
  formula = C
  name = G4_C
  specific = 4
FEATURE [App::DocumentObjectGroupPython] N_element048  label="N_element : 021"  # scripted group (container) (typed FeaturePython)
  n = 1
  ref = N_element
FEATURE [App::DocumentObjectGroupPython] G4_N  # scripted group (container) (typed FeaturePython)
  Dunit = g/cm3
  Dvalue = 0.0011652
  Group = -> [N_element048]
  conduct = 2
  density = 1
  expand = 3
  formula = N
  name = G4_N
  specific = 4
FEATURE [App::DocumentObjectGroupPython] O_element105  label="O_element : 059"  # scripted group (container) (typed FeaturePython)
  n = 1
  ref = O_element
FEATURE [App::DocumentObjectGroupPython] G4_O  # scripted group (container) (typed FeaturePython)
  Dunit = g/cm3
  Dvalue = 0.00133151
  Group = -> [O_element105]
  conduct = 2
  density = 1
  expand = 3
  formula = O
  name = G4_O
  specific = 4
FEATURE [App::DocumentObjectGroupPython] F_element019  label="F_element : 008"  # scripted group (container) (typed FeaturePython)
  n = 1
  ref = F_element
FEATURE [App::DocumentObjectGroupPython] G4_F  # scripted group (container) (typed FeaturePython)
  Dunit = g/cm3
  Dvalue = 0.00158029
  Group = -> [F_element019]
  conduct = 2
  density = 1
  expand = 3
  formula = F
  name = G4_F
  specific = 4
FEATURE [App::DocumentObjectGroupPython] Ne_element001  label="Ne_element : 1"  # scripted group (container) (typed FeaturePython)
  n = 1
  ref = Ne_element
FEATURE [App::DocumentObjectGroupPython] G4_Ne  # scripted group (container) (typed FeaturePython)
  Dunit = g/cm3
  Dvalue = 0.000838505
  Group = -> [Ne_element001]
  conduct = 2
  density = 1
  expand = 3
  formula = Ne
  name = G4_Ne
  specific = 4
FEATURE [App::DocumentObjectGroupPython] Na_element020  label="Na_element : 005"  # scripted group (container) (typed FeaturePython)
  n = 1
  ref = Na_element
FEATURE [App::DocumentObjectGroupPython] G4_Na  # scripted group (container) (typed FeaturePython)
  Dunit = g/cm3
  Dvalue = 0.971
  Group = -> [Na_element020]
  conduct = 2
  density = 1
  expand = 3
  formula = Na
  name = G4_Na
  specific = 4
FEATURE [App::DocumentObjectGroupPython] Mg_element011  label="Mg_element : 005"  # scripted group (container) (typed FeaturePython)
  n = 1
  ref = Mg_element
FEATURE [App::DocumentObjectGroupPython] G4_Mg  # scripted group (container) (typed FeaturePython)
  Dunit = g/cm3
  Dvalue = 1.74
  Group = -> [Mg_element011]
  conduct = 2
  density = 1
  expand = 3
  formula = Mg
  name = G4_Mg
  specific = 4
FEATURE [App::DocumentObjectGroupPython] Al_element004  label="Al_element : 1"  # scripted group (container) (typed FeaturePython)
  n = 1
  ref = Al_element
FEATURE [App::DocumentObjectGroupPython] G4_Al  # scripted group (container) (typed FeaturePython)
  Dunit = g/cm3
  Dvalue = 2.699
  Group = -> [Al_element004]
  conduct = 2
  density = 1
  expand = 3
  formula = Al
  name = G4_Al
  specific = 4
FEATURE [App::DocumentObjectGroupPython] Si_element007  label="Si_element : 002"  # scripted group (container) (typed FeaturePython)
  n = 1
  ref = Si_element
FEATURE [App::DocumentObjectGroupPython] G4_Si  # scripted group (container) (typed FeaturePython)
  Dunit = g/cm3
  Dvalue = 2.33
  Group = -> [Si_element007]
  conduct = 2
  density = 1
  expand = 3
  formula = Si
  name = G4_Si
  specific = 4
FEATURE [App::DocumentObjectGroupPython] P_element013  label="P_element : 002"  # scripted group (container) (typed FeaturePython)
  n = 1
  ref = P_element
FEATURE [App::DocumentObjectGroupPython] G4_P  # scripted group (container) (typed FeaturePython)
  Dunit = g/cm3
  Dvalue = 2.2
  Group = -> [P_element013]
  conduct = 2
  density = 1
  expand = 3
  formula = P
  name = G4_P
  specific = 4
FEATURE [App::DocumentObjectGroupPython] S_element023  label="S_element : 007"  # scripted group (container) (typed FeaturePython)
  n = 1
  ref = S_element
FEATURE [App::DocumentObjectGroupPython] G4_S  # scripted group (container) (typed FeaturePython)
  Dunit = g/cm3
  Dvalue = 2
  Group = -> [S_element023]
  conduct = 2
  density = 1
  expand = 3
  formula = S
  name = G4_S
  specific = 4
FEATURE [App::DocumentObjectGroupPython] Cl_element029  label="Cl_element : 015"  # scripted group (container) (typed FeaturePython)
  n = 1
  ref = Cl_element
FEATURE [App::DocumentObjectGroupPython] G4_Cl  # scripted group (container) (typed FeaturePython)
  Dunit = g/cm3
  Dvalue = 0.00299473
  Group = -> [Cl_element029]
  conduct = 2
  density = 1
  expand = 3
  formula = Cl
  name = G4_Cl
  specific = 4
FEATURE [App::DocumentObjectGroupPython] Ar_element002  label="Ar_element : 1"  # scripted group (container) (typed FeaturePython)
  n = 1
  ref = Ar_element
FEATURE [App::DocumentObjectGroupPython] G4_Ar  # scripted group (container) (typed FeaturePython)
  Dunit = g/cm3
  Dvalue = 0.00166201
  Group = -> [Ar_element002]
  conduct = 2
  density = 1
  expand = 3
  formula = Ar
  name = G4_Ar
  specific = 4
FEATURE [App::DocumentObjectGroupPython] K_element013  label="K_element : 003"  # scripted group (container) (typed FeaturePython)
  n = 1
  ref = K_element
FEATURE [App::DocumentObjectGroupPython] G4_K  # scripted group (container) (typed FeaturePython)
  Dunit = g/cm3
  Dvalue = 0.862
  Group = -> [K_element013]
  conduct = 2
  density = 1
  expand = 3
  formula = K
  name = G4_K
  specific = 4
FEATURE [App::DocumentObjectGroupPython] Ca_element014  label="Ca_element : 007"  # scripted group (container) (typed FeaturePython)
  n = 1
  ref = Ca_element
FEATURE [App::DocumentObjectGroupPython] G4_Ca  # scripted group (container) (typed FeaturePython)
  Dunit = g/cm3
  Dvalue = 1.55
  Group = -> [Ca_element014]
  conduct = 2
  density = 1
  expand = 3
  formula = Ca
  name = G4_Ca
  specific = 4
FEATURE [App::DocumentObjectGroupPython] Sc_element001  label="Sc_element : 1"  # scripted group (container) (typed FeaturePython)
  n = 1
  ref = Sc_element
FEATURE [App::DocumentObjectGroupPython] G4_Sc  # scripted group (container) (typed FeaturePython)
  Dunit = g/cm3
  Dvalue = 2.989
  Group = -> [Sc_element001]
  conduct = 2
  density = 1
  expand = 3
  formula = Sc
  name = G4_Sc
  specific = 4
FEATURE [App::DocumentObjectGroupPython] Ti_element004  label="Ti_element : 002"  # scripted group (container) (typed FeaturePython)
  n = 1
  ref = Ti_element
FEATURE [App::DocumentObjectGroupPython] G4_Ti  # scripted group (container) (typed FeaturePython)
  Dunit = g/cm3
  Dvalue = 4.54
  Group = -> [Ti_element004]
  conduct = 2
  density = 1
  expand = 3
  formula = Ti
  name = G4_Ti
  specific = 4
FEATURE [App::DocumentObjectGroupPython] V_element001  label="V_element : 1"  # scripted group (container) (typed FeaturePython)
  n = 1
  ref = V_element
FEATURE [App::DocumentObjectGroupPython] G4_V  # scripted group (container) (typed FeaturePython)
  Dunit = g/cm3
  Dvalue = 6.11
  Group = -> [V_element001]
  conduct = 2
  density = 1
  expand = 3
  formula = V
  name = G4_V
  specific = 4
FEATURE [App::DocumentObjectGroupPython] Cr_element001  label="Cr_element : 1"  # scripted group (container) (typed FeaturePython)
  n = 1
  ref = Cr_element
FEATURE [App::DocumentObjectGroupPython] G4_Cr  # scripted group (container) (typed FeaturePython)
  Dunit = g/cm3
  Dvalue = 7.18
  Group = -> [Cr_element001]
  conduct = 2
  density = 1
  expand = 3
  formula = Cr
  name = G4_Cr
  specific = 4
FEATURE [App::DocumentObjectGroupPython] Mn_element001  label="Mn_element : 1"  # scripted group (container) (typed FeaturePython)
  n = 1
  ref = Mn_element
FEATURE [App::DocumentObjectGroupPython] G4_Mn  # scripted group (container) (typed FeaturePython)
  Dunit = g/cm3
  Dvalue = 7.44
  Group = -> [Mn_element001]
  conduct = 2
  density = 1
  expand = 3
  formula = Mn
  name = G4_Mn
  specific = 4
FEATURE [App::DocumentObjectGroupPython] Fe_element007  label="Fe_element : 004"  # scripted group (container) (typed FeaturePython)
  n = 1
  ref = Fe_element
FEATURE [App::DocumentObjectGroupPython] G4_Fe  # scripted group (container) (typed FeaturePython)
  Dunit = g/cm3
  Dvalue = 7.874
  Group = -> [Fe_element007]
  conduct = 2
  density = 1
  expand = 3
  formula = Fe
  name = G4_Fe
  specific = 4
FEATURE [App::DocumentObjectGroupPython] Co_element001  label="Co_element : 1"  # scripted group (container) (typed FeaturePython)
  n = 1
  ref = Co_element
FEATURE [App::DocumentObjectGroupPython] G4_Co  # scripted group (container) (typed FeaturePython)
  Dunit = g/cm3
  Dvalue = 8.9
  Group = -> [Co_element001]
  conduct = 2
  density = 1
  expand = 3
  formula = Co
  name = G4_Co
  specific = 4
FEATURE [App::DocumentObjectGroupPython] Ni_element001  label="Ni_element : 1"  # scripted group (container) (typed FeaturePython)
  n = 1
  ref = Ni_element
FEATURE [App::DocumentObjectGroupPython] G4_Ni  # scripted group (container) (typed FeaturePython)
  Dunit = g/cm3
  Dvalue = 8.902
  Group = -> [Ni_element001]
  conduct = 2
  density = 1
  expand = 3
  formula = Ni
  name = G4_Ni
  specific = 4
FEATURE [App::DocumentObjectGroupPython] Cu_element001  label="Cu_element : 1"  # scripted group (container) (typed FeaturePython)
  n = 1
  ref = Cu_element
FEATURE [App::DocumentObjectGroupPython] G4_Cu  # scripted group (container) (typed FeaturePython)
  Dunit = g/cm3
  Dvalue = 8.96
  Group = -> [Cu_element001]
  conduct = 2
  density = 1
  expand = 3
  formula = Cu
  name = G4_Cu
  specific = 4
FEATURE [App::DocumentObjectGroupPython] Zn_element001  label="Zn_element : 1"  # scripted group (container) (typed FeaturePython)
  n = 1
  ref = Zn_element
FEATURE [App::DocumentObjectGroupPython] G4_Zn  # scripted group (container) (typed FeaturePython)
  Dunit = g/cm3
  Dvalue = 7.133
  Group = -> [Zn_element001]
  conduct = 2
  density = 1
  expand = 3
  formula = Zn
  name = G4_Zn
  specific = 4
FEATURE [App::DocumentObjectGroupPython] Ga_element002  label="Ga_element : 002"  # scripted group (container) (typed FeaturePython)
  n = 1
  ref = Ga_element
FEATURE [App::DocumentObjectGroupPython] G4_Ga  # scripted group (container) (typed FeaturePython)
  Dunit = g/cm3
  Dvalue = 5.904
  Group = -> [Ga_element002]
  conduct = 2
  density = 1
  expand = 3
  formula = Ga
  name = G4_Ga
  specific = 4
FEATURE [App::DocumentObjectGroupPython] Ge_element002  label="Ge_element : 1"  # scripted group (container) (typed FeaturePython)
  n = 1
  ref = Ge_element
FEATURE [App::DocumentObjectGroupPython] G4_Ge  # scripted group (container) (typed FeaturePython)
  Dunit = g/cm3
  Dvalue = 5.323
  Group = -> [Ge_element002]
  conduct = 2
  density = 1
  expand = 3
  formula = Ge
  name = G4_Ge
  specific = 4
FEATURE [App::DocumentObjectGroupPython] As_element003  label="As_element : 002"  # scripted group (container) (typed FeaturePython)
  n = 1
  ref = As_element
FEATURE [App::DocumentObjectGroupPython] G4_As  # scripted group (container) (typed FeaturePython)
  Dunit = g/cm3
  Dvalue = 5.73
  Group = -> [As_element003]
  conduct = 2
  density = 1
  expand = 3
  formula = As
  name = G4_As
  specific = 4
FEATURE [App::DocumentObjectGroupPython] Se_element001  label="Se_element : 1"  # scripted group (container) (typed FeaturePython)
  n = 1
  ref = Se_element
FEATURE [App::DocumentObjectGroupPython] G4_Se  # scripted group (container) (typed FeaturePython)
  Dunit = g/cm3
  Dvalue = 4.5
  Group = -> [Se_element001]
  conduct = 2
  density = 1
  expand = 3
  formula = Se
  name = G4_Se
  specific = 4
FEATURE [App::DocumentObjectGroupPython] Br_element007  label="Br_element : 004"  # scripted group (container) (typed FeaturePython)
  n = 1
  ref = Br_element
FEATURE [App::DocumentObjectGroupPython] G4_Br  # scripted group (container) (typed FeaturePython)
  Dunit = g/cm3
  Dvalue = 0.0070721
  Group = -> [Br_element007]
  conduct = 2
  density = 1
  expand = 3
  formula = Br
  name = G4_Br
  specific = 4
FEATURE [App::DocumentObjectGroupPython] Kr_element001  label="Kr_element : 1"  # scripted group (container) (typed FeaturePython)
  n = 1
  ref = Kr_element
FEATURE [App::DocumentObjectGroupPython] G4_Kr  # scripted group (container) (typed FeaturePython)
  Dunit = g/cm3
  Dvalue = 0.00347832
  Group = -> [Kr_element001]
  conduct = 2
  density = 1
  expand = 3
  formula = Kr
  name = G4_Kr
  specific = 4
FEATURE [App::DocumentObjectGroupPython] Rb_element001  label="Rb_element : 1"  # scripted group (container) (typed FeaturePython)
  n = 1
  ref = Rb_element
FEATURE [App::DocumentObjectGroupPython] G4_Rb  # scripted group (container) (typed FeaturePython)
  Dunit = g/cm3
  Dvalue = 1.532
  Group = -> [Rb_element001]
  conduct = 2
  density = 1
  expand = 3
  formula = Rb
  name = G4_Rb
  specific = 4
FEATURE [App::DocumentObjectGroupPython] Sr_element001  label="Sr_element : 1"  # scripted group (container) (typed FeaturePython)
  n = 1
  ref = Sr_element
FEATURE [App::DocumentObjectGroupPython] G4_Sr  # scripted group (container) (typed FeaturePython)
  Dunit = g/cm3
  Dvalue = 2.54
  Group = -> [Sr_element001]
  conduct = 2
  density = 1
  expand = 3
  formula = Sr
  name = G4_Sr
  specific = 4
FEATURE [App::DocumentObjectGroupPython] Y_element001  label="Y_element : 1"  # scripted group (container) (typed FeaturePython)
  n = 1
  ref = Y_element
FEATURE [App::DocumentObjectGroupPython] G4_Y  # scripted group (container) (typed FeaturePython)
  Dunit = g/cm3
  Dvalue = 4.469
  Group = -> [Y_element001]
  conduct = 2
  density = 1
  expand = 3
  formula = Y
  name = G4_Y
  specific = 4
FEATURE [App::DocumentObjectGroupPython] Zr_element001  label="Zr_element : 1"  # scripted group (container) (typed FeaturePython)
  n = 1
  ref = Zr_element
FEATURE [App::DocumentObjectGroupPython] G4_Zr  # scripted group (container) (typed FeaturePython)
  Dunit = g/cm3
  Dvalue = 6.506
  Group = -> [Zr_element001]
  conduct = 2
  density = 1
  expand = 3
  formula = Zr
  name = G4_Zr
  specific = 4
FEATURE [App::DocumentObjectGroupPython] Nb_element001  label="Nb_element : 1"  # scripted group (container) (typed FeaturePython)
  n = 1
  ref = Nb_element
FEATURE [App::DocumentObjectGroupPython] G4_Nb  # scripted group (container) (typed FeaturePython)
  Dunit = g/cm3
  Dvalue = 8.57
  Group = -> [Nb_element001]
  conduct = 2
  density = 1
  expand = 3
  formula = Nb
  name = G4_Nb
  specific = 4
FEATURE [App::DocumentObjectGroupPython] Mo_element001  label="Mo_element : 1"  # scripted group (container) (typed FeaturePython)
  n = 1
  ref = Mo_element
FEATURE [App::DocumentObjectGroupPython] G4_Mo  # scripted group (container) (typed FeaturePython)
  Dunit = g/cm3
  Dvalue = 10.22
  Group = -> [Mo_element001]
  conduct = 2
  density = 1
  expand = 3
  formula = Mo
  name = G4_Mo
  specific = 4
FEATURE [App::DocumentObjectGroupPython] Tc_element001  label="Tc_element : 1"  # scripted group (container) (typed FeaturePython)
  n = 1
  ref = Tc_element
FEATURE [App::DocumentObjectGroupPython] G4_Tc  # scripted group (container) (typed FeaturePython)
  Dunit = g/cm3
  Dvalue = 11.5
  Group = -> [Tc_element001]
  conduct = 2
  density = 1
  expand = 3
  formula = Tc
  name = G4_Tc
  specific = 4
FEATURE [App::DocumentObjectGroupPython] Ru_element001  label="Ru_element : 1"  # scripted group (container) (typed FeaturePython)
  n = 1
  ref = Ru_element
FEATURE [App::DocumentObjectGroupPython] G4_Ru  # scripted group (container) (typed FeaturePython)
  Dunit = g/cm3
  Dvalue = 12.41
  Group = -> [Ru_element001]
  conduct = 2
  density = 1
  expand = 3
  formula = Ru
  name = G4_Ru
  specific = 4
FEATURE [App::DocumentObjectGroupPython] Rh_element001  label="Rh_element : 1"  # scripted group (container) (typed FeaturePython)
  n = 1
  ref = Rh_element
FEATURE [App::DocumentObjectGroupPython] G4_Rh  # scripted group (container) (typed FeaturePython)
  Dunit = g/cm3
  Dvalue = 12.41
  Group = -> [Rh_element001]
  conduct = 2
  density = 1
  expand = 3
  formula = Rh
  name = G4_Rh
  specific = 4
FEATURE [App::DocumentObjectGroupPython] Pd_element001  label="Pd_element : 1"  # scripted group (container) (typed FeaturePython)
  n = 1
  ref = Pd_element
FEATURE [App::DocumentObjectGroupPython] G4_Pd  # scripted group (container) (typed FeaturePython)
  Dunit = g/cm3
  Dvalue = 12.02
  Group = -> [Pd_element001]
  conduct = 2
  density = 1
  expand = 3
  formula = Pd
  name = G4_Pd
  specific = 4
FEATURE [App::DocumentObjectGroupPython] Ag_element006  label="Ag_element : 004"  # scripted group (container) (typed FeaturePython)
  n = 1
  ref = Ag_element
FEATURE [App::DocumentObjectGroupPython] G4_Ag  # scripted group (container) (typed FeaturePython)
  Dunit = g/cm3
  Dvalue = 10.5
  Group = -> [Ag_element006]
  conduct = 2
  density = 1
  expand = 3
  formula = Ag
  name = G4_Ag
  specific = 4
FEATURE [App::DocumentObjectGroupPython] Cd_element003  label="Cd_element : 003"  # scripted group (container) (typed FeaturePython)
  n = 1
  ref = Cd_element
FEATURE [App::DocumentObjectGroupPython] G4_Cd  # scripted group (container) (typed FeaturePython)
  Dunit = g/cm3
  Dvalue = 8.65
  Group = -> [Cd_element003]
  conduct = 2
  density = 1
  expand = 3
  formula = Cd
  name = G4_Cd
  specific = 4
FEATURE [App::DocumentObjectGroupPython] In_element001  label="In_element : 1"  # scripted group (container) (typed FeaturePython)
  n = 1
  ref = In_element
FEATURE [App::DocumentObjectGroupPython] G4_In  # scripted group (container) (typed FeaturePython)
  Dunit = g/cm3
  Dvalue = 7.31
  Group = -> [In_element001]
  conduct = 2
  density = 1
  expand = 3
  formula = In
  name = G4_In
  specific = 4
FEATURE [App::DocumentObjectGroupPython] Sn_element001  label="Sn_element : 1"  # scripted group (container) (typed FeaturePython)
  n = 1
  ref = Sn_element
FEATURE [App::DocumentObjectGroupPython] G4_Sn  # scripted group (container) (typed FeaturePython)
  Dunit = g/cm3
  Dvalue = 7.31
  Group = -> [Sn_element001]
  conduct = 2
  density = 1
  expand = 3
  formula = Sn
  name = G4_Sn
  specific = 4
FEATURE [App::DocumentObjectGroupPython] Sb_element001  label="Sb_element : 1"  # scripted group (container) (typed FeaturePython)
  n = 1
  ref = Sb_element
FEATURE [App::DocumentObjectGroupPython] G4_Sb  # scripted group (container) (typed FeaturePython)
  Dunit = g/cm3
  Dvalue = 6.691
  Group = -> [Sb_element001]
  conduct = 2
  density = 1
  expand = 3
  formula = Sb
  name = G4_Sb
  specific = 4
FEATURE [App::DocumentObjectGroupPython] Te_element002  label="Te_element : 002"  # scripted group (container) (typed FeaturePython)
  n = 1
  ref = Te_element
FEATURE [App::DocumentObjectGroupPython] G4_Te  # scripted group (container) (typed FeaturePython)
  Dunit = g/cm3
  Dvalue = 6.24
  Group = -> [Te_element002]
  conduct = 2
  density = 1
  expand = 3
  formula = Te
  name = G4_Te
  specific = 4
FEATURE [App::DocumentObjectGroupPython] I_element010  label="I_element : 006"  # scripted group (container) (typed FeaturePython)
  n = 1
  ref = I_element
FEATURE [App::DocumentObjectGroupPython] G4_I  # scripted group (container) (typed FeaturePython)
  Dunit = g/cm3
  Dvalue = 4.93
  Group = -> [I_element010]
  conduct = 2
  density = 1
  expand = 3
  formula = I
  name = G4_I
  specific = 4
FEATURE [App::DocumentObjectGroupPython] Xe_element001  label="Xe_element : 1"  # scripted group (container) (typed FeaturePython)
  n = 1
  ref = Xe_element
FEATURE [App::DocumentObjectGroupPython] G4_Xe  # scripted group (container) (typed FeaturePython)
  Dunit = g/cm3
  Dvalue = 0.00548536
  Group = -> [Xe_element001]
  conduct = 2
  density = 1
  expand = 3
  formula = Xe
  name = G4_Xe
  specific = 4
FEATURE [App::DocumentObjectGroupPython] Cs_element003  label="Cs_element : 003"  # scripted group (container) (typed FeaturePython)
  n = 1
  ref = Cs_element
FEATURE [App::DocumentObjectGroupPython] G4_Cs  # scripted group (container) (typed FeaturePython)
  Dunit = g/cm3
  Dvalue = 1.873
  Group = -> [Cs_element003]
  conduct = 2
  density = 1
  expand = 3
  formula = Cs
  name = G4_Cs
  specific = 4
FEATURE [App::DocumentObjectGroupPython] Ba_element003  label="Ba_element : 003"  # scripted group (container) (typed FeaturePython)
  n = 1
  ref = Ba_element
FEATURE [App::DocumentObjectGroupPython] G4_Ba  # scripted group (container) (typed FeaturePython)
  Dunit = g/cm3
  Dvalue = 3.5
  Group = -> [Ba_element003]
  conduct = 2
  density = 1
  expand = 3
  formula = Ba
  name = G4_Ba
  specific = 4
FEATURE [App::DocumentObjectGroupPython] La_element003  label="La_element : 003"  # scripted group (container) (typed FeaturePython)
  n = 1
  ref = La_element
FEATURE [App::DocumentObjectGroupPython] G4_La  # scripted group (container) (typed FeaturePython)
  Dunit = g/cm3
  Dvalue = 6.154
  Group = -> [La_element003]
  conduct = 2
  density = 1
  expand = 3
  formula = La
  name = G4_La
  specific = 4
FEATURE [App::DocumentObjectGroupPython] Ce_element002  label="Ce_element : 1"  # scripted group (container) (typed FeaturePython)
  n = 1
  ref = Ce_element
FEATURE [App::DocumentObjectGroupPython] G4_Ce  # scripted group (container) (typed FeaturePython)
  Dunit = g/cm3
  Dvalue = 6.657
  Group = -> [Ce_element002]
  conduct = 2
  density = 1
  expand = 3
  formula = Ce
  name = G4_Ce
  specific = 4
FEATURE [App::DocumentObjectGroupPython] Pr_element001  label="Pr_element : 1"  # scripted group (container) (typed FeaturePython)
  n = 1
  ref = Pr_element
FEATURE [App::DocumentObjectGroupPython] G4_Pr  # scripted group (container) (typed FeaturePython)
  Dunit = g/cm3
  Dvalue = 6.71
  Group = -> [Pr_element001]
  conduct = 2
  density = 1
  expand = 3
  formula = Pr
  name = G4_Pr
  specific = 4
FEATURE [App::DocumentObjectGroupPython] Nd_element001  label="Nd_element : 1"  # scripted group (container) (typed FeaturePython)
  n = 1
  ref = Nd_element
FEATURE [App::DocumentObjectGroupPython] G4_Nd  # scripted group (container) (typed FeaturePython)
  Dunit = g/cm3
  Dvalue = 6.9
  Group = -> [Nd_element001]
  conduct = 2
  density = 1
  expand = 3
  formula = Nd
  name = G4_Nd
  specific = 4
FEATURE [App::DocumentObjectGroupPython] Pm_element001  label="Pm_element : 1"  # scripted group (container) (typed FeaturePython)
  n = 1
  ref = Pm_element
FEATURE [App::DocumentObjectGroupPython] G4_Pm  # scripted group (container) (typed FeaturePython)
  Dunit = g/cm3
  Dvalue = 7.22
  Group = -> [Pm_element001]
  conduct = 2
  density = 1
  expand = 3
  formula = Pm
  name = G4_Pm
  specific = 4
FEATURE [App::DocumentObjectGroupPython] Sm_element001  label="Sm_element : 1"  # scripted group (container) (typed FeaturePython)
  n = 1
  ref = Sm_element
FEATURE [App::DocumentObjectGroupPython] G4_Sm  # scripted group (container) (typed FeaturePython)
  Dunit = g/cm3
  Dvalue = 7.46
  Group = -> [Sm_element001]
  conduct = 2
  density = 1
  expand = 3
  formula = Sm
  name = G4_Sm
  specific = 4
FEATURE [App::DocumentObjectGroupPython] Eu_element001  label="Eu_element : 1"  # scripted group (container) (typed FeaturePython)
  n = 1
  ref = Eu_element
FEATURE [App::DocumentObjectGroupPython] G4_Eu  # scripted group (container) (typed FeaturePython)
  Dunit = g/cm3
  Dvalue = 5.243
  Group = -> [Eu_element001]
  conduct = 2
  density = 1
  expand = 3
  formula = Eu
  name = G4_Eu
  specific = 4
FEATURE [App::DocumentObjectGroupPython] Gd_element002  label="Gd_element : 1"  # scripted group (container) (typed FeaturePython)
  n = 1
  ref = Gd_element
FEATURE [App::DocumentObjectGroupPython] G4_Gd  # scripted group (container) (typed FeaturePython)
  Dunit = g/cm3
  Dvalue = 7.9004
  Group = -> [Gd_element002]
  conduct = 2
  density = 1
  expand = 3
  formula = Gd
  name = G4_Gd
  specific = 4
FEATURE [App::DocumentObjectGroupPython] Tb_element001  label="Tb_element : 1"  # scripted group (container) (typed FeaturePython)
  n = 1
  ref = Tb_element
FEATURE [App::DocumentObjectGroupPython] G4_Tb  # scripted group (container) (typed FeaturePython)
  Dunit = g/cm3
  Dvalue = 8.229
  Group = -> [Tb_element001]
  conduct = 2
  density = 1
  expand = 3
  formula = Tb
  name = G4_Tb
  specific = 4
FEATURE [App::DocumentObjectGroupPython] Dy_element001  label="Dy_element : 1"  # scripted group (container) (typed FeaturePython)
  n = 1
  ref = Dy_element
FEATURE [App::DocumentObjectGroupPython] G4_Dy  # scripted group (container) (typed FeaturePython)
  Dunit = g/cm3
  Dvalue = 8.55
  Group = -> [Dy_element001]
  conduct = 2
  density = 1
  expand = 3
  formula = Dy
  name = G4_Dy
  specific = 4
FEATURE [App::DocumentObjectGroupPython] Ho_element001  label="Ho_element : 1"  # scripted group (container) (typed FeaturePython)
  n = 1
  ref = Ho_element
FEATURE [App::DocumentObjectGroupPython] G4_Ho  # scripted group (container) (typed FeaturePython)
  Dunit = g/cm3
  Dvalue = 8.795
  Group = -> [Ho_element001]
  conduct = 2
  density = 1
  expand = 3
  formula = Ho
  name = G4_Ho
  specific = 4
FEATURE [App::DocumentObjectGroupPython] Er_element001  label="Er_element : 1"  # scripted group (container) (typed FeaturePython)
  n = 1
  ref = Er_element
FEATURE [App::DocumentObjectGroupPython] G4_Er  # scripted group (container) (typed FeaturePython)
  Dunit = g/cm3
  Dvalue = 9.066
  Group = -> [Er_element001]
  conduct = 2
  density = 1
  expand = 3
  formula = Er
  name = G4_Er
  specific = 4
FEATURE [App::DocumentObjectGroupPython] Tm_element001  label="Tm_element : 1"  # scripted group (container) (typed FeaturePython)
  n = 1
  ref = Tm_element
FEATURE [App::DocumentObjectGroupPython] G4_Tm  # scripted group (container) (typed FeaturePython)
  Dunit = g/cm3
  Dvalue = 9.321
  Group = -> [Tm_element001]
  conduct = 2
  density = 1
  expand = 3
  formula = Tm
  name = G4_Tm
  specific = 4
FEATURE [App::DocumentObjectGroupPython] Yb_element001  label="Yb_element : 1"  # scripted group (container) (typed FeaturePython)
  n = 1
  ref = Yb_element
FEATURE [App::DocumentObjectGroupPython] G4_Yb  # scripted group (container) (typed FeaturePython)
  Dunit = g/cm3
  Dvalue = 6.73
  Group = -> [Yb_element001]
  conduct = 2
  density = 1
  expand = 3
  formula = Yb
  name = G4_Yb
  specific = 4
FEATURE [App::DocumentObjectGroupPython] Lu_element001  label="Lu_element : 1"  # scripted group (container) (typed FeaturePython)
  n = 1
  ref = Lu_element
FEATURE [App::DocumentObjectGroupPython] G4_Lu  # scripted group (container) (typed FeaturePython)
  Dunit = g/cm3
  Dvalue = 9.84
  Group = -> [Lu_element001]
  conduct = 2
  density = 1
  expand = 3
  formula = Lu
  name = G4_Lu
  specific = 4
FEATURE [App::DocumentObjectGroupPython] Hf_element001  label="Hf_element : 1"  # scripted group (container) (typed FeaturePython)
  n = 1
  ref = Hf_element
FEATURE [App::DocumentObjectGroupPython] G4_Hf  # scripted group (container) (typed FeaturePython)
  Dunit = g/cm3
  Dvalue = 13.31
  Group = -> [Hf_element001]
  conduct = 2
  density = 1
  expand = 3
  formula = Hf
  name = G4_Hf
  specific = 4
FEATURE [App::DocumentObjectGroupPython] Ta_element001  label="Ta_element : 1"  # scripted group (container) (typed FeaturePython)
  n = 1
  ref = Ta_element
FEATURE [App::DocumentObjectGroupPython] G4_Ta  # scripted group (container) (typed FeaturePython)
  Dunit = g/cm3
  Dvalue = 16.654
  Group = -> [Ta_element001]
  conduct = 2
  density = 1
  expand = 3
  formula = Ta
  name = G4_Ta
  specific = 4
FEATURE [App::DocumentObjectGroupPython] W_element004  label="W_element : 004"  # scripted group (container) (typed FeaturePython)
  n = 1
  ref = W_element
FEATURE [App::DocumentObjectGroupPython] G4_W  # scripted group (container) (typed FeaturePython)
  Dunit = g/cm3
  Dvalue = 19.3
  Group = -> [W_element004]
  conduct = 2
  density = 1
  expand = 3
  formula = W
  name = G4_W
  specific = 4
FEATURE [App::DocumentObjectGroupPython] Re_element001  label="Re_element : 1"  # scripted group (container) (typed FeaturePython)
  n = 1
  ref = Re_element
FEATURE [App::DocumentObjectGroupPython] G4_Re  # scripted group (container) (typed FeaturePython)
  Dunit = g/cm3
  Dvalue = 21.02
  Group = -> [Re_element001]
  conduct = 2
  density = 1
  expand = 3
  formula = Re
  name = G4_Re
  specific = 4
FEATURE [App::DocumentObjectGroupPython] Os_element001  label="Os_element : 1"  # scripted group (container) (typed FeaturePython)
  n = 1
  ref = Os_element
FEATURE [App::DocumentObjectGroupPython] G4_Os  # scripted group (container) (typed FeaturePython)
  Dunit = g/cm3
  Dvalue = 22.57
  Group = -> [Os_element001]
  conduct = 2
  density = 1
  expand = 3
  formula = Os
  name = G4_Os
  specific = 4
FEATURE [App::DocumentObjectGroupPython] Ir_element001  label="Ir_element : 1"  # scripted group (container) (typed FeaturePython)
  n = 1
  ref = Ir_element
FEATURE [App::DocumentObjectGroupPython] G4_Ir  # scripted group (container) (typed FeaturePython)
  Dunit = g/cm3
  Dvalue = 22.42
  Group = -> [Ir_element001]
  conduct = 2
  density = 1
  expand = 3
  formula = Ir
  name = G4_Ir
  specific = 4
FEATURE [App::DocumentObjectGroupPython] Pt_element001  label="Pt_element : 1"  # scripted group (container) (typed FeaturePython)
  n = 1
  ref = Pt_element
FEATURE [App::DocumentObjectGroupPython] G4_Pt  # scripted group (container) (typed FeaturePython)
  Dunit = g/cm3
  Dvalue = 21.45
  Group = -> [Pt_element001]
  conduct = 2
  density = 1
  expand = 3
  formula = Pt
  name = G4_Pt
  specific = 4
FEATURE [App::DocumentObjectGroupPython] Au_element001  label="Au_element : 1"  # scripted group (container) (typed FeaturePython)
  n = 1
  ref = Au_element
FEATURE [App::DocumentObjectGroupPython] G4_Au  # scripted group (container) (typed FeaturePython)
  Dunit = g/cm3
  Dvalue = 19.32
  Group = -> [Au_element001]
  conduct = 2
  density = 1
  expand = 3
  formula = Au
  name = G4_Au
  specific = 4
FEATURE [App::DocumentObjectGroupPython] Hg_element002  label="Hg_element : 002"  # scripted group (container) (typed FeaturePython)
  n = 1
  ref = Hg_element
FEATURE [App::DocumentObjectGroupPython] G4_Hg  # scripted group (container) (typed FeaturePython)
  Dunit = g/cm3
  Dvalue = 13.546
  Group = -> [Hg_element002]
  conduct = 2
  density = 1
  expand = 3
  formula = Hg
  name = G4_Hg
  specific = 4
FEATURE [App::DocumentObjectGroupPython] Tl_element002  label="Tl_element : 002"  # scripted group (container) (typed FeaturePython)
  n = 1
  ref = Tl_element
FEATURE [App::DocumentObjectGroupPython] G4_Tl  # scripted group (container) (typed FeaturePython)
  Dunit = g/cm3
  Dvalue = 11.72
  Group = -> [Tl_element002]
  conduct = 2
  density = 1
  expand = 3
  formula = Tl
  name = G4_Tl
  specific = 4
FEATURE [App::DocumentObjectGroupPython] Pb_element003  label="Pb_element : 1"  # scripted group (container) (typed FeaturePython)
  n = 1
  ref = Pb_element
FEATURE [App::DocumentObjectGroupPython] G4_Pb  # scripted group (container) (typed FeaturePython)
  Dunit = g/cm3
  Dvalue = 11.35
  Group = -> [Pb_element003]
  conduct = 2
  density = 1
  expand = 3
  formula = Pb
  name = G4_Pb
  specific = 4
FEATURE [App::DocumentObjectGroupPython] Bi_element002  label="Bi_element : 1"  # scripted group (container) (typed FeaturePython)
  n = 1
  ref = Bi_element
FEATURE [App::DocumentObjectGroupPython] G4_Bi  # scripted group (container) (typed FeaturePython)
  Dunit = g/cm3
  Dvalue = 9.747
  Group = -> [Bi_element002]
  conduct = 2
  density = 1
  expand = 3
  formula = Bi
  name = G4_Bi
  specific = 4
FEATURE [App::DocumentObjectGroupPython] Po_element001  label="Po_element : 1"  # scripted group (container) (typed FeaturePython)
  n = 1
  ref = Po_element
FEATURE [App::DocumentObjectGroupPython] G4_Po  # scripted group (container) (typed FeaturePython)
  Dunit = g/cm3
  Dvalue = 9.32
  Group = -> [Po_element001]
  conduct = 2
  density = 1
  expand = 3
  formula = Po
  name = G4_Po
  specific = 4
FEATURE [App::DocumentObjectGroupPython] At_element001  label="At_element : 1"  # scripted group (container) (typed FeaturePython)
  n = 1
  ref = At_element
FEATURE [App::DocumentObjectGroupPython] G4_At  # scripted group (container) (typed FeaturePython)
  Dunit = g/cm3
  Dvalue = 9.32
  Group = -> [At_element001]
  conduct = 2
  density = 1
  expand = 3
  formula = At
  name = G4_At
  specific = 4
FEATURE [App::DocumentObjectGroupPython] Rn_element001  label="Rn_element : 1"  # scripted group (container) (typed FeaturePython)
  n = 1
  ref = Rn_element
FEATURE [App::DocumentObjectGroupPython] G4_Rn  # scripted group (container) (typed FeaturePython)
  Dunit = g/cm3
  Dvalue = 0.00900662
  Group = -> [Rn_element001]
  conduct = 2
  density = 1
  expand = 3
  formula = Rn
  name = G4_Rn
  specific = 4
FEATURE [App::DocumentObjectGroupPython] Fr_element001  label="Fr_element : 1"  # scripted group (container) (typed FeaturePython)
  n = 1
  ref = Fr_element
FEATURE [App::DocumentObjectGroupPython] G4_Fr  # scripted group (container) (typed FeaturePython)
  Dunit = g/cm3
  Dvalue = 1
  Group = -> [Fr_element001]
  conduct = 2
  density = 1
  expand = 3
  formula = Fr
  name = G4_Fr
  specific = 4
FEATURE [App::DocumentObjectGroupPython] Ra_element001  label="Ra_element : 1"  # scripted group (container) (typed FeaturePython)
  n = 1
  ref = Ra_element
FEATURE [App::DocumentObjectGroupPython] G4_Ra  # scripted group (container) (typed FeaturePython)
  Dunit = g/cm3
  Dvalue = 5
  Group = -> [Ra_element001]
  conduct = 2
  density = 1
  expand = 3
  formula = Ra
  name = G4_Ra
  specific = 4
FEATURE [App::DocumentObjectGroupPython] Ac_element001  label="Ac_element : 1"  # scripted group (container) (typed FeaturePython)
  n = 1
  ref = Ac_element
FEATURE [App::DocumentObjectGroupPython] G4_Ac  # scripted group (container) (typed FeaturePython)
  Dunit = g/cm3
  Dvalue = 10.07
  Group = -> [Ac_element001]
  conduct = 2
  density = 1
  expand = 3
  formula = Ac
  name = G4_Ac
  specific = 4
FEATURE [App::DocumentObjectGroupPython] Th_element001  label="Th_element : 1"  # scripted group (container) (typed FeaturePython)
  n = 1
  ref = Th_element
FEATURE [App::DocumentObjectGroupPython] G4_Th  # scripted group (container) (typed FeaturePython)
  Dunit = g/cm3
  Dvalue = 11.72
  Group = -> [Th_element001]
  conduct = 2
  density = 1
  expand = 3
  formula = Th
  name = G4_Th
  specific = 4
FEATURE [App::DocumentObjectGroupPython] Pa_element001  label="Pa_element : 1"  # scripted group (container) (typed FeaturePython)
  n = 1
  ref = Pa_element
FEATURE [App::DocumentObjectGroupPython] G4_Pa  # scripted group (container) (typed FeaturePython)
  Dunit = g/cm3
  Dvalue = 15.37
  Group = -> [Pa_element001]
  conduct = 2
  density = 1
  expand = 3
  formula = Pa
  name = G4_Pa
  specific = 4
FEATURE [App::DocumentObjectGroupPython] U_element004  label="U_element : 004"  # scripted group (container) (typed FeaturePython)
  n = 1
  ref = U_element
FEATURE [App::DocumentObjectGroupPython] G4_U  # scripted group (container) (typed FeaturePython)
  Dunit = g/cm3
  Dvalue = 18.95
  Group = -> [U_element004]
  conduct = 2
  density = 1
  expand = 3
  formula = U
  name = G4_U
  specific = 4
FEATURE [App::DocumentObjectGroupPython] Np_element001  label="Np_element : 1"  # scripted group (container) (typed FeaturePython)
  n = 1
  ref = Np_element
FEATURE [App::DocumentObjectGroupPython] G4_Np  # scripted group (container) (typed FeaturePython)
  Dunit = g/cm3
  Dvalue = 20.25
  Group = -> [Np_element001]
  conduct = 2
  density = 1
  expand = 3
  formula = Np
  name = G4_Np
  specific = 4
FEATURE [App::DocumentObjectGroupPython] Pu_element002  label="Pu_element : 002"  # scripted group (container) (typed FeaturePython)
  n = 1
  ref = Pu_element
FEATURE [App::DocumentObjectGroupPython] G4_Pu  # scripted group (container) (typed FeaturePython)
  Dunit = g/cm3
  Dvalue = 19.84
  Group = -> [Pu_element002]
  conduct = 2
  density = 1
  expand = 3
  formula = Pu
  name = G4_Pu
  specific = 4
FEATURE [App::DocumentObjectGroupPython] Am_element001  label="Am_element : 1"  # scripted group (container) (typed FeaturePython)
  n = 1
  ref = Am_element
FEATURE [App::DocumentObjectGroupPython] G4_Am  # scripted group (container) (typed FeaturePython)
  Dunit = g/cm3
  Dvalue = 13.67
  Group = -> [Am_element001]
  conduct = 2
  density = 1
  expand = 3
  formula = Am
  name = G4_Am
  specific = 4
FEATURE [App::DocumentObjectGroupPython] Cm_element001  label="Cm_element : 1"  # scripted group (container) (typed FeaturePython)
  n = 1
  ref = Cm_element
FEATURE [App::DocumentObjectGroupPython] G4_Cm  # scripted group (container) (typed FeaturePython)
  Dunit = g/cm3
  Dvalue = 13.51
  Group = -> [Cm_element001]
  conduct = 2
  density = 1
  expand = 3
  formula = Cm
  name = G4_Cm
  specific = 4
FEATURE [App::DocumentObjectGroupPython] Bk_element001  label="Bk_element : 1"  # scripted group (container) (typed FeaturePython)
  n = 1
  ref = Bk_element
FEATURE [App::DocumentObjectGroupPython] G4_Bk  # scripted group (container) (typed FeaturePython)
  Dunit = g/cm3
  Dvalue = 14
  Group = -> [Bk_element001]
  conduct = 2
  density = 1
  expand = 3
  formula = Bk
  name = G4_Bk
  specific = 4
FEATURE [App::DocumentObjectGroupPython] Cf_element001  label="Cf_element : 1"  # scripted group (container) (typed FeaturePython)
  n = 1
  ref = Cf_element
FEATURE [App::DocumentObjectGroupPython] G4_Cf  # scripted group (container) (typed FeaturePython)
  Dunit = g/cm3
  Dvalue = 10
  Group = -> [Cf_element001]
  conduct = 2
  density = 1
  expand = 3
  formula = Cf
  name = G4_Cf
  specific = 4
FEATURE [App::DocumentObjectGroupPython] Element  # scripted group (container) (typed FeaturePython)
  Group = -> [G4_H,G4_He,G4_Li,G4_Be,G4_B,G4_C,G4_N,G4_O,G4_F,G4_Ne,G4_Na,G4_Mg,G4_Al,G4_Si,G4_P,G4_S,G4_Cl,G4_Ar,G4_K,G4_Ca,G4_Sc,G4_Ti,G4_V,G4_Cr,G4_Mn,G4_Fe,G4_Co,G4_Ni,G4_Cu,G4_Zn,G4_Ga,G4_Ge,G4_As,G4_Se,G4_Br,G4_Kr,G4_Rb,G4_Sr,G4_Y,G4_Zr,G4_Nb,G4_Mo,G4_Tc,G4_Ru,G4_Rh,G4_Pd,G4_Ag,G4_Cd,G4_In,G4_Sn,G4_Sb,G4_Te,G4_I,G4_Xe,G4_Cs,G4_Ba,G4_La,G4_Ce,G4_Pr,G4_Nd,G4_Pm,G4_Sm,G4_Eu,G4_Gd,G4_Tb,G4_Dy,G4_Ho,G4_Er,+30 more]
FEATURE [App::DocumentObjectGroupPython] H_element114  label="H_element : 063"  # scripted group (container) (typed FeaturePython)
  n = 2
  ref = H_element
FEATURE [App::DocumentObjectGroupPython] G4_lH2  # scripted group (container) (typed FeaturePython)
  Dunit = g/cm3
  Dvalue = 0.0708
  Group = -> [H_element114]
  conduct = 2
  density = 1
  expand = 3
  formula = G4_lH2
  name = G4_lH2
  specific = 4
FEATURE [App::DocumentObjectGroupPython] N_element049  label="N_element : 022"  # scripted group (container) (typed FeaturePython)
  n = 2
  ref = N_element
FEATURE [App::DocumentObjectGroupPython] G4_lN2  # scripted group (container) (typed FeaturePython)
  Dunit = g/cm3
  Dvalue = 0.807
  Group = -> [N_element049]
  conduct = 2
  density = 1
  expand = 3
  formula = G4_lN2
  name = G4_lN2
  specific = 4
FEATURE [App::DocumentObjectGroupPython] O_element106  label="O_element : 060"  # scripted group (container) (typed FeaturePython)
  n = 2
  ref = O_element
FEATURE [App::DocumentObjectGroupPython] G4_lO2  # scripted group (container) (typed FeaturePython)
  Dunit = g/cm3
  Dvalue = 1.141
  Group = -> [O_element106]
  conduct = 2
  density = 1
  expand = 3
  formula = G4_lO2
  name = G4_lO2
  specific = 4
FEATURE [App::DocumentObjectGroupPython] Ar  label="Ar : 1"  # scripted group (container) (typed FeaturePython)
  n = 1
  ref = Ar
FEATURE [App::DocumentObjectGroupPython] G4_lAr  # scripted group (container) (typed FeaturePython)
  Dunit = g/cm3
  Dvalue = 1.396
  Group = -> [Ar]
  conduct = 2
  density = 1
  expand = 3
  formula = G4_lAr
  name = G4_lAr
  specific = 4
FEATURE [App::DocumentObjectGroupPython] Br  label="Br : 1"  # scripted group (container) (typed FeaturePython)
  n = 1
  ref = Br
FEATURE [App::DocumentObjectGroupPython] G4_lBr  # scripted group (container) (typed FeaturePython)
  Dunit = g/cm3
  Dvalue = 3.1028
  Group = -> [Br]
  conduct = 2
  density = 1
  expand = 3
  formula = G4_lBr
  name = G4_lBr
  specific = 4
FEATURE [App::DocumentObjectGroupPython] Kr  label="Kr : 1"  # scripted group (container) (typed FeaturePython)
  n = 1
  ref = Kr
FEATURE [App::DocumentObjectGroupPython] G4_lKr  # scripted group (container) (typed FeaturePython)
  Dunit = g/cm3
  Dvalue = 2.418
  Group = -> [Kr]
  conduct = 2
  density = 1
  expand = 3
  formula = G4_lKr
  name = G4_lKr
  specific = 4
FEATURE [App::DocumentObjectGroupPython] Xe  label="Xe : 1"  # scripted group (container) (typed FeaturePython)
  n = 1
  ref = Xe
FEATURE [App::DocumentObjectGroupPython] G4_lXe  # scripted group (container) (typed FeaturePython)
  Dunit = g/cm3
  Dvalue = 2.953
  Group = -> [Xe]
  conduct = 2
  density = 1
  expand = 3
  formula = G4_lXe
  name = G4_lXe
  specific = 4
FEATURE [App::DocumentObjectGroupPython] O_element107  label="O_element : 061"  # scripted group (container) (typed FeaturePython)
  n = 4
  ref = O_element
FEATURE [App::DocumentObjectGroupPython] Pb_element004  label="Pb_element : 002"  # scripted group (container) (typed FeaturePython)
  n = 1
  ref = Pb_element
FEATURE [App::DocumentObjectGroupPython] W_element005  label="W_element : 005"  # scripted group (container) (typed FeaturePython)
  n = 1
  ref = W_element
FEATURE [App::DocumentObjectGroupPython] G4_PbWO4  # scripted group (container) (typed FeaturePython)
  Dunit = g/cm3
  Dvalue = 8.28
  Group = -> [O_element107,Pb_element004,W_element005]
  conduct = 2
  density = 1
  expand = 3
  formula = G4_PbWO4
  name = G4_PbWO4
  specific = 4
FEATURE [App::DocumentObjectGroupPython] alactic  label="alactic : 1"  # scripted group (container) (typed FeaturePython)
  n = 1
  ref = alactic
FEATURE [App::DocumentObjectGroupPython] G4_Galactic  # scripted group (container) (typed FeaturePython)
  Dunit = g/cm3
  Dvalue = 0
  Group = -> [alactic]
  conduct = 2
  density = 1
  expand = 3
  formula = G4_Galactic
  name = G4_Galactic
  specific = 4
FEATURE [App::DocumentObjectGroupPython] RAPHITE_POROUS  label="RAPHITE_POROUS : 1"  # scripted group (container) (typed FeaturePython)
  n = 1
  ref = RAPHITE_POROUS
FEATURE [App::DocumentObjectGroupPython] G4_GRAPHITE_POROUS  # scripted group (container) (typed FeaturePython)
  Dunit = g/cm3
  Dvalue = 1.7
  Group = -> [RAPHITE_POROUS]
  conduct = 2
  density = 1
  expand = 3
  formula = G4_GRAPHITE_POROUS
  name = G4_GRAPHITE_POROUS
  specific = 4
FEATURE [App::DocumentObjectGroupPython] H_element115  label="H_element : 0.150"  # scripted group (container) (typed FeaturePython)
  n = 0.080538
FEATURE [App::DocumentObjectGroupPython] C_element125  label="C_element : 0.600"  # scripted group (container) (typed FeaturePython)
  n = 0.599848
FEATURE [App::DocumentObjectGroupPython] O_element108  label="O_element : 0.320"  # scripted group (container) (typed FeaturePython)
  n = 0.319614
FEATURE [App::DocumentObjectGroupPython] G4_LUCITE  # scripted group (container) (typed FeaturePython)
  Dunit = g/cm3
  Dvalue = 1.19
  Group = -> [H_element115,C_element125,O_element108]
  conduct = 2
  density = 1
  expand = 3
  formula = G4_LUCITE
  name = G4_LUCITE
  specific = 4
FEATURE [App::DocumentObjectGroupPython] Cu_element002  label="Cu_element : 62"  # scripted group (container) (typed FeaturePython)
  n = 62
  ref = Cu_element
FEATURE [App::DocumentObjectGroupPython] Zn_element002  label="Zn_element : 35"  # scripted group (container) (typed FeaturePython)
  n = 35
  ref = Zn_element
FEATURE [App::DocumentObjectGroupPython] Pb_element005  label="Pb_element : 3"  # scripted group (container) (typed FeaturePython)
  n = 3
  ref = Pb_element
FEATURE [App::DocumentObjectGroupPython] G4_BRASS  # scripted group (container) (typed FeaturePython)
  Dunit = g/cm3
  Dvalue = 8.52
  Group = -> [Cu_element002,Zn_element002,Pb_element005]
  conduct = 2
  density = 1
  expand = 3
  formula = G4_BRASS
  name = G4_BRASS
  specific = 4
FEATURE [App::DocumentObjectGroupPython] Cu_element003  label="Cu_element : 89"  # scripted group (container) (typed FeaturePython)
  n = 89
  ref = Cu_element
FEATURE [App::DocumentObjectGroupPython] Zn_element003  label="Zn_element : 9"  # scripted group (container) (typed FeaturePython)
  n = 9
  ref = Zn_element
FEATURE [App::DocumentObjectGroupPython] Pb_element006  label="Pb_element : 2"  # scripted group (container) (typed FeaturePython)
  n = 2
  ref = Pb_element
FEATURE [App::DocumentObjectGroupPython] G4_BRONZE  # scripted group (container) (typed FeaturePython)
  Dunit = g/cm3
  Dvalue = 8.82
  Group = -> [Cu_element003,Zn_element003,Pb_element006]
  conduct = 2
  density = 1
  expand = 3
  formula = G4_BRONZE
  name = G4_BRONZE
  specific = 4
FEATURE [App::DocumentObjectGroupPython] Fe_element008  label="Fe_element : 74"  # scripted group (container) (typed FeaturePython)
  n = 74
  ref = Fe_element
FEATURE [App::DocumentObjectGroupPython] Cr_element002  label="Cr_element : 18"  # scripted group (container) (typed FeaturePython)
  n = 18
  ref = Cr_element
FEATURE [App::DocumentObjectGroupPython] Ni_element002  label="Ni_element : 8"  # scripted group (container) (typed FeaturePython)
  n = 8
  ref = Ni_element
FEATURE [App::DocumentObjectGroupPython] G4_STAINLESS_STEEL  label="G4_STAINLESS-STEEL"  # scripted group (container) (typed FeaturePython)
  Dunit = g/cm3
  Dvalue = 8
  Group = -> [Fe_element008,Cr_element002,Ni_element002]
  conduct = 2
  density = 1
  expand = 3
  formula = G4_STAINLESS-STEEL
  name = G4_STAINLESS-STEEL
  specific = 4
FEATURE [App::DocumentObjectGroupPython] H_element116  label="H_element : 064"  # scripted group (container) (typed FeaturePython)
  n = 18
  ref = H_element
FEATURE [App::DocumentObjectGroupPython] C_element126  label="C_element : 071"  # scripted group (container) (typed FeaturePython)
  n = 12
  ref = C_element
FEATURE [App::DocumentObjectGroupPython] O_element109  label="O_element : 062"  # scripted group (container) (typed FeaturePython)
  n = 7
  ref = O_element
FEATURE [App::DocumentObjectGroupPython] G4_CR39  # scripted group (container) (typed FeaturePython)
  Dunit = g/cm3
  Dvalue = 1.32
  Group = -> [H_element116,C_element126,O_element109]
  conduct = 2
  density = 1
  expand = 3
  formula = G4_CR39
  name = G4_CR39
  specific = 4
FEATURE [App::DocumentObjectGroupPython] H_element117  label="H_element : 38"  # scripted group (container) (typed FeaturePython)
  n = 38
  ref = H_element
FEATURE [App::DocumentObjectGroupPython] C_element127  label="C_element : 072"  # scripted group (container) (typed FeaturePython)
  n = 18
  ref = C_element
FEATURE [App::DocumentObjectGroupPython] O_element110  label="O_element : 063"  # scripted group (container) (typed FeaturePython)
  n = 1
  ref = O_element
FEATURE [App::DocumentObjectGroupPython] G4_OCTADECANOL  # scripted group (container) (typed FeaturePython)
  Dunit = g/cm3
  Dvalue = 0.812
  Group = -> [H_element117,C_element127,O_element110]
  conduct = 2
  density = 1
  expand = 3
  formula = G4_OCTADECANOL
  name = G4_OCTADECANOL
  specific = 4
FEATURE [App::DocumentObjectGroupPython] HEP  # scripted group (container) (typed FeaturePython)
  Group = -> [G4_lH2,G4_lN2,G4_lO2,G4_lAr,G4_lBr,G4_lKr,G4_lXe,G4_PbWO4,G4_Galactic,G4_GRAPHITE_POROUS,G4_LUCITE,G4_BRASS,G4_BRONZE,G4_STAINLESS_STEEL,G4_CR39,G4_OCTADECANOL]
FEATURE [App::DocumentObjectGroupPython] C_element128  label="C_element : 073"  # scripted group (container) (typed FeaturePython)
  n = 14
  ref = C_element
FEATURE [App::DocumentObjectGroupPython] H_element118  label="H_element : 065"  # scripted group (container) (typed FeaturePython)
  n = 10
  ref = H_element
FEATURE [App::DocumentObjectGroupPython] O_element111  label="O_element : 064"  # scripted group (container) (typed FeaturePython)
  n = 2
  ref = O_element
FEATURE [App::DocumentObjectGroupPython] N_element050  label="N_element : 023"  # scripted group (container) (typed FeaturePython)
  n = 2
  ref = N_element
FEATURE [App::DocumentObjectGroupPython] G4_KEVLAR  # scripted group (container) (typed FeaturePython)
  Dunit = g/cm3
  Dvalue = 1.44
  Group = -> [C_element128,H_element118,O_element111,N_element050]
  conduct = 2
  density = 1
  expand = 3
  formula = G4_KEVLAR
  name = G4_KEVLAR
  specific = 4
FEATURE [App::DocumentObjectGroupPython] C_element129  label="C_element : 074"  # scripted group (container) (typed FeaturePython)
  n = 10
  ref = C_element
FEATURE [App::DocumentObjectGroupPython] H_element119  label="H_element : 066"  # scripted group (container) (typed FeaturePython)
  n = 8
  ref = H_element
FEATURE [App::DocumentObjectGroupPython] O_element112  label="O_element : 065"  # scripted group (container) (typed FeaturePython)
  n = 4
  ref = O_element
FEATURE [App::DocumentObjectGroupPython] G4_DACRON  # scripted group (container) (typed FeaturePython)
  Dunit = g/cm3
  Dvalue = 1.4
  Group = -> [C_element129,H_element119,O_element112]
  conduct = 2
  density = 1
  expand = 3
  formula = G4_DACRON
  name = G4_DACRON
  specific = 4
FEATURE [App::DocumentObjectGroupPython] C_element130  label="C_element : 075"  # scripted group (container) (typed FeaturePython)
  n = 4
  ref = C_element
FEATURE [App::DocumentObjectGroupPython] H_element120  label="H_element : 067"  # scripted group (container) (typed FeaturePython)
  n = 5
  ref = H_element
FEATURE [App::DocumentObjectGroupPython] Cl_element030  label="Cl_element : 016"  # scripted group (container) (typed FeaturePython)
  n = 1
  ref = Cl_element
FEATURE [App::DocumentObjectGroupPython] G4_NEOPRENE  # scripted group (container) (typed FeaturePython)
  Dunit = g/cm3
  Dvalue = 1.23
  Group = -> [C_element130,H_element120,Cl_element030]
  conduct = 2
  density = 1
  expand = 3
  formula = G4_NEOPRENE
  name = G4_NEOPRENE
  specific = 4
FEATURE [App::DocumentObjectGroupPython] Space  # scripted group (container) (typed FeaturePython)
  Group = -> [G4_KEVLAR,G4_DACRON,G4_NEOPRENE]
FEATURE [App::DocumentObjectGroupPython] H_element121  label="H_element : 068"  # scripted group (container) (typed FeaturePython)
  n = 5
  ref = H_element
FEATURE [App::DocumentObjectGroupPython] C_element131  label="C_element : 076"  # scripted group (container) (typed FeaturePython)
  n = 4
  ref = C_element
FEATURE [App::DocumentObjectGroupPython] N_element051  label="N_element : 3"  # scripted group (container) (typed FeaturePython)
  n = 3
  ref = N_element
FEATURE [App::DocumentObjectGroupPython] O_element113  label="O_element : 066"  # scripted group (container) (typed FeaturePython)
  n = 1
  ref = O_element
FEATURE [App::DocumentObjectGroupPython] G4_CYTOSINE  # scripted group (container) (typed FeaturePython)
  Dunit = g/cm3
  Dvalue = 1.55
  Group = -> [H_element121,C_element131,N_element051,O_element113]
  conduct = 2
  density = 1
  expand = 3
  formula = G4_CYTOSINE
  name = G4_CYTOSINE
  specific = 4
FEATURE [App::DocumentObjectGroupPython] H_element122  label="H_element : 069"  # scripted group (container) (typed FeaturePython)
  n = 6
  ref = H_element
FEATURE [App::DocumentObjectGroupPython] C_element132  label="C_element : 077"  # scripted group (container) (typed FeaturePython)
  n = 5
  ref = C_element
FEATURE [App::DocumentObjectGroupPython] N_element052  label="N_element : 024"  # scripted group (container) (typed FeaturePython)
  n = 2
  ref = N_element
FEATURE [App::DocumentObjectGroupPython] O_element114  label="O_element : 067"  # scripted group (container) (typed FeaturePython)
  n = 2
  ref = O_element
FEATURE [App::DocumentObjectGroupPython] G4_THYMINE  # scripted group (container) (typed FeaturePython)
  Dunit = g/cm3
  Dvalue = 1.23
  Group = -> [H_element122,C_element132,N_element052,O_element114]
  conduct = 2
  density = 1
  expand = 3
  formula = G4_THYMINE
  name = G4_THYMINE
  specific = 4
FEATURE [App::DocumentObjectGroupPython] H_element123  label="H_element : 070"  # scripted group (container) (typed FeaturePython)
  n = 4
  ref = H_element
FEATURE [App::DocumentObjectGroupPython] C_element133  label="C_element : 078"  # scripted group (container) (typed FeaturePython)
  n = 4
  ref = C_element
FEATURE [App::DocumentObjectGroupPython] N_element053  label="N_element : 025"  # scripted group (container) (typed FeaturePython)
  n = 2
  ref = N_element
FEATURE [App::DocumentObjectGroupPython] O_element115  label="O_element : 068"  # scripted group (container) (typed FeaturePython)
  n = 2
  ref = O_element
FEATURE [App::DocumentObjectGroupPython] G4_URACIL  # scripted group (container) (typed FeaturePython)
  Dunit = g/cm3
  Dvalue = 1.32
  Group = -> [H_element123,C_element133,N_element053,O_element115]
  conduct = 2
  density = 1
  expand = 3
  formula = G4_URACIL
  name = G4_URACIL
  specific = 4
FEATURE [App::DocumentObjectGroupPython] H_element124  label="H_element : 071"  # scripted group (container) (typed FeaturePython)
  n = 4
  ref = H_element
FEATURE [App::DocumentObjectGroupPython] C_element134  label="C_element : 079"  # scripted group (container) (typed FeaturePython)
  n = 5
  ref = C_element
FEATURE [App::DocumentObjectGroupPython] N_element054  label="N_element : 026"  # scripted group (container) (typed FeaturePython)
  n = 5
  ref = N_element
FEATURE [App::DocumentObjectGroupPython] G4_DNA_ADENINE  # scripted group (container) (typed FeaturePython)
  Dunit = g/cm3
  Dvalue = 1
  Group = -> [H_element124,C_element134,N_element054]
  conduct = 2
  density = 1
  expand = 3
  formula = G4_DNA_ADENINE
  name = G4_DNA_ADENINE
  specific = 4
FEATURE [App::DocumentObjectGroupPython] H_element125  label="H_element : 072"  # scripted group (container) (typed FeaturePython)
  n = 4
  ref = H_element
FEATURE [App::DocumentObjectGroupPython] C_element135  label="C_element : 080"  # scripted group (container) (typed FeaturePython)
  n = 5
  ref = C_element
FEATURE [App::DocumentObjectGroupPython] N_element055  label="N_element : 027"  # scripted group (container) (typed FeaturePython)
  n = 5
  ref = N_element
FEATURE [App::DocumentObjectGroupPython] O_element116  label="O_element : 069"  # scripted group (container) (typed FeaturePython)
  n = 1
  ref = O_element
FEATURE [App::DocumentObjectGroupPython] G4_DNA_GUANINE  # scripted group (container) (typed FeaturePython)
  Dunit = g/cm3
  Dvalue = 1
  Group = -> [H_element125,C_element135,N_element055,O_element116]
  conduct = 2
  density = 1
  expand = 3
  formula = G4_DNA_GUANINE
  name = G4_DNA_GUANINE
  specific = 4
FEATURE [App::DocumentObjectGroupPython] H_element126  label="H_element : 073"  # scripted group (container) (typed FeaturePython)
  n = 4
  ref = H_element
FEATURE [App::DocumentObjectGroupPython] C_element136  label="C_element : 081"  # scripted group (container) (typed FeaturePython)
  n = 4
  ref = C_element
FEATURE [App::DocumentObjectGroupPython] N_element056  label="N_element : 028"  # scripted group (container) (typed FeaturePython)
  n = 3
  ref = N_element
FEATURE [App::DocumentObjectGroupPython] O_element117  label="O_element : 070"  # scripted group (container) (typed FeaturePython)
  n = 1
  ref = O_element
FEATURE [App::DocumentObjectGroupPython] G4_DNA_CYTOSINE  # scripted group (container) (typed FeaturePython)
  Dunit = g/cm3
  Dvalue = 1
  Group = -> [H_element126,C_element136,N_element056,O_element117]
  conduct = 2
  density = 1
  expand = 3
  formula = G4_DNA_CYTOSINE
  name = G4_DNA_CYTOSINE
  specific = 4
FEATURE [App::DocumentObjectGroupPython] H_element127  label="H_element : 074"  # scripted group (container) (typed FeaturePython)
  n = 5
  ref = H_element
FEATURE [App::DocumentObjectGroupPython] C_element137  label="C_element : 082"  # scripted group (container) (typed FeaturePython)
  n = 5
  ref = C_element
FEATURE [App::DocumentObjectGroupPython] N_element057  label="N_element : 029"  # scripted group (container) (typed FeaturePython)
  n = 2
  ref = N_element
FEATURE [App::DocumentObjectGroupPython] O_element118  label="O_element : 071"  # scripted group (container) (typed FeaturePython)
  n = 2
  ref = O_element
FEATURE [App::DocumentObjectGroupPython] G4_DNA_THYMINE  # scripted group (container) (typed FeaturePython)
  Dunit = g/cm3
  Dvalue = 1
  Group = -> [H_element127,C_element137,N_element057,O_element118]
  conduct = 2
  density = 1
  expand = 3
  formula = G4_DNA_THYMINE
  name = G4_DNA_THYMINE
  specific = 4
FEATURE [App::DocumentObjectGroupPython] H_element128  label="H_element : 075"  # scripted group (container) (typed FeaturePython)
  n = 3
  ref = H_element
FEATURE [App::DocumentObjectGroupPython] C_element138  label="C_element : 083"  # scripted group (container) (typed FeaturePython)
  n = 4
  ref = C_element
FEATURE [App::DocumentObjectGroupPython] N_element058  label="N_element : 030"  # scripted group (container) (typed FeaturePython)
  n = 2
  ref = N_element
FEATURE [App::DocumentObjectGroupPython] O_element119  label="O_element : 072"  # scripted group (container) (typed FeaturePython)
  n = 2
  ref = O_element
FEATURE [App::DocumentObjectGroupPython] G4_DNA_URACIL  # scripted group (container) (typed FeaturePython)
  Dunit = g/cm3
  Dvalue = 1
  Group = -> [H_element128,C_element138,N_element058,O_element119]
  conduct = 2
  density = 1
  expand = 3
  formula = G4_DNA_URACIL
  name = G4_DNA_URACIL
  specific = 4
FEATURE [App::DocumentObjectGroupPython] H_element129  label="H_element : 076"  # scripted group (container) (typed FeaturePython)
  n = 10
  ref = H_element
FEATURE [App::DocumentObjectGroupPython] C_element139  label="C_element : 084"  # scripted group (container) (typed FeaturePython)
  n = 10
  ref = C_element
FEATURE [App::DocumentObjectGroupPython] N_element059  label="N_element : 031"  # scripted group (container) (typed FeaturePython)
  n = 5
  ref = N_element
FEATURE [App::DocumentObjectGroupPython] O_element120  label="O_element : 073"  # scripted group (container) (typed FeaturePython)
  n = 4
  ref = O_element
FEATURE [App::DocumentObjectGroupPython] G4_DNA_ADENOSINE  # scripted group (container) (typed FeaturePython)
  Dunit = g/cm3
  Dvalue = 1
  Group = -> [H_element129,C_element139,N_element059,O_element120]
  conduct = 2
  density = 1
  expand = 3
  formula = G4_DNA_ADENOSINE
  name = G4_DNA_ADENOSINE
  specific = 4
FEATURE [App::DocumentObjectGroupPython] H_element130  label="H_element : 077"  # scripted group (container) (typed FeaturePython)
  n = 10
  ref = H_element
FEATURE [App::DocumentObjectGroupPython] C_element140  label="C_element : 085"  # scripted group (container) (typed FeaturePython)
  n = 10
  ref = C_element
FEATURE [App::DocumentObjectGroupPython] N_element060  label="N_element : 032"  # scripted group (container) (typed FeaturePython)
  n = 5
  ref = N_element
FEATURE [App::DocumentObjectGroupPython] O_element121  label="O_element : 074"  # scripted group (container) (typed FeaturePython)
  n = 5
  ref = O_element
FEATURE [App::DocumentObjectGroupPython] G4_DNA_GUANOSINE  # scripted group (container) (typed FeaturePython)
  Dunit = g/cm3
  Dvalue = 1
  Group = -> [H_element130,C_element140,N_element060,O_element121]
  conduct = 2
  density = 1
  expand = 3
  formula = G4_DNA_GUANOSINE
  name = G4_DNA_GUANOSINE
  specific = 4
FEATURE [App::DocumentObjectGroupPython] H_element131  label="H_element : 078"  # scripted group (container) (typed FeaturePython)
  n = 10
  ref = H_element
FEATURE [App::DocumentObjectGroupPython] C_element141  label="C_element : 086"  # scripted group (container) (typed FeaturePython)
  n = 9
  ref = C_element
FEATURE [App::DocumentObjectGroupPython] N_element061  label="N_element : 033"  # scripted group (container) (typed FeaturePython)
  n = 3
  ref = N_element
FEATURE [App::DocumentObjectGroupPython] O_element122  label="O_element : 075"  # scripted group (container) (typed FeaturePython)
  n = 5
  ref = O_element
FEATURE [App::DocumentObjectGroupPython] G4_DNA_CYTIDINE  # scripted group (container) (typed FeaturePython)
  Dunit = g/cm3
  Dvalue = 1
  Group = -> [H_element131,C_element141,N_element061,O_element122]
  conduct = 2
  density = 1
  expand = 3
  formula = G4_DNA_CYTIDINE
  name = G4_DNA_CYTIDINE
  specific = 4
FEATURE [App::DocumentObjectGroupPython] H_element132  label="H_element : 079"  # scripted group (container) (typed FeaturePython)
  n = 9
  ref = H_element
FEATURE [App::DocumentObjectGroupPython] C_element142  label="C_element : 087"  # scripted group (container) (typed FeaturePython)
  n = 9
  ref = C_element
FEATURE [App::DocumentObjectGroupPython] N_element062  label="N_element : 034"  # scripted group (container) (typed FeaturePython)
  n = 2
  ref = N_element
FEATURE [App::DocumentObjectGroupPython] O_element123  label="O_element : 076"  # scripted group (container) (typed FeaturePython)
  n = 6
  ref = O_element
FEATURE [App::DocumentObjectGroupPython] G4_DNA_URIDINE  # scripted group (container) (typed FeaturePython)
  Dunit = g/cm3
  Dvalue = 1
  Group = -> [H_element132,C_element142,N_element062,O_element123]
  conduct = 2
  density = 1
  expand = 3
  formula = G4_DNA_URIDINE
  name = G4_DNA_URIDINE
  specific = 4
FEATURE [App::DocumentObjectGroupPython] H_element133  label="H_element : 080"  # scripted group (container) (typed FeaturePython)
  n = 11
  ref = H_element
FEATURE [App::DocumentObjectGroupPython] C_element143  label="C_element : 088"  # scripted group (container) (typed FeaturePython)
  n = 10
  ref = C_element
FEATURE [App::DocumentObjectGroupPython] N_element063  label="N_element : 035"  # scripted group (container) (typed FeaturePython)
  n = 2
  ref = N_element
FEATURE [App::DocumentObjectGroupPython] O_element124  label="O_element : 077"  # scripted group (container) (typed FeaturePython)
  n = 6
  ref = O_element
FEATURE [App::DocumentObjectGroupPython] G4_DNA_METHYLURIDINE  # scripted group (container) (typed FeaturePython)
  Dunit = g/cm3
  Dvalue = 1
  Group = -> [H_element133,C_element143,N_element063,O_element124]
  conduct = 2
  density = 1
  expand = 3
  formula = G4_DNA_METHYLURIDINE
  name = G4_DNA_METHYLURIDINE
  specific = 4
FEATURE [App::DocumentObjectGroupPython] P_element014  label="P_element : 003"  # scripted group (container) (typed FeaturePython)
  n = 1
  ref = P_element
FEATURE [App::DocumentObjectGroupPython] O_element125  label="O_element : 078"  # scripted group (container) (typed FeaturePython)
  n = 3
  ref = O_element
FEATURE [App::DocumentObjectGroupPython] G4_DNA_MONOPHOSPHATE  # scripted group (container) (typed FeaturePython)
  Dunit = g/cm3
  Dvalue = 1
  Group = -> [P_element014,O_element125]
  conduct = 2
  density = 1
  expand = 3
  formula = G4_DNA_MONOPHOSPHATE
  name = G4_DNA_MONOPHOSPHATE
  specific = 4
FEATURE [App::DocumentObjectGroupPython] H_element134  label="H_element : 081"  # scripted group (container) (typed FeaturePython)
  n = 10
  ref = H_element
FEATURE [App::DocumentObjectGroupPython] C_element144  label="C_element : 089"  # scripted group (container) (typed FeaturePython)
  n = 10
  ref = C_element
FEATURE [App::DocumentObjectGroupPython] N_element064  label="N_element : 036"  # scripted group (container) (typed FeaturePython)
  n = 5
  ref = N_element
FEATURE [App::DocumentObjectGroupPython] O_element126  label="O_element : 079"  # scripted group (container) (typed FeaturePython)
  n = 7
  ref = O_element
FEATURE [App::DocumentObjectGroupPython] P_element015  label="P_element : 004"  # scripted group (container) (typed FeaturePython)
  n = 1
  ref = P_element
FEATURE [App::DocumentObjectGroupPython] G4_DNA_A  # scripted group (container) (typed FeaturePython)
  Dunit = g/cm3
  Dvalue = 1
  Group = -> [H_element134,C_element144,N_element064,O_element126,P_element015]
  conduct = 2
  density = 1
  expand = 3
  formula = G4_DNA_A
  name = G4_DNA_A
  specific = 4
FEATURE [App::DocumentObjectGroupPython] H_element135  label="H_element : 082"  # scripted group (container) (typed FeaturePython)
  n = 10
  ref = H_element
FEATURE [App::DocumentObjectGroupPython] C_element145  label="C_element : 090"  # scripted group (container) (typed FeaturePython)
  n = 10
  ref = C_element
FEATURE [App::DocumentObjectGroupPython] N_element065  label="N_element : 037"  # scripted group (container) (typed FeaturePython)
  n = 5
  ref = N_element
FEATURE [App::DocumentObjectGroupPython] O_element127  label="O_element : 8"  # scripted group (container) (typed FeaturePython)
  n = 8
  ref = O_element
FEATURE [App::DocumentObjectGroupPython] P_element016  label="P_element : 005"  # scripted group (container) (typed FeaturePython)
  n = 1
  ref = P_element
FEATURE [App::DocumentObjectGroupPython] G4_DNA_G  # scripted group (container) (typed FeaturePython)
  Dunit = g/cm3
  Dvalue = 1
  Group = -> [H_element135,C_element145,N_element065,O_element127,P_element016]
  conduct = 2
  density = 1
  expand = 3
  formula = G4_DNA_G
  name = G4_DNA_G
  specific = 4
FEATURE [App::DocumentObjectGroupPython] H_element136  label="H_element : 083"  # scripted group (container) (typed FeaturePython)
  n = 10
  ref = H_element
FEATURE [App::DocumentObjectGroupPython] C_element146  label="C_element : 091"  # scripted group (container) (typed FeaturePython)
  n = 9
  ref = C_element
FEATURE [App::DocumentObjectGroupPython] N_element066  label="N_element : 038"  # scripted group (container) (typed FeaturePython)
  n = 3
  ref = N_element
FEATURE [App::DocumentObjectGroupPython] O_element128  label="O_element : 080"  # scripted group (container) (typed FeaturePython)
  n = 8
  ref = O_element
FEATURE [App::DocumentObjectGroupPython] P_element017  label="P_element : 006"  # scripted group (container) (typed FeaturePython)
  n = 1
  ref = P_element
FEATURE [App::DocumentObjectGroupPython] G4_DNA_C  # scripted group (container) (typed FeaturePython)
  Dunit = g/cm3
  Dvalue = 1
  Group = -> [H_element136,C_element146,N_element066,O_element128,P_element017]
  conduct = 2
  density = 1
  expand = 3
  formula = G4_DNA_C
  name = G4_DNA_C
  specific = 4
FEATURE [App::DocumentObjectGroupPython] H_element137  label="H_element : 084"  # scripted group (container) (typed FeaturePython)
  n = 9
  ref = H_element
FEATURE [App::DocumentObjectGroupPython] C_element147  label="C_element : 092"  # scripted group (container) (typed FeaturePython)
  n = 9
  ref = C_element
FEATURE [App::DocumentObjectGroupPython] N_element067  label="N_element : 039"  # scripted group (container) (typed FeaturePython)
  n = 2
  ref = N_element
FEATURE [App::DocumentObjectGroupPython] O_element129  label="O_element : 9"  # scripted group (container) (typed FeaturePython)
  n = 9
  ref = O_element
FEATURE [App::DocumentObjectGroupPython] P_element018  label="P_element : 007"  # scripted group (container) (typed FeaturePython)
  n = 1
  ref = P_element
FEATURE [App::DocumentObjectGroupPython] G4_DNA_U  # scripted group (container) (typed FeaturePython)
  Dunit = g/cm3
  Dvalue = 1
  Group = -> [H_element137,C_element147,N_element067,O_element129,P_element018]
  conduct = 2
  density = 1
  expand = 3
  formula = G4_DNA_U
  name = G4_DNA_U
  specific = 4
FEATURE [App::DocumentObjectGroupPython] H_element138  label="H_element : 085"  # scripted group (container) (typed FeaturePython)
  n = 11
  ref = H_element
FEATURE [App::DocumentObjectGroupPython] C_element148  label="C_element : 093"  # scripted group (container) (typed FeaturePython)
  n = 10
  ref = C_element
FEATURE [App::DocumentObjectGroupPython] N_element068  label="N_element : 040"  # scripted group (container) (typed FeaturePython)
  n = 2
  ref = N_element
FEATURE [App::DocumentObjectGroupPython] O_element130  label="O_element : 081"  # scripted group (container) (typed FeaturePython)
  n = 9
  ref = O_element
FEATURE [App::DocumentObjectGroupPython] P_element019  label="P_element : 008"  # scripted group (container) (typed FeaturePython)
  n = 1
  ref = P_element
FEATURE [App::DocumentObjectGroupPython] G4_DNA_MU  # scripted group (container) (typed FeaturePython)
  Dunit = g/cm3
  Dvalue = 1
  Group = -> [H_element138,C_element148,N_element068,O_element130,P_element019]
  conduct = 2
  density = 1
  expand = 3
  formula = G4_DNA_MU
  name = G4_DNA_MU
  specific = 4
FEATURE [App::DocumentObjectGroupPython] BioChemical  # scripted group (container) (typed FeaturePython)
  Group = -> [G4_CYTOSINE,G4_THYMINE,G4_URACIL,G4_DNA_ADENINE,G4_DNA_GUANINE,G4_DNA_CYTOSINE,G4_DNA_THYMINE,G4_DNA_URACIL,G4_DNA_ADENOSINE,G4_DNA_GUANOSINE,G4_DNA_CYTIDINE,G4_DNA_URIDINE,G4_DNA_METHYLURIDINE,G4_DNA_MONOPHOSPHATE,G4_DNA_A,G4_DNA_G,G4_DNA_C,G4_DNA_U,G4_DNA_MU]
FEATURE [App::DocumentObjectGroupPython] G4Materials  # scripted group (container) (typed FeaturePython)
  Group = -> [NIST,Element,HEP,Space,BioChemical]
  version = 1
FEATURE [App::DocumentObjectGroupPython] Geant4  # scripted group (container) (typed FeaturePython)
  Group = -> [G4Isotopes,G4Elements,G4Materials]
FEATURE [App::DocumentObjectGroupPython] Materials  # scripted group (container) (typed FeaturePython)
  Group = -> [Geant4]
FEATURE [Part::FeaturePython] GDMLBox_WorldBox  # WARN: FeaturePython — macro-defined, semantics opaque (R4)
  lunit = 2
  material = 5
  x = 100
  y = 100
  z = 100
FEATURE [Sketcher::SketchObject] Sketch
  ArcFitTolerance = 0
  FullyConstrained = false
  MakeInternals = false
  sketch-geometry (15):
    g0-g5: Circle [constr] x6 (B-spline internal-alignment scaffolding for g6; pole/knot coordinates omitted)
    g6: BSplineCurve PolesCount=7 KnotsCount=5 Degree=3 IsPeriodic=0
    g7-g10: GeomPoint [constr] x4 (B-spline internal-alignment scaffolding for g6; pole/knot coordinates omitted)
    g11: LineSegment StartX=-4.39557 StartY=8.39124 StartZ=0 EndX=-5.2662 EndY=10.5884 EndZ=0
    g12: LineSegment StartX=-5.2662 StartY=10.5884 StartZ=0 EndX=-7.82152 EndY=9.89481 EndZ=0
    g13: LineSegment StartX=-7.82152 StartY=9.89481 StartZ=0 EndX=-9.50073 EndY=7.63152 EndZ=0
    g14: ArcOfCircle CenterX=-7.8377 CenterY=5.34547 CenterZ=0 NormalX=0 NormalY=0 NormalZ=1 AngleXU=0 Radius=2.82696 StartAngle=4.84147 EndAngle=8.48291
  constraints (9):
    c: Weight(g0) = 1
    c: Equal(g0, g1-g5) x5
    c: InternalAlignment(g0-g5 -> g6) x6
    c: InternalAlignment(g7-g10 -> g6) x4
    c: Coincident(g11,g6)
    c: Coincident(g11,g12)
    c: Coincident(g12,g13)
    c: Coincident(g14,g13)
    c: Coincident(g14,g6)
FEATURE [Part::Extrusion] Extrude
  Base = -> Sketch
  Dir = (0,0,1)
  DirMode = 2
  FaceMakerClass = Part::FaceMakerBullseye
  FaceMakerMode = 3
  LengthFwd = 10
  LengthRev = 0
  Placement = pos=(13,12,0) rot=(0,0,1;0rad)
  Solid = true
  Symmetric = false
  material = 1
FEATURE [Part::Mirroring] Part__Mirroring  label="mirror1"
  Base = (0,0,0)
  Normal = (1,0,0)
  Placement = pos=(0,0,0) rot=(0,0,1;0.523599rad)
  Source = -> Extrude
  material = 261
FEATURE [Part::Mirroring] Part__Mirroring002  label="mirror2"
  Base = (0,0,0)
  Normal = (0,1,0)
  Source = -> Part__Mirroring
FEATURE [App::Part] Part
  Group = -> [Sketch,Extrude,Part__Mirroring,Part__Mirroring002]
  Origin = -> Origin001
FEATURE [App::Part] worldVOL
  Group = -> [GDMLBox_WorldBox,Part]
  Origin = -> Origin
